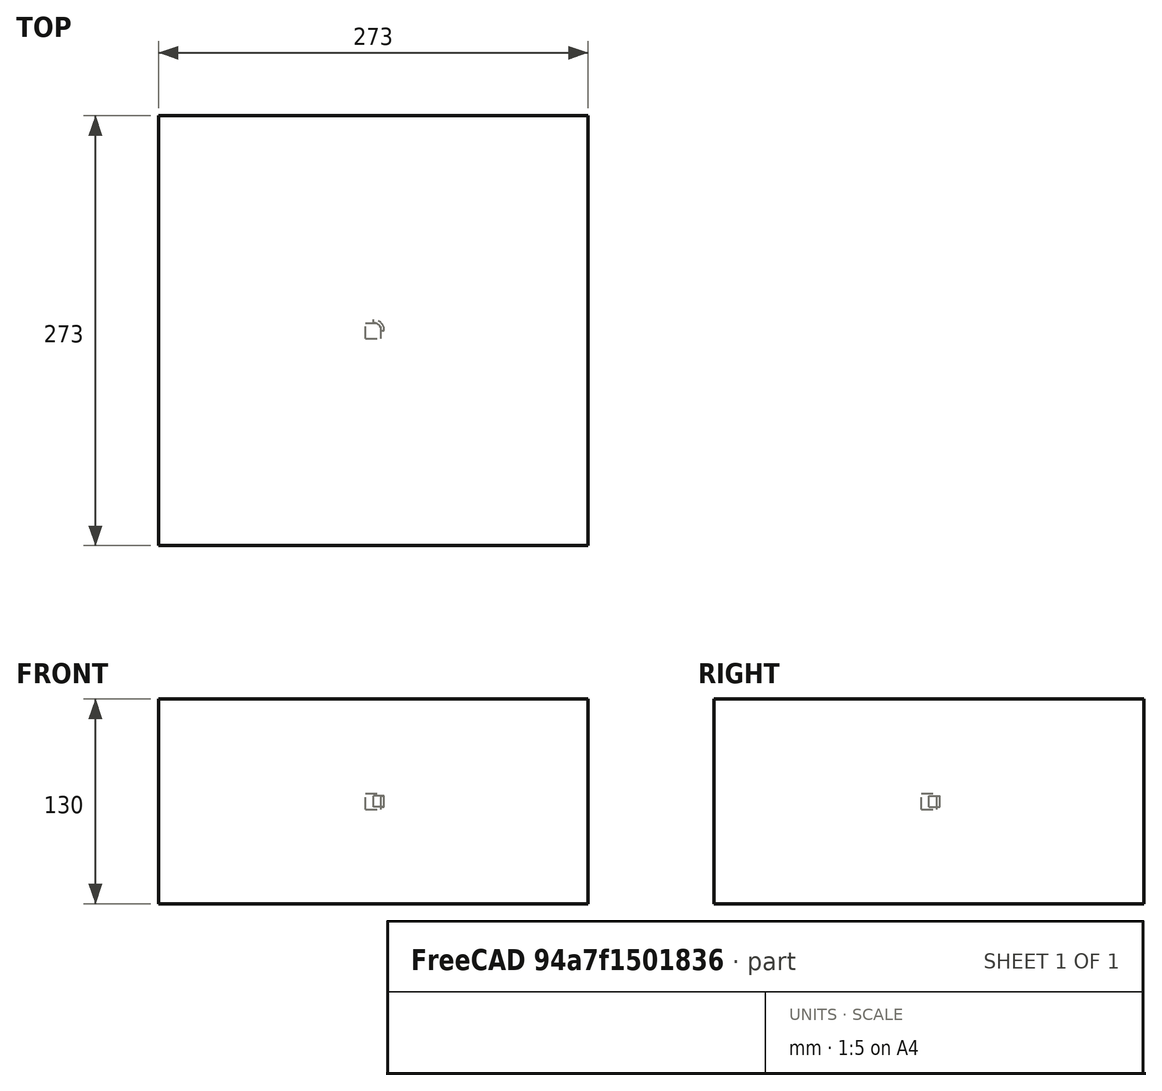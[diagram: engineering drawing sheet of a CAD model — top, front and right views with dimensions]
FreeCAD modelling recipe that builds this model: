
FCSTD DOCUMENT  (FreeCAD 0.20RUnknown)
Label: polarArray-container-a
License: All rights reserved
LicenseURL: http://en.wikipedia.org/wiki/All_rights_reserved
objects: App::DocumentObjectGroupPython×1251, Part::FeaturePython×4, App::Part×4
note: 3 computed .brp shape members not serialized (recipe doc carries the construction recipe); baked Part::Feature solids carry a one-line shape summary decoded from their .brp

FEATURE [App::DocumentObjectGroupPython] HALFPI  # scripted group (container) (typed FeaturePython)
  name = HALFPI
  value = pi/2.
FEATURE [App::DocumentObjectGroupPython] PI  # scripted group (container) (typed FeaturePython)
  name = PI
  value = 1.*pi
FEATURE [App::DocumentObjectGroupPython] TWOPI  # scripted group (container) (typed FeaturePython)
  name = TWOPI
  value = 2.*pi
FEATURE [App::DocumentObjectGroupPython] Constants  # scripted group (container) (typed FeaturePython)
  Group = -> [HALFPI,PI,TWOPI]
FEATURE [App::DocumentObjectGroupPython] Variables  # scripted group (container) (typed FeaturePython)
FEATURE [App::DocumentObjectGroupPython] Quantities  # scripted group (container) (typed FeaturePython)
FEATURE [App::DocumentObjectGroupPython] Isotopes  # scripted group (container) (typed FeaturePython)
FEATURE [App::DocumentObjectGroupPython] Elements  # scripted group (container) (typed FeaturePython)
FEATURE [App::DocumentObjectGroupPython] Matrix  # scripted group (container) (typed FeaturePython)
FEATURE [App::DocumentObjectGroupPython] Surfaces  # scripted group (container) (typed FeaturePython)
FEATURE [App::DocumentObjectGroupPython] Opticals  # scripted group (container) (typed FeaturePython)
  Group = -> [Matrix,Surfaces]
FEATURE [App::DocumentObjectGroupPython] G4Isotopes  # scripted group (container) (typed FeaturePython)
FEATURE [App::DocumentObjectGroupPython] H_element  # scripted group (container) (typed FeaturePython)
  Z = 1
  atom_value = 1.008
  formula = H
  name = H_element
FEATURE [App::DocumentObjectGroupPython] He_element  # scripted group (container) (typed FeaturePython)
  Z = 2
  atom_value = 4.0026
  formula = He
  name = He_element
FEATURE [App::DocumentObjectGroupPython] Li_element  # scripted group (container) (typed FeaturePython)
  Z = 3
  atom_value = 6.94
  formula = Li
  name = Li_element
FEATURE [App::DocumentObjectGroupPython] Be_element  # scripted group (container) (typed FeaturePython)
  Z = 4
  atom_value = 9.01218
  formula = Be
  name = Be_element
FEATURE [App::DocumentObjectGroupPython] B_element  # scripted group (container) (typed FeaturePython)
  Z = 5
  atom_value = 10.81
  formula = B
  name = B_element
FEATURE [App::DocumentObjectGroupPython] C_element  # scripted group (container) (typed FeaturePython)
  Z = 6
  atom_value = 12.011
  formula = C
  name = C_element
FEATURE [App::DocumentObjectGroupPython] N_element  # scripted group (container) (typed FeaturePython)
  Z = 7
  atom_value = 14.007
  formula = N
  name = N_element
FEATURE [App::DocumentObjectGroupPython] O_element  # scripted group (container) (typed FeaturePython)
  Z = 8
  atom_value = 15.999
  formula = O
  name = O_element
FEATURE [App::DocumentObjectGroupPython] F_element  # scripted group (container) (typed FeaturePython)
  Z = 9
  atom_value = 18.9984
  formula = F
  name = F_element
FEATURE [App::DocumentObjectGroupPython] Ne_element  # scripted group (container) (typed FeaturePython)
  Z = 10
  atom_value = 20.1797
  formula = Ne
  name = Ne_element
FEATURE [App::DocumentObjectGroupPython] Na_element  # scripted group (container) (typed FeaturePython)
  Z = 11
  atom_value = 22.9898
  formula = Na
  name = Na_element
FEATURE [App::DocumentObjectGroupPython] Mg_element  # scripted group (container) (typed FeaturePython)
  Z = 12
  atom_value = 24.305
  formula = Mg
  name = Mg_element
FEATURE [App::DocumentObjectGroupPython] Al_element  # scripted group (container) (typed FeaturePython)
  Z = 13
  atom_value = 26.9815
  formula = Al
  name = Al_element
FEATURE [App::DocumentObjectGroupPython] Si_element  # scripted group (container) (typed FeaturePython)
  Z = 14
  atom_value = 28.085
  formula = Si
  name = Si_element
FEATURE [App::DocumentObjectGroupPython] P_element  # scripted group (container) (typed FeaturePython)
  Z = 15
  atom_value = 30.9738
  formula = P
  name = P_element
FEATURE [App::DocumentObjectGroupPython] S_element  # scripted group (container) (typed FeaturePython)
  Z = 16
  atom_value = 32.06
  formula = S
  name = S_element
FEATURE [App::DocumentObjectGroupPython] Cl_element  # scripted group (container) (typed FeaturePython)
  Z = 17
  atom_value = 35.45
  formula = Cl
  name = Cl_element
FEATURE [App::DocumentObjectGroupPython] Ar_element  # scripted group (container) (typed FeaturePython)
  Z = 18
  atom_value = 39.95
  formula = Ar
  name = Ar_element
FEATURE [App::DocumentObjectGroupPython] K_element  # scripted group (container) (typed FeaturePython)
  Z = 19
  atom_value = 39.0983
  formula = K
  name = K_element
FEATURE [App::DocumentObjectGroupPython] Ca_element  # scripted group (container) (typed FeaturePython)
  Z = 20
  atom_value = 40.078
  formula = Ca
  name = Ca_element
FEATURE [App::DocumentObjectGroupPython] Sc_element  # scripted group (container) (typed FeaturePython)
  Z = 21
  atom_value = 44.9559
  formula = Sc
  name = Sc_element
FEATURE [App::DocumentObjectGroupPython] Ti_element  # scripted group (container) (typed FeaturePython)
  Z = 22
  atom_value = 47.867
  formula = Ti
  name = Ti_element
FEATURE [App::DocumentObjectGroupPython] V_element  # scripted group (container) (typed FeaturePython)
  Z = 23
  atom_value = 50.9415
  formula = V
  name = V_element
FEATURE [App::DocumentObjectGroupPython] Cr_element  # scripted group (container) (typed FeaturePython)
  Z = 24
  atom_value = 51.9961
  formula = Cr
  name = Cr_element
FEATURE [App::DocumentObjectGroupPython] Mn_element  # scripted group (container) (typed FeaturePython)
  Z = 25
  atom_value = 54.938
  formula = Mn
  name = Mn_element
FEATURE [App::DocumentObjectGroupPython] Fe_element  # scripted group (container) (typed FeaturePython)
  Z = 26
  atom_value = 55.845
  formula = Fe
  name = Fe_element
FEATURE [App::DocumentObjectGroupPython] Co_element  # scripted group (container) (typed FeaturePython)
  Z = 27
  atom_value = 58.9332
  formula = Co
  name = Co_element
FEATURE [App::DocumentObjectGroupPython] Ni_element  # scripted group (container) (typed FeaturePython)
  Z = 28
  atom_value = 58.6934
  formula = Ni
  name = Ni_element
FEATURE [App::DocumentObjectGroupPython] Cu_element  # scripted group (container) (typed FeaturePython)
  Z = 29
  atom_value = 63.546
  formula = Cu
  name = Cu_element
FEATURE [App::DocumentObjectGroupPython] Zn_element  # scripted group (container) (typed FeaturePython)
  Z = 30
  atom_value = 65.38
  formula = Zn
  name = Zn_element
FEATURE [App::DocumentObjectGroupPython] Ga_element  # scripted group (container) (typed FeaturePython)
  Z = 31
  atom_value = 69.723
  formula = Ga
  name = Ga_element
FEATURE [App::DocumentObjectGroupPython] Ge_element  # scripted group (container) (typed FeaturePython)
  Z = 32
  atom_value = 72.63
  formula = Ge
  name = Ge_element
FEATURE [App::DocumentObjectGroupPython] As_element  # scripted group (container) (typed FeaturePython)
  Z = 33
  atom_value = 74.9216
  formula = As
  name = As_element
FEATURE [App::DocumentObjectGroupPython] Se_element  # scripted group (container) (typed FeaturePython)
  Z = 34
  atom_value = 78.971
  formula = Se
  name = Se_element
FEATURE [App::DocumentObjectGroupPython] Br_element  # scripted group (container) (typed FeaturePython)
  Z = 35
  atom_value = 79.904
  formula = Br
  name = Br_element
FEATURE [App::DocumentObjectGroupPython] Kr_element  # scripted group (container) (typed FeaturePython)
  Z = 36
  atom_value = 83.798
  formula = Kr
  name = Kr_element
FEATURE [App::DocumentObjectGroupPython] Rb_element  # scripted group (container) (typed FeaturePython)
  Z = 37
  atom_value = 85.4678
  formula = Rb
  name = Rb_element
FEATURE [App::DocumentObjectGroupPython] Sr_element  # scripted group (container) (typed FeaturePython)
  Z = 38
  atom_value = 87.62
  formula = Sr
  name = Sr_element
FEATURE [App::DocumentObjectGroupPython] Y_element  # scripted group (container) (typed FeaturePython)
  Z = 39
  atom_value = 88.9058
  formula = Y
  name = Y_element
FEATURE [App::DocumentObjectGroupPython] Zr_element  # scripted group (container) (typed FeaturePython)
  Z = 40
  atom_value = 91.224
  formula = Zr
  name = Zr_element
FEATURE [App::DocumentObjectGroupPython] Nb_element  # scripted group (container) (typed FeaturePython)
  Z = 41
  atom_value = 92.9064
  formula = Nb
  name = Nb_element
FEATURE [App::DocumentObjectGroupPython] Mo_element  # scripted group (container) (typed FeaturePython)
  Z = 42
  atom_value = 95.95
  formula = Mo
  name = Mo_element
FEATURE [App::DocumentObjectGroupPython] Tc_element  # scripted group (container) (typed FeaturePython)
  Z = 43
  atom_value = 97
  formula = Tc
  name = Tc_element
FEATURE [App::DocumentObjectGroupPython] Ru_element  # scripted group (container) (typed FeaturePython)
  Z = 44
  atom_value = 101.07
  formula = Ru
  name = Ru_element
FEATURE [App::DocumentObjectGroupPython] Rh_element  # scripted group (container) (typed FeaturePython)
  Z = 45
  atom_value = 102.905
  formula = Rh
  name = Rh_element
FEATURE [App::DocumentObjectGroupPython] Pd_element  # scripted group (container) (typed FeaturePython)
  Z = 46
  atom_value = 106.42
  formula = Pd
  name = Pd_element
FEATURE [App::DocumentObjectGroupPython] Ag_element  # scripted group (container) (typed FeaturePython)
  Z = 47
  atom_value = 107.868
  formula = Ag
  name = Ag_element
FEATURE [App::DocumentObjectGroupPython] Cd_element  # scripted group (container) (typed FeaturePython)
  Z = 48
  atom_value = 112.414
  formula = Cd
  name = Cd_element
FEATURE [App::DocumentObjectGroupPython] In_element  # scripted group (container) (typed FeaturePython)
  Z = 49
  atom_value = 114.818
  formula = In
  name = In_element
FEATURE [App::DocumentObjectGroupPython] Sn_element  # scripted group (container) (typed FeaturePython)
  Z = 50
  atom_value = 118.71
  formula = Sn
  name = Sn_element
FEATURE [App::DocumentObjectGroupPython] Sb_element  # scripted group (container) (typed FeaturePython)
  Z = 51
  atom_value = 121.76
  formula = Sb
  name = Sb_element
FEATURE [App::DocumentObjectGroupPython] Te_element  # scripted group (container) (typed FeaturePython)
  Z = 52
  atom_value = 127.6
  formula = Te
  name = Te_element
FEATURE [App::DocumentObjectGroupPython] I_element  # scripted group (container) (typed FeaturePython)
  Z = 53
  atom_value = 126.904
  formula = I
  name = I_element
FEATURE [App::DocumentObjectGroupPython] Xe_element  # scripted group (container) (typed FeaturePython)
  Z = 54
  atom_value = 131.293
  formula = Xe
  name = Xe_element
FEATURE [App::DocumentObjectGroupPython] Cs_element  # scripted group (container) (typed FeaturePython)
  Z = 55
  atom_value = 132.905
  formula = Cs
  name = Cs_element
FEATURE [App::DocumentObjectGroupPython] Ba_element  # scripted group (container) (typed FeaturePython)
  Z = 56
  atom_value = 137.327
  formula = Ba
  name = Ba_element
FEATURE [App::DocumentObjectGroupPython] La_element  # scripted group (container) (typed FeaturePython)
  Z = 57
  atom_value = 138.905
  formula = La
  name = La_element
FEATURE [App::DocumentObjectGroupPython] Ce_element  # scripted group (container) (typed FeaturePython)
  Z = 58
  atom_value = 140.116
  formula = Ce
  name = Ce_element
FEATURE [App::DocumentObjectGroupPython] Pr_element  # scripted group (container) (typed FeaturePython)
  Z = 59
  atom_value = 140.908
  formula = Pr
  name = Pr_element
FEATURE [App::DocumentObjectGroupPython] Nd_element  # scripted group (container) (typed FeaturePython)
  Z = 60
  atom_value = 144.242
  formula = Nd
  name = Nd_element
FEATURE [App::DocumentObjectGroupPython] Pm_element  # scripted group (container) (typed FeaturePython)
  Z = 61
  atom_value = 145
  formula = Pm
  name = Pm_element
FEATURE [App::DocumentObjectGroupPython] Sm_element  # scripted group (container) (typed FeaturePython)
  Z = 62
  atom_value = 150.36
  formula = Sm
  name = Sm_element
FEATURE [App::DocumentObjectGroupPython] Eu_element  # scripted group (container) (typed FeaturePython)
  Z = 63
  atom_value = 151.964
  formula = Eu
  name = Eu_element
FEATURE [App::DocumentObjectGroupPython] Gd_element  # scripted group (container) (typed FeaturePython)
  Z = 64
  atom_value = 157.25
  formula = Gd
  name = Gd_element
FEATURE [App::DocumentObjectGroupPython] Tb_element  # scripted group (container) (typed FeaturePython)
  Z = 65
  atom_value = 158.925
  formula = Tb
  name = Tb_element
FEATURE [App::DocumentObjectGroupPython] Dy_element  # scripted group (container) (typed FeaturePython)
  Z = 66
  atom_value = 162.5
  formula = Dy
  name = Dy_element
FEATURE [App::DocumentObjectGroupPython] Ho_element  # scripted group (container) (typed FeaturePython)
  Z = 67
  atom_value = 164.93
  formula = Ho
  name = Ho_element
FEATURE [App::DocumentObjectGroupPython] Er_element  # scripted group (container) (typed FeaturePython)
  Z = 68
  atom_value = 167.259
  formula = Er
  name = Er_element
FEATURE [App::DocumentObjectGroupPython] Tm_element  # scripted group (container) (typed FeaturePython)
  Z = 69
  atom_value = 168.934
  formula = Tm
  name = Tm_element
FEATURE [App::DocumentObjectGroupPython] Yb_element  # scripted group (container) (typed FeaturePython)
  Z = 70
  atom_value = 173.045
  formula = Yb
  name = Yb_element
FEATURE [App::DocumentObjectGroupPython] Lu_element  # scripted group (container) (typed FeaturePython)
  Z = 71
  atom_value = 174.967
  formula = Lu
  name = Lu_element
FEATURE [App::DocumentObjectGroupPython] Hf_element  # scripted group (container) (typed FeaturePython)
  Z = 72
  atom_value = 178.49
  formula = Hf
  name = Hf_element
FEATURE [App::DocumentObjectGroupPython] Ta_element  # scripted group (container) (typed FeaturePython)
  Z = 73
  atom_value = 180.948
  formula = Ta
  name = Ta_element
FEATURE [App::DocumentObjectGroupPython] W_element  # scripted group (container) (typed FeaturePython)
  Z = 74
  atom_value = 183.84
  formula = W
  name = W_element
FEATURE [App::DocumentObjectGroupPython] Re_element  # scripted group (container) (typed FeaturePython)
  Z = 75
  atom_value = 186.207
  formula = Re
  name = Re_element
FEATURE [App::DocumentObjectGroupPython] Os_element  # scripted group (container) (typed FeaturePython)
  Z = 76
  atom_value = 190.23
  formula = Os
  name = Os_element
FEATURE [App::DocumentObjectGroupPython] Ir_element  # scripted group (container) (typed FeaturePython)
  Z = 77
  atom_value = 192.217
  formula = Ir
  name = Ir_element
FEATURE [App::DocumentObjectGroupPython] Pt_element  # scripted group (container) (typed FeaturePython)
  Z = 78
  atom_value = 195.084
  formula = Pt
  name = Pt_element
FEATURE [App::DocumentObjectGroupPython] Au_element  # scripted group (container) (typed FeaturePython)
  Z = 79
  atom_value = 196.967
  formula = Au
  name = Au_element
FEATURE [App::DocumentObjectGroupPython] Hg_element  # scripted group (container) (typed FeaturePython)
  Z = 80
  atom_value = 200.592
  formula = Hg
  name = Hg_element
FEATURE [App::DocumentObjectGroupPython] Tl_element  # scripted group (container) (typed FeaturePython)
  Z = 81
  atom_value = 204.38
  formula = Tl
  name = Tl_element
FEATURE [App::DocumentObjectGroupPython] Pb_element  # scripted group (container) (typed FeaturePython)
  Z = 82
  atom_value = 207.2
  formula = Pb
  name = Pb_element
FEATURE [App::DocumentObjectGroupPython] Bi_element  # scripted group (container) (typed FeaturePython)
  Z = 83
  atom_value = 208.98
  formula = Bi
  name = Bi_element
FEATURE [App::DocumentObjectGroupPython] Po_element  # scripted group (container) (typed FeaturePython)
  Z = 84
  atom_value = 209
  formula = Po
  name = Po_element
FEATURE [App::DocumentObjectGroupPython] At_element  # scripted group (container) (typed FeaturePython)
  Z = 85
  atom_value = 210
  formula = At
  name = At_element
FEATURE [App::DocumentObjectGroupPython] Rn_element  # scripted group (container) (typed FeaturePython)
  Z = 86
  atom_value = 222
  formula = Rn
  name = Rn_element
FEATURE [App::DocumentObjectGroupPython] Fr_element  # scripted group (container) (typed FeaturePython)
  Z = 87
  atom_value = 223
  formula = Fr
  name = Fr_element
FEATURE [App::DocumentObjectGroupPython] Ra_element  # scripted group (container) (typed FeaturePython)
  Z = 88
  atom_value = 226
  formula = Ra
  name = Ra_element
FEATURE [App::DocumentObjectGroupPython] Ac_element  # scripted group (container) (typed FeaturePython)
  Z = 89
  atom_value = 227
  formula = Ac
  name = Ac_element
FEATURE [App::DocumentObjectGroupPython] Th_element  # scripted group (container) (typed FeaturePython)
  Z = 90
  atom_value = 232.038
  formula = Th
  name = Th_element
FEATURE [App::DocumentObjectGroupPython] Pa_element  # scripted group (container) (typed FeaturePython)
  Z = 91
  atom_value = 231.036
  formula = Pa
  name = Pa_element
FEATURE [App::DocumentObjectGroupPython] U_element  # scripted group (container) (typed FeaturePython)
  Z = 92
  atom_value = 238.029
  formula = U
  name = U_element
FEATURE [App::DocumentObjectGroupPython] Np_element  # scripted group (container) (typed FeaturePython)
  Z = 93
  atom_value = 237
  formula = Np
  name = Np_element
FEATURE [App::DocumentObjectGroupPython] Pu_element  # scripted group (container) (typed FeaturePython)
  Z = 94
  atom_value = 244
  formula = Pu
  name = Pu_element
FEATURE [App::DocumentObjectGroupPython] Am_element  # scripted group (container) (typed FeaturePython)
  Z = 95
  atom_value = 243
  formula = Am
  name = Am_element
FEATURE [App::DocumentObjectGroupPython] Cm_element  # scripted group (container) (typed FeaturePython)
  Z = 96
  atom_value = 247
  formula = Cm
  name = Cm_element
FEATURE [App::DocumentObjectGroupPython] Bk_element  # scripted group (container) (typed FeaturePython)
  Z = 97
  atom_value = 247
  formula = Bk
  name = Bk_element
FEATURE [App::DocumentObjectGroupPython] Cf_element  # scripted group (container) (typed FeaturePython)
  Z = 98
  atom_value = 251
  formula = Cf
  name = Cf_element
FEATURE [App::DocumentObjectGroupPython] G4Elements  # scripted group (container) (typed FeaturePython)
  Group = -> [H_element,He_element,Li_element,Be_element,B_element,C_element,N_element,O_element,F_element,Ne_element,Na_element,Mg_element,Al_element,Si_element,P_element,S_element,Cl_element,Ar_element,K_element,Ca_element,Sc_element,Ti_element,V_element,Cr_element,Mn_element,Fe_element,Co_element,Ni_element,Cu_element,Zn_element,Ga_element,Ge_element,As_element,Se_element,Br_element,Kr_element,Rb_element,+61 more]
FEATURE [App::DocumentObjectGroupPython] H_element001  label="H_element : 0.101"  # scripted group (container) (typed FeaturePython)
  n = 0.101327
FEATURE [App::DocumentObjectGroupPython] C_element001  label="C_element : 0.775"  # scripted group (container) (typed FeaturePython)
  n = 0.7755
FEATURE [App::DocumentObjectGroupPython] N_element001  label="N_element : 0.035"  # scripted group (container) (typed FeaturePython)
  n = 0.035057
FEATURE [App::DocumentObjectGroupPython] O_element001  label="O_element : 0.052"  # scripted group (container) (typed FeaturePython)
  n = 0.0523159
FEATURE [App::DocumentObjectGroupPython] F_element001  label="F_element : 0.017"  # scripted group (container) (typed FeaturePython)
  n = 0.017422
FEATURE [App::DocumentObjectGroupPython] Ca_element001  label="Ca_element : 0.018"  # scripted group (container) (typed FeaturePython)
  n = 0.018378
FEATURE [App::DocumentObjectGroupPython] G4_A_150_TISSUE  label="G4_A-150_TISSUE"  # scripted group (container) (typed FeaturePython)
  Dunit = g/cm3
  Dvalue = 1.127
  Group = -> [H_element001,C_element001,N_element001,O_element001,F_element001,Ca_element001]
  conduct = 2
  density = 1
  expand = 3
  formula = G4_A-150_TISSUE
  name = G4_A-150_TISSUE
  specific = 4
FEATURE [App::DocumentObjectGroupPython] C_element002  label="C_element : 3"  # scripted group (container) (typed FeaturePython)
  n = 3
  ref = C_element
FEATURE [App::DocumentObjectGroupPython] H_element002  label="H_element : 6"  # scripted group (container) (typed FeaturePython)
  n = 6
  ref = H_element
FEATURE [App::DocumentObjectGroupPython] O_element002  label="O_element : 1"  # scripted group (container) (typed FeaturePython)
  n = 1
  ref = O_element
FEATURE [App::DocumentObjectGroupPython] G4_ACETONE  # scripted group (container) (typed FeaturePython)
  Dunit = g/cm3
  Dvalue = 0.7899
  Group = -> [C_element002,H_element002,O_element002]
  conduct = 2
  density = 1
  expand = 3
  formula = G4_ACETONE
  name = G4_ACETONE
  specific = 4
FEATURE [App::DocumentObjectGroupPython] C_element003  label="C_element : 2"  # scripted group (container) (typed FeaturePython)
  n = 2
  ref = C_element
FEATURE [App::DocumentObjectGroupPython] H_element003  label="H_element : 2"  # scripted group (container) (typed FeaturePython)
  n = 2
  ref = H_element
FEATURE [App::DocumentObjectGroupPython] G4_ACETYLENE  # scripted group (container) (typed FeaturePython)
  Dunit = g/cm3
  Dvalue = 0.0010967
  Group = -> [C_element003,H_element003]
  conduct = 2
  density = 1
  expand = 3
  formula = G4_ACETYLENE
  name = G4_ACETYLENE
  specific = 4
FEATURE [App::DocumentObjectGroupPython] C_element004  label="C_element : 5"  # scripted group (container) (typed FeaturePython)
  n = 5
  ref = C_element
FEATURE [App::DocumentObjectGroupPython] H_element004  label="H_element : 5"  # scripted group (container) (typed FeaturePython)
  n = 5
  ref = H_element
FEATURE [App::DocumentObjectGroupPython] N_element002  label="N_element : 5"  # scripted group (container) (typed FeaturePython)
  n = 5
  ref = N_element
FEATURE [App::DocumentObjectGroupPython] G4_ADENINE  # scripted group (container) (typed FeaturePython)
  Dunit = g/cm3
  Dvalue = 1.6
  Group = -> [C_element004,H_element004,N_element002]
  conduct = 2
  density = 1
  expand = 3
  formula = G4_ADENINE
  name = G4_ADENINE
  specific = 4
FEATURE [App::DocumentObjectGroupPython] H_element005  label="H_element : 0.114"  # scripted group (container) (typed FeaturePython)
  n = 0.114
FEATURE [App::DocumentObjectGroupPython] C_element005  label="C_element : 0.598"  # scripted group (container) (typed FeaturePython)
  n = 0.598
FEATURE [App::DocumentObjectGroupPython] N_element003  label="N_element : 0.007"  # scripted group (container) (typed FeaturePython)
  n = 0.007
FEATURE [App::DocumentObjectGroupPython] O_element003  label="O_element : 0.278"  # scripted group (container) (typed FeaturePython)
  n = 0.278
FEATURE [App::DocumentObjectGroupPython] Na_element001  label="Na_element : 0.001"  # scripted group (container) (typed FeaturePython)
  n = 0.001
FEATURE [App::DocumentObjectGroupPython] S_element001  label="S_element : 0.001"  # scripted group (container) (typed FeaturePython)
  n = 0.001
FEATURE [App::DocumentObjectGroupPython] Cl_element001  label="Cl_element : 0.001"  # scripted group (container) (typed FeaturePython)
  n = 0.001
FEATURE [App::DocumentObjectGroupPython] G4_ADIPOSE_TISSUE_ICRP  # scripted group (container) (typed FeaturePython)
  Dunit = g/cm3
  Dvalue = 0.95
  Group = -> [H_element005,C_element005,N_element003,O_element003,Na_element001,S_element001,Cl_element001]
  conduct = 2
  density = 1
  expand = 3
  formula = G4_ADIPOSE_TISSUE_ICRP
  name = G4_ADIPOSE_TISSUE_ICRP
  specific = 4
FEATURE [App::DocumentObjectGroupPython] C_element006  label="C_element : 0.000"  # scripted group (container) (typed FeaturePython)
  n = 0.000124
FEATURE [App::DocumentObjectGroupPython] N_element004  label="N_element : 0.755"  # scripted group (container) (typed FeaturePython)
  n = 0.755268
FEATURE [App::DocumentObjectGroupPython] O_element004  label="O_element : 0.232"  # scripted group (container) (typed FeaturePython)
  n = 0.231781
FEATURE [App::DocumentObjectGroupPython] Ar_element001  label="Ar_element : 0.013"  # scripted group (container) (typed FeaturePython)
  n = 0.012827
FEATURE [App::DocumentObjectGroupPython] G4_AIR  # scripted group (container) (typed FeaturePython)
  Dunit = g/cm3
  Dvalue = 0.00120479
  Group = -> [C_element006,N_element004,O_element004,Ar_element001]
  conduct = 2
  density = 1
  expand = 3
  formula = G4_AIR
  name = G4_AIR
  specific = 4
FEATURE [App::DocumentObjectGroupPython] C_element007  label="C_element : 006"  # scripted group (container) (typed FeaturePython)
  n = 3
  ref = C_element
FEATURE [App::DocumentObjectGroupPython] H_element006  label="H_element : 7"  # scripted group (container) (typed FeaturePython)
  n = 7
  ref = H_element
FEATURE [App::DocumentObjectGroupPython] N_element005  label="N_element : 1"  # scripted group (container) (typed FeaturePython)
  n = 1
  ref = N_element
FEATURE [App::DocumentObjectGroupPython] O_element005  label="O_element : 2"  # scripted group (container) (typed FeaturePython)
  n = 2
  ref = O_element
FEATURE [App::DocumentObjectGroupPython] G4_ALANINE  # scripted group (container) (typed FeaturePython)
  Dunit = g/cm3
  Dvalue = 1.42
  Group = -> [C_element007,H_element006,N_element005,O_element005]
  conduct = 2
  density = 1
  expand = 3
  formula = G4_ALANINE
  name = G4_ALANINE
  specific = 4
FEATURE [App::DocumentObjectGroupPython] Al_element001  label="Al_element : 2"  # scripted group (container) (typed FeaturePython)
  n = 2
  ref = Al_element
FEATURE [App::DocumentObjectGroupPython] O_element006  label="O_element : 3"  # scripted group (container) (typed FeaturePython)
  n = 3
  ref = O_element
FEATURE [App::DocumentObjectGroupPython] G4_ALUMINUM_OXIDE  # scripted group (container) (typed FeaturePython)
  Dunit = g/cm3
  Dvalue = 3.97
  Group = -> [Al_element001,O_element006]
  conduct = 2
  density = 1
  expand = 3
  formula = G4_ALUMINUM_OXIDE
  name = G4_ALUMINUM_OXIDE
  specific = 4
FEATURE [App::DocumentObjectGroupPython] H_element007  label="H_element : 0.106"  # scripted group (container) (typed FeaturePython)
  n = 0.10593
FEATURE [App::DocumentObjectGroupPython] C_element008  label="C_element : 0.789"  # scripted group (container) (typed FeaturePython)
  n = 0.788974
FEATURE [App::DocumentObjectGroupPython] O_element007  label="O_element : 0.105"  # scripted group (container) (typed FeaturePython)
  n = 0.105096
FEATURE [App::DocumentObjectGroupPython] G4_AMBER  # scripted group (container) (typed FeaturePython)
  Dunit = g/cm3
  Dvalue = 1.1
  Group = -> [H_element007,C_element008,O_element007]
  conduct = 2
  density = 1
  expand = 3
  formula = G4_AMBER
  name = G4_AMBER
  specific = 4
FEATURE [App::DocumentObjectGroupPython] N_element006  label="N_element : 006"  # scripted group (container) (typed FeaturePython)
  n = 1
  ref = N_element
FEATURE [App::DocumentObjectGroupPython] H_element008  label="H_element : 3"  # scripted group (container) (typed FeaturePython)
  n = 3
  ref = H_element
FEATURE [App::DocumentObjectGroupPython] G4_AMMONIA  # scripted group (container) (typed FeaturePython)
  Dunit = g/cm3
  Dvalue = 0.000826019
  Group = -> [N_element006,H_element008]
  conduct = 2
  density = 1
  expand = 3
  formula = G4_AMMONIA
  name = G4_AMMONIA
  specific = 4
FEATURE [App::DocumentObjectGroupPython] C_element009  label="C_element : 6"  # scripted group (container) (typed FeaturePython)
  n = 6
  ref = C_element
FEATURE [App::DocumentObjectGroupPython] H_element009  label="H_element : 008"  # scripted group (container) (typed FeaturePython)
  n = 7
  ref = H_element
FEATURE [App::DocumentObjectGroupPython] N_element007  label="N_element : 007"  # scripted group (container) (typed FeaturePython)
  n = 1
  ref = N_element
FEATURE [App::DocumentObjectGroupPython] G4_ANILINE  # scripted group (container) (typed FeaturePython)
  Dunit = g/cm3
  Dvalue = 1.0235
  Group = -> [C_element009,H_element009,N_element007]
  conduct = 2
  density = 1
  expand = 3
  formula = G4_ANILINE
  name = G4_ANILINE
  specific = 4
FEATURE [App::DocumentObjectGroupPython] C_element010  label="C_element : 14"  # scripted group (container) (typed FeaturePython)
  n = 14
  ref = C_element
FEATURE [App::DocumentObjectGroupPython] H_element010  label="H_element : 10"  # scripted group (container) (typed FeaturePython)
  n = 10
  ref = H_element
FEATURE [App::DocumentObjectGroupPython] G4_ANTHRACENE  # scripted group (container) (typed FeaturePython)
  Dunit = g/cm3
  Dvalue = 1.283
  Group = -> [C_element010,H_element010]
  conduct = 2
  density = 1
  expand = 3
  formula = G4_ANTHRACENE
  name = G4_ANTHRACENE
  specific = 4
FEATURE [App::DocumentObjectGroupPython] H_element011  label="H_element : 0.065"  # scripted group (container) (typed FeaturePython)
  n = 0.0654709
FEATURE [App::DocumentObjectGroupPython] C_element011  label="C_element : 0.537"  # scripted group (container) (typed FeaturePython)
  n = 0.536944
FEATURE [App::DocumentObjectGroupPython] N_element008  label="N_element : 0.021"  # scripted group (container) (typed FeaturePython)
  n = 0.0215
FEATURE [App::DocumentObjectGroupPython] O_element008  label="O_element : 0.032"  # scripted group (container) (typed FeaturePython)
  n = 0.032085
FEATURE [App::DocumentObjectGroupPython] F_element002  label="F_element : 0.167"  # scripted group (container) (typed FeaturePython)
  n = 0.167411
FEATURE [App::DocumentObjectGroupPython] Ca_element002  label="Ca_element : 0.177"  # scripted group (container) (typed FeaturePython)
  n = 0.176589
FEATURE [App::DocumentObjectGroupPython] G4_B_100_BONE  label="G4_B-100_BONE"  # scripted group (container) (typed FeaturePython)
  Dunit = g/cm3
  Dvalue = 1.45
  Group = -> [H_element011,C_element011,N_element008,O_element008,F_element002,Ca_element002]
  conduct = 2
  density = 1
  expand = 3
  formula = G4_B-100_BONE
  name = G4_B-100_BONE
  specific = 4
FEATURE [App::DocumentObjectGroupPython] H_element012  label="H_element : 0.057"  # scripted group (container) (typed FeaturePython)
  n = 0.057441
FEATURE [App::DocumentObjectGroupPython] C_element012  label="C_element : 0.790"  # scripted group (container) (typed FeaturePython)
  n = 0.774591
FEATURE [App::DocumentObjectGroupPython] O_element009  label="O_element : 0.168"  # scripted group (container) (typed FeaturePython)
  n = 0.167968
FEATURE [App::DocumentObjectGroupPython] G4_BAKELITE  # scripted group (container) (typed FeaturePython)
  Dunit = g/cm3
  Dvalue = 1.25
  Group = -> [H_element012,C_element012,O_element009]
  conduct = 2
  density = 1
  expand = 3
  formula = G4_BAKELITE
  name = G4_BAKELITE
  specific = 4
FEATURE [App::DocumentObjectGroupPython] Ba_element001  label="Ba_element : 1"  # scripted group (container) (typed FeaturePython)
  n = 1
  ref = Ba_element
FEATURE [App::DocumentObjectGroupPython] F_element003  label="F_element : 2"  # scripted group (container) (typed FeaturePython)
  n = 2
  ref = F_element
FEATURE [App::DocumentObjectGroupPython] G4_BARIUM_FLUORIDE  # scripted group (container) (typed FeaturePython)
  Dunit = g/cm3
  Dvalue = 4.89
  Group = -> [Ba_element001,F_element003]
  conduct = 2
  density = 1
  expand = 3
  formula = G4_BARIUM_FLUORIDE
  name = G4_BARIUM_FLUORIDE
  specific = 4
FEATURE [App::DocumentObjectGroupPython] Ba_element002  label="Ba_element : 002"  # scripted group (container) (typed FeaturePython)
  n = 1
  ref = Ba_element
FEATURE [App::DocumentObjectGroupPython] S_element002  label="S_element : 1"  # scripted group (container) (typed FeaturePython)
  n = 1
  ref = S_element
FEATURE [App::DocumentObjectGroupPython] O_element010  label="O_element : 4"  # scripted group (container) (typed FeaturePython)
  n = 4
  ref = O_element
FEATURE [App::DocumentObjectGroupPython] G4_BARIUM_SULFATE  # scripted group (container) (typed FeaturePython)
  Dunit = g/cm3
  Dvalue = 4.5
  Group = -> [Ba_element002,S_element002,O_element010]
  conduct = 2
  density = 1
  expand = 3
  formula = G4_BARIUM_SULFATE
  name = G4_BARIUM_SULFATE
  specific = 4
FEATURE [App::DocumentObjectGroupPython] C_element013  label="C_element : 007"  # scripted group (container) (typed FeaturePython)
  n = 6
  ref = C_element
FEATURE [App::DocumentObjectGroupPython] H_element013  label="H_element : 009"  # scripted group (container) (typed FeaturePython)
  n = 6
  ref = H_element
FEATURE [App::DocumentObjectGroupPython] G4_BENZENE  # scripted group (container) (typed FeaturePython)
  Dunit = g/cm3
  Dvalue = 0.87865
  Group = -> [C_element013,H_element013]
  conduct = 2
  density = 1
  expand = 3
  formula = G4_BENZENE
  name = G4_BENZENE
  specific = 4
FEATURE [App::DocumentObjectGroupPython] Be_element001  label="Be_element : 1"  # scripted group (container) (typed FeaturePython)
  n = 1
  ref = Be_element
FEATURE [App::DocumentObjectGroupPython] O_element011  label="O_element : 005"  # scripted group (container) (typed FeaturePython)
  n = 1
  ref = O_element
FEATURE [App::DocumentObjectGroupPython] G4_BERYLLIUM_OXIDE  # scripted group (container) (typed FeaturePython)
  Dunit = g/cm3
  Dvalue = 3.01
  Group = -> [Be_element001,O_element011]
  conduct = 2
  density = 1
  expand = 3
  formula = G4_BERYLLIUM_OXIDE
  name = G4_BERYLLIUM_OXIDE
  specific = 4
FEATURE [App::DocumentObjectGroupPython] Bi_element001  label="Bi_element : 4"  # scripted group (container) (typed FeaturePython)
  n = 4
  ref = Bi_element
FEATURE [App::DocumentObjectGroupPython] Ge_element001  label="Ge_element : 3"  # scripted group (container) (typed FeaturePython)
  n = 3
  ref = Ge_element
FEATURE [App::DocumentObjectGroupPython] O_element012  label="O_element : 12"  # scripted group (container) (typed FeaturePython)
  n = 12
  ref = O_element
FEATURE [App::DocumentObjectGroupPython] G4_BGO  # scripted group (container) (typed FeaturePython)
  Dunit = g/cm3
  Dvalue = 7.13
  Group = -> [Bi_element001,Ge_element001,O_element012]
  conduct = 2
  density = 1
  expand = 3
  formula = G4_BGO
  name = G4_BGO
  specific = 4
FEATURE [App::DocumentObjectGroupPython] H_element014  label="H_element : 0.102"  # scripted group (container) (typed FeaturePython)
  n = 0.102
FEATURE [App::DocumentObjectGroupPython] C_element014  label="C_element : 0.110"  # scripted group (container) (typed FeaturePython)
  n = 0.11
FEATURE [App::DocumentObjectGroupPython] N_element009  label="N_element : 0.033"  # scripted group (container) (typed FeaturePython)
  n = 0.033
FEATURE [App::DocumentObjectGroupPython] O_element013  label="O_element : 0.745"  # scripted group (container) (typed FeaturePython)
  n = 0.745
FEATURE [App::DocumentObjectGroupPython] Na_element002  label="Na_element : 0.002"  # scripted group (container) (typed FeaturePython)
  n = 0.001
FEATURE [App::DocumentObjectGroupPython] P_element001  label="P_element : 0.001"  # scripted group (container) (typed FeaturePython)
  n = 0.001
FEATURE [App::DocumentObjectGroupPython] S_element003  label="S_element : 0.002"  # scripted group (container) (typed FeaturePython)
  n = 0.002
FEATURE [App::DocumentObjectGroupPython] Cl_element002  label="Cl_element : 0.003"  # scripted group (container) (typed FeaturePython)
  n = 0.003
FEATURE [App::DocumentObjectGroupPython] K_element001  label="K_element : 0.002"  # scripted group (container) (typed FeaturePython)
  n = 0.002
FEATURE [App::DocumentObjectGroupPython] Fe_element001  label="Fe_element : 0.001"  # scripted group (container) (typed FeaturePython)
  n = 0.001
FEATURE [App::DocumentObjectGroupPython] G4_BLOOD_ICRP  # scripted group (container) (typed FeaturePython)
  Dunit = g/cm3
  Dvalue = 1.06
  Group = -> [H_element014,C_element014,N_element009,O_element013,Na_element002,P_element001,S_element003,Cl_element002,K_element001,Fe_element001]
  conduct = 2
  density = 1
  expand = 3
  formula = G4_BLOOD_ICRP
  name = G4_BLOOD_ICRP
  specific = 4
FEATURE [App::DocumentObjectGroupPython] H_element015  label="H_element : 0.064"  # scripted group (container) (typed FeaturePython)
  n = 0.064
FEATURE [App::DocumentObjectGroupPython] C_element015  label="C_element : 0.278"  # scripted group (container) (typed FeaturePython)
  n = 0.278
FEATURE [App::DocumentObjectGroupPython] N_element010  label="N_element : 0.027"  # scripted group (container) (typed FeaturePython)
  n = 0.027
FEATURE [App::DocumentObjectGroupPython] O_element014  label="O_element : 0.410"  # scripted group (container) (typed FeaturePython)
  n = 0.41
FEATURE [App::DocumentObjectGroupPython] Mg_element001  label="Mg_element : 0.002"  # scripted group (container) (typed FeaturePython)
  n = 0.002
FEATURE [App::DocumentObjectGroupPython] P_element002  label="P_element : 0.070"  # scripted group (container) (typed FeaturePython)
  n = 0.07
FEATURE [App::DocumentObjectGroupPython] S_element004  label="S_element : 0.003"  # scripted group (container) (typed FeaturePython)
  n = 0.002
FEATURE [App::DocumentObjectGroupPython] Ca_element003  label="Ca_element : 0.147"  # scripted group (container) (typed FeaturePython)
  n = 0.147
FEATURE [App::DocumentObjectGroupPython] G4_BONE_COMPACT_ICRU  # scripted group (container) (typed FeaturePython)
  Dunit = g/cm3
  Dvalue = 1.85
  Group = -> [H_element015,C_element015,N_element010,O_element014,Mg_element001,P_element002,S_element004,Ca_element003]
  conduct = 2
  density = 1
  expand = 3
  formula = G4_BONE_COMPACT_ICRU
  name = G4_BONE_COMPACT_ICRU
  specific = 4
FEATURE [App::DocumentObjectGroupPython] H_element016  label="H_element : 0.034"  # scripted group (container) (typed FeaturePython)
  n = 0.034
FEATURE [App::DocumentObjectGroupPython] C_element016  label="C_element : 0.155"  # scripted group (container) (typed FeaturePython)
  n = 0.155
FEATURE [App::DocumentObjectGroupPython] N_element011  label="N_element : 0.042"  # scripted group (container) (typed FeaturePython)
  n = 0.042
FEATURE [App::DocumentObjectGroupPython] O_element015  label="O_element : 0.435"  # scripted group (container) (typed FeaturePython)
  n = 0.435
FEATURE [App::DocumentObjectGroupPython] Na_element003  label="Na_element : 0.003"  # scripted group (container) (typed FeaturePython)
  n = 0.001
FEATURE [App::DocumentObjectGroupPython] Mg_element002  label="Mg_element : 0.003"  # scripted group (container) (typed FeaturePython)
  n = 0.002
FEATURE [App::DocumentObjectGroupPython] P_element003  label="P_element : 0.103"  # scripted group (container) (typed FeaturePython)
  n = 0.103
FEATURE [App::DocumentObjectGroupPython] S_element005  label="S_element : 0.004"  # scripted group (container) (typed FeaturePython)
  n = 0.003
FEATURE [App::DocumentObjectGroupPython] Ca_element004  label="Ca_element : 0.225"  # scripted group (container) (typed FeaturePython)
  n = 0.225
FEATURE [App::DocumentObjectGroupPython] G4_BONE_CORTICAL_ICRP  # scripted group (container) (typed FeaturePython)
  Dunit = g/cm3
  Dvalue = 1.92
  Group = -> [H_element016,C_element016,N_element011,O_element015,Na_element003,Mg_element002,P_element003,S_element005,Ca_element004]
  conduct = 2
  density = 1
  expand = 3
  formula = G4_BONE_CORTICAL_ICRP
  name = G4_BONE_CORTICAL_ICRP
  specific = 4
FEATURE [App::DocumentObjectGroupPython] B_element001  label="B_element : 4"  # scripted group (container) (typed FeaturePython)
  n = 4
  ref = B_element
FEATURE [App::DocumentObjectGroupPython] C_element017  label="C_element : 1"  # scripted group (container) (typed FeaturePython)
  n = 1
  ref = C_element
FEATURE [App::DocumentObjectGroupPython] G4_BORON_CARBIDE  # scripted group (container) (typed FeaturePython)
  Dunit = g/cm3
  Dvalue = 2.52
  Group = -> [B_element001,C_element017]
  conduct = 2
  density = 1
  expand = 3
  formula = G4_BORON_CARBIDE
  name = G4_BORON_CARBIDE
  specific = 4
FEATURE [App::DocumentObjectGroupPython] B_element002  label="B_element : 2"  # scripted group (container) (typed FeaturePython)
  n = 2
  ref = B_element
FEATURE [App::DocumentObjectGroupPython] O_element016  label="O_element : 006"  # scripted group (container) (typed FeaturePython)
  n = 3
  ref = O_element
FEATURE [App::DocumentObjectGroupPython] G4_BORON_OXIDE  # scripted group (container) (typed FeaturePython)
  Dunit = g/cm3
  Dvalue = 1.812
  Group = -> [B_element002,O_element016]
  conduct = 2
  density = 1
  expand = 3
  formula = G4_BORON_OXIDE
  name = G4_BORON_OXIDE
  specific = 4
FEATURE [App::DocumentObjectGroupPython] H_element017  label="H_element : 0.107"  # scripted group (container) (typed FeaturePython)
  n = 0.107
FEATURE [App::DocumentObjectGroupPython] C_element018  label="C_element : 0.145"  # scripted group (container) (typed FeaturePython)
  n = 0.145
FEATURE [App::DocumentObjectGroupPython] N_element012  label="N_element : 0.022"  # scripted group (container) (typed FeaturePython)
  n = 0.022
FEATURE [App::DocumentObjectGroupPython] O_element017  label="O_element : 0.712"  # scripted group (container) (typed FeaturePython)
  n = 0.712
FEATURE [App::DocumentObjectGroupPython] Na_element004  label="Na_element : 0.004"  # scripted group (container) (typed FeaturePython)
  n = 0.002
FEATURE [App::DocumentObjectGroupPython] P_element004  label="P_element : 0.004"  # scripted group (container) (typed FeaturePython)
  n = 0.004
FEATURE [App::DocumentObjectGroupPython] S_element006  label="S_element : 0.005"  # scripted group (container) (typed FeaturePython)
  n = 0.002
FEATURE [App::DocumentObjectGroupPython] Cl_element003  label="Cl_element : 0.004"  # scripted group (container) (typed FeaturePython)
  n = 0.003
FEATURE [App::DocumentObjectGroupPython] K_element002  label="K_element : 0.003"  # scripted group (container) (typed FeaturePython)
  n = 0.003
FEATURE [App::DocumentObjectGroupPython] G4_BRAIN_ICRP  # scripted group (container) (typed FeaturePython)
  Dunit = g/cm3
  Dvalue = 1.04
  Group = -> [H_element017,C_element018,N_element012,O_element017,Na_element004,P_element004,S_element006,Cl_element003,K_element002]
  conduct = 2
  density = 1
  expand = 3
  formula = G4_BRAIN_ICRP
  name = G4_BRAIN_ICRP
  specific = 4
FEATURE [App::DocumentObjectGroupPython] C_element019  label="C_element : 4"  # scripted group (container) (typed FeaturePython)
  n = 4
  ref = C_element
FEATURE [App::DocumentObjectGroupPython] H_element018  label="H_element : 010"  # scripted group (container) (typed FeaturePython)
  n = 10
  ref = H_element
FEATURE [App::DocumentObjectGroupPython] G4_BUTANE  # scripted group (container) (typed FeaturePython)
  Dunit = g/cm3
  Dvalue = 0.00249343
  Group = -> [C_element019,H_element018]
  conduct = 2
  density = 1
  expand = 3
  formula = G4_BUTANE
  name = G4_BUTANE
  specific = 4
FEATURE [App::DocumentObjectGroupPython] C_element020  label="C_element : 008"  # scripted group (container) (typed FeaturePython)
  n = 4
  ref = C_element
FEATURE [App::DocumentObjectGroupPython] H_element019  label="H_element : 011"  # scripted group (container) (typed FeaturePython)
  n = 10
  ref = H_element
FEATURE [App::DocumentObjectGroupPython] O_element018  label="O_element : 007"  # scripted group (container) (typed FeaturePython)
  n = 1
  ref = O_element
FEATURE [App::DocumentObjectGroupPython] G4_N_BUTYL_ALCOHOL  label="G4_N-BUTYL_ALCOHOL"  # scripted group (container) (typed FeaturePython)
  Dunit = g/cm3
  Dvalue = 0.8098
  Group = -> [C_element020,H_element019,O_element018]
  conduct = 2
  density = 1
  expand = 3
  formula = G4_N-BUTYL_ALCOHOL
  name = G4_N-BUTYL_ALCOHOL
  specific = 4
FEATURE [App::DocumentObjectGroupPython] H_element020  label="H_element : 0.025"  # scripted group (container) (typed FeaturePython)
  n = 0.02468
FEATURE [App::DocumentObjectGroupPython] C_element021  label="C_element : 0.502"  # scripted group (container) (typed FeaturePython)
  n = 0.501611
FEATURE [App::DocumentObjectGroupPython] O_element019  label="O_element : 0.005"  # scripted group (container) (typed FeaturePython)
  n = 0.004527
FEATURE [App::DocumentObjectGroupPython] F_element004  label="F_element : 0.465"  # scripted group (container) (typed FeaturePython)
  n = 0.465209
FEATURE [App::DocumentObjectGroupPython] Si_element001  label="Si_element : 0.004"  # scripted group (container) (typed FeaturePython)
  n = 0.003973
FEATURE [App::DocumentObjectGroupPython] G4_C_552  label="G4_C-552"  # scripted group (container) (typed FeaturePython)
  Dunit = g/cm3
  Dvalue = 1.76
  Group = -> [H_element020,C_element021,O_element019,F_element004,Si_element001]
  conduct = 2
  density = 1
  expand = 3
  formula = G4_C-552
  name = G4_C-552
  specific = 4
FEATURE [App::DocumentObjectGroupPython] Cd_element001  label="Cd_element : 1"  # scripted group (container) (typed FeaturePython)
  n = 1
  ref = Cd_element
FEATURE [App::DocumentObjectGroupPython] Te_element001  label="Te_element : 1"  # scripted group (container) (typed FeaturePython)
  n = 1
  ref = Te_element
FEATURE [App::DocumentObjectGroupPython] G4_CADMIUM_TELLURIDE  # scripted group (container) (typed FeaturePython)
  Dunit = g/cm3
  Dvalue = 6.2
  Group = -> [Cd_element001,Te_element001]
  conduct = 2
  density = 1
  expand = 3
  formula = G4_CADMIUM_TELLURIDE
  name = G4_CADMIUM_TELLURIDE
  specific = 4
FEATURE [App::DocumentObjectGroupPython] Cd_element002  label="Cd_element : 002"  # scripted group (container) (typed FeaturePython)
  n = 1
  ref = Cd_element
FEATURE [App::DocumentObjectGroupPython] W_element001  label="W_element : 1"  # scripted group (container) (typed FeaturePython)
  n = 1
  ref = W_element
FEATURE [App::DocumentObjectGroupPython] O_element020  label="O_element : 008"  # scripted group (container) (typed FeaturePython)
  n = 4
  ref = O_element
FEATURE [App::DocumentObjectGroupPython] G4_CADMIUM_TUNGSTATE  # scripted group (container) (typed FeaturePython)
  Dunit = g/cm3
  Dvalue = 7.9
  Group = -> [Cd_element002,W_element001,O_element020]
  conduct = 2
  density = 1
  expand = 3
  formula = G4_CADMIUM_TUNGSTATE
  name = G4_CADMIUM_TUNGSTATE
  specific = 4
FEATURE [App::DocumentObjectGroupPython] Ca_element005  label="Ca_element : 1"  # scripted group (container) (typed FeaturePython)
  n = 1
  ref = Ca_element
FEATURE [App::DocumentObjectGroupPython] C_element022  label="C_element : 009"  # scripted group (container) (typed FeaturePython)
  n = 1
  ref = C_element
FEATURE [App::DocumentObjectGroupPython] O_element021  label="O_element : 009"  # scripted group (container) (typed FeaturePython)
  n = 3
  ref = O_element
FEATURE [App::DocumentObjectGroupPython] G4_CALCIUM_CARBONATE  # scripted group (container) (typed FeaturePython)
  Dunit = g/cm3
  Dvalue = 2.8
  Group = -> [Ca_element005,C_element022,O_element021]
  conduct = 2
  density = 1
  expand = 3
  formula = G4_CALCIUM_CARBONATE
  name = G4_CALCIUM_CARBONATE
  specific = 4
FEATURE [App::DocumentObjectGroupPython] Ca_element006  label="Ca_element : 002"  # scripted group (container) (typed FeaturePython)
  n = 1
  ref = Ca_element
FEATURE [App::DocumentObjectGroupPython] F_element005  label="F_element : 003"  # scripted group (container) (typed FeaturePython)
  n = 2
  ref = F_element
FEATURE [App::DocumentObjectGroupPython] G4_CALCIUM_FLUORIDE  # scripted group (container) (typed FeaturePython)
  Dunit = g/cm3
  Dvalue = 3.18
  Group = -> [Ca_element006,F_element005]
  conduct = 2
  density = 1
  expand = 3
  formula = G4_CALCIUM_FLUORIDE
  name = G4_CALCIUM_FLUORIDE
  specific = 4
FEATURE [App::DocumentObjectGroupPython] Ca_element007  label="Ca_element : 003"  # scripted group (container) (typed FeaturePython)
  n = 1
  ref = Ca_element
FEATURE [App::DocumentObjectGroupPython] O_element022  label="O_element : 010"  # scripted group (container) (typed FeaturePython)
  n = 1
  ref = O_element
FEATURE [App::DocumentObjectGroupPython] G4_CALCIUM_OXIDE  # scripted group (container) (typed FeaturePython)
  Dunit = g/cm3
  Dvalue = 3.3
  Group = -> [Ca_element007,O_element022]
  conduct = 2
  density = 1
  expand = 3
  formula = G4_CALCIUM_OXIDE
  name = G4_CALCIUM_OXIDE
  specific = 4
FEATURE [App::DocumentObjectGroupPython] Ca_element008  label="Ca_element : 004"  # scripted group (container) (typed FeaturePython)
  n = 1
  ref = Ca_element
FEATURE [App::DocumentObjectGroupPython] S_element007  label="S_element : 002"  # scripted group (container) (typed FeaturePython)
  n = 1
  ref = S_element
FEATURE [App::DocumentObjectGroupPython] O_element023  label="O_element : 011"  # scripted group (container) (typed FeaturePython)
  n = 4
  ref = O_element
FEATURE [App::DocumentObjectGroupPython] G4_CALCIUM_SULFATE  # scripted group (container) (typed FeaturePython)
  Dunit = g/cm3
  Dvalue = 2.96
  Group = -> [Ca_element008,S_element007,O_element023]
  conduct = 2
  density = 1
  expand = 3
  formula = G4_CALCIUM_SULFATE
  name = G4_CALCIUM_SULFATE
  specific = 4
FEATURE [App::DocumentObjectGroupPython] Ca_element009  label="Ca_element : 005"  # scripted group (container) (typed FeaturePython)
  n = 1
  ref = Ca_element
FEATURE [App::DocumentObjectGroupPython] W_element002  label="W_element : 002"  # scripted group (container) (typed FeaturePython)
  n = 1
  ref = W_element
FEATURE [App::DocumentObjectGroupPython] O_element024  label="O_element : 012"  # scripted group (container) (typed FeaturePython)
  n = 4
  ref = O_element
FEATURE [App::DocumentObjectGroupPython] G4_CALCIUM_TUNGSTATE  # scripted group (container) (typed FeaturePython)
  Dunit = g/cm3
  Dvalue = 6.062
  Group = -> [Ca_element009,W_element002,O_element024]
  conduct = 2
  density = 1
  expand = 3
  formula = G4_CALCIUM_TUNGSTATE
  name = G4_CALCIUM_TUNGSTATE
  specific = 4
FEATURE [App::DocumentObjectGroupPython] C_element023  label="C_element : 010"  # scripted group (container) (typed FeaturePython)
  n = 1
  ref = C_element
FEATURE [App::DocumentObjectGroupPython] O_element025  label="O_element : 013"  # scripted group (container) (typed FeaturePython)
  n = 2
  ref = O_element
FEATURE [App::DocumentObjectGroupPython] G4_CARBON_DIOXIDE  # scripted group (container) (typed FeaturePython)
  Dunit = g/cm3
  Dvalue = 0.00184212
  Group = -> [C_element023,O_element025]
  conduct = 2
  density = 1
  expand = 3
  formula = G4_CARBON_DIOXIDE
  name = G4_CARBON_DIOXIDE
  specific = 4
FEATURE [App::DocumentObjectGroupPython] C_element024  label="C_element : 011"  # scripted group (container) (typed FeaturePython)
  n = 1
  ref = C_element
FEATURE [App::DocumentObjectGroupPython] Cl_element004  label="Cl_element : 4"  # scripted group (container) (typed FeaturePython)
  n = 4
  ref = Cl_element
FEATURE [App::DocumentObjectGroupPython] G4_CARBON_TETRACHLORIDE  # scripted group (container) (typed FeaturePython)
  Dunit = g/cm3
  Dvalue = 1.594
  Group = -> [C_element024,Cl_element004]
  conduct = 2
  density = 1
  expand = 3
  formula = G4_CARBON_TETRACHLORIDE
  name = G4_CARBON_TETRACHLORIDE
  specific = 4
FEATURE [App::DocumentObjectGroupPython] C_element025  label="C_element : 012"  # scripted group (container) (typed FeaturePython)
  n = 6
  ref = C_element
FEATURE [App::DocumentObjectGroupPython] H_element021  label="H_element : 012"  # scripted group (container) (typed FeaturePython)
  n = 10
  ref = H_element
FEATURE [App::DocumentObjectGroupPython] O_element026  label="O_element : 5"  # scripted group (container) (typed FeaturePython)
  n = 5
  ref = O_element
FEATURE [App::DocumentObjectGroupPython] G4_CELLULOSE_CELLOPHANE  # scripted group (container) (typed FeaturePython)
  Dunit = g/cm3
  Dvalue = 1.42
  Group = -> [C_element025,H_element021,O_element026]
  conduct = 2
  density = 1
  expand = 3
  formula = G4_CELLULOSE_CELLOPHANE
  name = G4_CELLULOSE_CELLOPHANE
  specific = 4
FEATURE [App::DocumentObjectGroupPython] H_element022  label="H_element : 0.067"  # scripted group (container) (typed FeaturePython)
  n = 0.067125
FEATURE [App::DocumentObjectGroupPython] C_element026  label="C_element : 0.545"  # scripted group (container) (typed FeaturePython)
  n = 0.545403
FEATURE [App::DocumentObjectGroupPython] O_element027  label="O_element : 0.387"  # scripted group (container) (typed FeaturePython)
  n = 0.387472
FEATURE [App::DocumentObjectGroupPython] G4_CELLULOSE_BUTYRATE  # scripted group (container) (typed FeaturePython)
  Dunit = g/cm3
  Dvalue = 1.2
  Group = -> [H_element022,C_element026,O_element027]
  conduct = 2
  density = 1
  expand = 3
  formula = G4_CELLULOSE_BUTYRATE
  name = G4_CELLULOSE_BUTYRATE
  specific = 4
FEATURE [App::DocumentObjectGroupPython] H_element023  label="H_element : 0.029"  # scripted group (container) (typed FeaturePython)
  n = 0.029216
FEATURE [App::DocumentObjectGroupPython] C_element027  label="C_element : 0.271"  # scripted group (container) (typed FeaturePython)
  n = 0.271296
FEATURE [App::DocumentObjectGroupPython] N_element013  label="N_element : 0.121"  # scripted group (container) (typed FeaturePython)
  n = 0.121276
FEATURE [App::DocumentObjectGroupPython] O_element028  label="O_element : 0.578"  # scripted group (container) (typed FeaturePython)
  n = 0.578212
FEATURE [App::DocumentObjectGroupPython] G4_CELLULOSE_NITRATE  # scripted group (container) (typed FeaturePython)
  Dunit = g/cm3
  Dvalue = 1.49
  Group = -> [H_element023,C_element027,N_element013,O_element028]
  conduct = 2
  density = 1
  expand = 3
  formula = G4_CELLULOSE_NITRATE
  name = G4_CELLULOSE_NITRATE
  specific = 4
FEATURE [App::DocumentObjectGroupPython] H_element024  label="H_element : 0.108"  # scripted group (container) (typed FeaturePython)
  n = 0.107596
FEATURE [App::DocumentObjectGroupPython] N_element014  label="N_element : 0.001"  # scripted group (container) (typed FeaturePython)
  n = 0.0008
FEATURE [App::DocumentObjectGroupPython] O_element029  label="O_element : 0.875"  # scripted group (container) (typed FeaturePython)
  n = 0.874976
FEATURE [App::DocumentObjectGroupPython] S_element008  label="S_element : 0.015"  # scripted group (container) (typed FeaturePython)
  n = 0.014627
FEATURE [App::DocumentObjectGroupPython] Ce_element001  label="Ce_element : 0.002"  # scripted group (container) (typed FeaturePython)
  n = 0.002001
FEATURE [App::DocumentObjectGroupPython] G4_CERIC_SULFATE  # scripted group (container) (typed FeaturePython)
  Dunit = g/cm3
  Dvalue = 1.03
  Group = -> [H_element024,N_element014,O_element029,S_element008,Ce_element001]
  conduct = 2
  density = 1
  expand = 3
  formula = G4_CERIC_SULFATE
  name = G4_CERIC_SULFATE
  specific = 4
FEATURE [App::DocumentObjectGroupPython] Cs_element001  label="Cs_element : 1"  # scripted group (container) (typed FeaturePython)
  n = 1
  ref = Cs_element
FEATURE [App::DocumentObjectGroupPython] F_element006  label="F_element : 1"  # scripted group (container) (typed FeaturePython)
  n = 1
  ref = F_element
FEATURE [App::DocumentObjectGroupPython] G4_CESIUM_FLUORIDE  # scripted group (container) (typed FeaturePython)
  Dunit = g/cm3
  Dvalue = 4.115
  Group = -> [Cs_element001,F_element006]
  conduct = 2
  density = 1
  expand = 3
  formula = G4_CESIUM_FLUORIDE
  name = G4_CESIUM_FLUORIDE
  specific = 4
FEATURE [App::DocumentObjectGroupPython] Cs_element002  label="Cs_element : 002"  # scripted group (container) (typed FeaturePython)
  n = 1
  ref = Cs_element
FEATURE [App::DocumentObjectGroupPython] I_element001  label="I_element : 1"  # scripted group (container) (typed FeaturePython)
  n = 1
  ref = I_element
FEATURE [App::DocumentObjectGroupPython] G4_CESIUM_IODIDE  # scripted group (container) (typed FeaturePython)
  Dunit = g/cm3
  Dvalue = 4.51
  Group = -> [Cs_element002,I_element001]
  conduct = 2
  density = 1
  expand = 3
  formula = G4_CESIUM_IODIDE
  name = G4_CESIUM_IODIDE
  specific = 4
FEATURE [App::DocumentObjectGroupPython] C_element028  label="C_element : 013"  # scripted group (container) (typed FeaturePython)
  n = 6
  ref = C_element
FEATURE [App::DocumentObjectGroupPython] H_element025  label="H_element : 013"  # scripted group (container) (typed FeaturePython)
  n = 5
  ref = H_element
FEATURE [App::DocumentObjectGroupPython] Cl_element005  label="Cl_element : 1"  # scripted group (container) (typed FeaturePython)
  n = 1
  ref = Cl_element
FEATURE [App::DocumentObjectGroupPython] G4_CHLOROBENZENE  # scripted group (container) (typed FeaturePython)
  Dunit = g/cm3
  Dvalue = 1.1058
  Group = -> [C_element028,H_element025,Cl_element005]
  conduct = 2
  density = 1
  expand = 3
  formula = G4_CHLOROBENZENE
  name = G4_CHLOROBENZENE
  specific = 4
FEATURE [App::DocumentObjectGroupPython] C_element029  label="C_element : 014"  # scripted group (container) (typed FeaturePython)
  n = 1
  ref = C_element
FEATURE [App::DocumentObjectGroupPython] H_element026  label="H_element : 1"  # scripted group (container) (typed FeaturePython)
  n = 1
  ref = H_element
FEATURE [App::DocumentObjectGroupPython] Cl_element006  label="Cl_element : 3"  # scripted group (container) (typed FeaturePython)
  n = 3
  ref = Cl_element
FEATURE [App::DocumentObjectGroupPython] G4_CHLOROFORM  # scripted group (container) (typed FeaturePython)
  Dunit = g/cm3
  Dvalue = 1.4832
  Group = -> [C_element029,H_element026,Cl_element006]
  conduct = 2
  density = 1
  expand = 3
  formula = G4_CHLOROFORM
  name = G4_CHLOROFORM
  specific = 4
FEATURE [App::DocumentObjectGroupPython] H_element027  label="H_element : 0.010"  # scripted group (container) (typed FeaturePython)
  n = 0.01
FEATURE [App::DocumentObjectGroupPython] C_element030  label="C_element : 0.001"  # scripted group (container) (typed FeaturePython)
  n = 0.001
FEATURE [App::DocumentObjectGroupPython] O_element030  label="O_element : 0.529"  # scripted group (container) (typed FeaturePython)
  n = 0.529107
FEATURE [App::DocumentObjectGroupPython] Na_element005  label="Na_element : 0.016"  # scripted group (container) (typed FeaturePython)
  n = 0.016
FEATURE [App::DocumentObjectGroupPython] Mg_element003  label="Mg_element : 0.004"  # scripted group (container) (typed FeaturePython)
  n = 0.002
FEATURE [App::DocumentObjectGroupPython] Al_element002  label="Al_element : 0.034"  # scripted group (container) (typed FeaturePython)
  n = 0.033872
FEATURE [App::DocumentObjectGroupPython] Si_element002  label="Si_element : 0.337"  # scripted group (container) (typed FeaturePython)
  n = 0.337021
FEATURE [App::DocumentObjectGroupPython] K_element003  label="K_element : 0.013"  # scripted group (container) (typed FeaturePython)
  n = 0.013
FEATURE [App::DocumentObjectGroupPython] Ca_element010  label="Ca_element : 0.044"  # scripted group (container) (typed FeaturePython)
  n = 0.044
FEATURE [App::DocumentObjectGroupPython] Fe_element002  label="Fe_element : 0.014"  # scripted group (container) (typed FeaturePython)
  n = 0.014
FEATURE [App::DocumentObjectGroupPython] G4_CONCRETE  # scripted group (container) (typed FeaturePython)
  Dunit = g/cm3
  Dvalue = 2.3
  Group = -> [H_element027,C_element030,O_element030,Na_element005,Mg_element003,Al_element002,Si_element002,K_element003,Ca_element010,Fe_element002]
  conduct = 2
  density = 1
  expand = 3
  formula = G4_CONCRETE
  name = G4_CONCRETE
  specific = 4
FEATURE [App::DocumentObjectGroupPython] C_element031  label="C_element : 015"  # scripted group (container) (typed FeaturePython)
  n = 6
  ref = C_element
FEATURE [App::DocumentObjectGroupPython] H_element028  label="H_element : 12"  # scripted group (container) (typed FeaturePython)
  n = 12
  ref = H_element
FEATURE [App::DocumentObjectGroupPython] G4_CYCLOHEXANE  # scripted group (container) (typed FeaturePython)
  Dunit = g/cm3
  Dvalue = 0.779
  Group = -> [C_element031,H_element028]
  conduct = 2
  density = 1
  expand = 3
  formula = G4_CYCLOHEXANE
  name = G4_CYCLOHEXANE
  specific = 4
FEATURE [App::DocumentObjectGroupPython] C_element032  label="C_element : 016"  # scripted group (container) (typed FeaturePython)
  n = 6
  ref = C_element
FEATURE [App::DocumentObjectGroupPython] H_element029  label="H_element : 4"  # scripted group (container) (typed FeaturePython)
  n = 4
  ref = H_element
FEATURE [App::DocumentObjectGroupPython] Cl_element007  label="Cl_element : 2"  # scripted group (container) (typed FeaturePython)
  n = 2
  ref = Cl_element
FEATURE [App::DocumentObjectGroupPython] G4_1_2_DICHLOROBENZENE  label="G4_1.2-DICHLOROBENZENE"  # scripted group (container) (typed FeaturePython)
  Dunit = g/cm3
  Dvalue = 1.3048
  Group = -> [C_element032,H_element029,Cl_element007]
  conduct = 2
  density = 1
  expand = 3
  formula = G4_1.2-DICHLOROBENZENE
  name = G4_1.2-DICHLOROBENZENE
  specific = 4
FEATURE [App::DocumentObjectGroupPython] C_element033  label="C_element : 017"  # scripted group (container) (typed FeaturePython)
  n = 4
  ref = C_element
FEATURE [App::DocumentObjectGroupPython] H_element030  label="H_element : 8"  # scripted group (container) (typed FeaturePython)
  n = 8
  ref = H_element
FEATURE [App::DocumentObjectGroupPython] O_element031  label="O_element : 014"  # scripted group (container) (typed FeaturePython)
  n = 1
  ref = O_element
FEATURE [App::DocumentObjectGroupPython] Cl_element008  label="Cl_element : 005"  # scripted group (container) (typed FeaturePython)
  n = 2
  ref = Cl_element
FEATURE [App::DocumentObjectGroupPython] G4_DICHLORODIETHYL_ETHER  # scripted group (container) (typed FeaturePython)
  Dunit = g/cm3
  Dvalue = 1.2199
  Group = -> [C_element033,H_element030,O_element031,Cl_element008]
  conduct = 2
  density = 1
  expand = 3
  formula = G4_DICHLORODIETHYL_ETHER
  name = G4_DICHLORODIETHYL_ETHER
  specific = 4
FEATURE [App::DocumentObjectGroupPython] C_element034  label="C_element : 018"  # scripted group (container) (typed FeaturePython)
  n = 2
  ref = C_element
FEATURE [App::DocumentObjectGroupPython] H_element031  label="H_element : 014"  # scripted group (container) (typed FeaturePython)
  n = 4
  ref = H_element
FEATURE [App::DocumentObjectGroupPython] Cl_element009  label="Cl_element : 006"  # scripted group (container) (typed FeaturePython)
  n = 2
  ref = Cl_element
FEATURE [App::DocumentObjectGroupPython] G4_1_2_DICHLOROETHANE  label="G4_1.2-DICHLOROETHANE"  # scripted group (container) (typed FeaturePython)
  Dunit = g/cm3
  Dvalue = 1.2351
  Group = -> [C_element034,H_element031,Cl_element009]
  conduct = 2
  density = 1
  expand = 3
  formula = G4_1.2-DICHLOROETHANE
  name = G4_1.2-DICHLOROETHANE
  specific = 4
FEATURE [App::DocumentObjectGroupPython] C_element035  label="C_element : 019"  # scripted group (container) (typed FeaturePython)
  n = 4
  ref = C_element
FEATURE [App::DocumentObjectGroupPython] H_element032  label="H_element : 015"  # scripted group (container) (typed FeaturePython)
  n = 10
  ref = H_element
FEATURE [App::DocumentObjectGroupPython] O_element032  label="O_element : 015"  # scripted group (container) (typed FeaturePython)
  n = 1
  ref = O_element
FEATURE [App::DocumentObjectGroupPython] G4_DIETHYL_ETHER  # scripted group (container) (typed FeaturePython)
  Dunit = g/cm3
  Dvalue = 0.71378
  Group = -> [C_element035,H_element032,O_element032]
  conduct = 2
  density = 1
  expand = 3
  formula = G4_DIETHYL_ETHER
  name = G4_DIETHYL_ETHER
  specific = 4
FEATURE [App::DocumentObjectGroupPython] C_element036  label="C_element : 020"  # scripted group (container) (typed FeaturePython)
  n = 3
  ref = C_element
FEATURE [App::DocumentObjectGroupPython] H_element033  label="H_element : 016"  # scripted group (container) (typed FeaturePython)
  n = 7
  ref = H_element
FEATURE [App::DocumentObjectGroupPython] N_element015  label="N_element : 008"  # scripted group (container) (typed FeaturePython)
  n = 1
  ref = N_element
FEATURE [App::DocumentObjectGroupPython] O_element033  label="O_element : 016"  # scripted group (container) (typed FeaturePython)
  n = 1
  ref = O_element
FEATURE [App::DocumentObjectGroupPython] G4_N_N_DIMETHYL_FORMAMIDE  label="G4_N.N-DIMETHYL_FORMAMIDE"  # scripted group (container) (typed FeaturePython)
  Dunit = g/cm3
  Dvalue = 0.9487
  Group = -> [C_element036,H_element033,N_element015,O_element033]
  conduct = 2
  density = 1
  expand = 3
  formula = G4_N.N-DIMETHYL_FORMAMIDE
  name = G4_N.N-DIMETHYL_FORMAMIDE
  specific = 4
FEATURE [App::DocumentObjectGroupPython] C_element037  label="C_element : 021"  # scripted group (container) (typed FeaturePython)
  n = 2
  ref = C_element
FEATURE [App::DocumentObjectGroupPython] H_element034  label="H_element : 017"  # scripted group (container) (typed FeaturePython)
  n = 6
  ref = H_element
FEATURE [App::DocumentObjectGroupPython] O_element034  label="O_element : 017"  # scripted group (container) (typed FeaturePython)
  n = 1
  ref = O_element
FEATURE [App::DocumentObjectGroupPython] S_element009  label="S_element : 003"  # scripted group (container) (typed FeaturePython)
  n = 1
  ref = S_element
FEATURE [App::DocumentObjectGroupPython] G4_DIMETHYL_SULFOXIDE  # scripted group (container) (typed FeaturePython)
  Dunit = g/cm3
  Dvalue = 1.1014
  Group = -> [C_element037,H_element034,O_element034,S_element009]
  conduct = 2
  density = 1
  expand = 3
  formula = G4_DIMETHYL_SULFOXIDE
  name = G4_DIMETHYL_SULFOXIDE
  specific = 4
FEATURE [App::DocumentObjectGroupPython] C_element038  label="C_element : 022"  # scripted group (container) (typed FeaturePython)
  n = 2
  ref = C_element
FEATURE [App::DocumentObjectGroupPython] H_element035  label="H_element : 018"  # scripted group (container) (typed FeaturePython)
  n = 6
  ref = H_element
FEATURE [App::DocumentObjectGroupPython] G4_ETHANE  # scripted group (container) (typed FeaturePython)
  Dunit = g/cm3
  Dvalue = 0.00125324
  Group = -> [C_element038,H_element035]
  conduct = 2
  density = 1
  expand = 3
  formula = G4_ETHANE
  name = G4_ETHANE
  specific = 4
FEATURE [App::DocumentObjectGroupPython] C_element039  label="C_element : 023"  # scripted group (container) (typed FeaturePython)
  n = 2
  ref = C_element
FEATURE [App::DocumentObjectGroupPython] H_element036  label="H_element : 019"  # scripted group (container) (typed FeaturePython)
  n = 6
  ref = H_element
FEATURE [App::DocumentObjectGroupPython] O_element035  label="O_element : 018"  # scripted group (container) (typed FeaturePython)
  n = 1
  ref = O_element
FEATURE [App::DocumentObjectGroupPython] G4_ETHYL_ALCOHOL  # scripted group (container) (typed FeaturePython)
  Dunit = g/cm3
  Dvalue = 0.7893
  Group = -> [C_element039,H_element036,O_element035]
  conduct = 2
  density = 1
  expand = 3
  formula = G4_ETHYL_ALCOHOL
  name = G4_ETHYL_ALCOHOL
  specific = 4
FEATURE [App::DocumentObjectGroupPython] H_element037  label="H_element : 0.090"  # scripted group (container) (typed FeaturePython)
  n = 0.090027
FEATURE [App::DocumentObjectGroupPython] C_element040  label="C_element : 0.585"  # scripted group (container) (typed FeaturePython)
  n = 0.585182
FEATURE [App::DocumentObjectGroupPython] O_element036  label="O_element : 0.325"  # scripted group (container) (typed FeaturePython)
  n = 0.324791
FEATURE [App::DocumentObjectGroupPython] G4_ETHYL_CELLULOSE  # scripted group (container) (typed FeaturePython)
  Dunit = g/cm3
  Dvalue = 1.13
  Group = -> [H_element037,C_element040,O_element036]
  conduct = 2
  density = 1
  expand = 3
  formula = G4_ETHYL_CELLULOSE
  name = G4_ETHYL_CELLULOSE
  specific = 4
FEATURE [App::DocumentObjectGroupPython] C_element041  label="C_element : 024"  # scripted group (container) (typed FeaturePython)
  n = 2
  ref = C_element
FEATURE [App::DocumentObjectGroupPython] H_element038  label="H_element : 020"  # scripted group (container) (typed FeaturePython)
  n = 4
  ref = H_element
FEATURE [App::DocumentObjectGroupPython] G4_ETHYLENE  # scripted group (container) (typed FeaturePython)
  Dunit = g/cm3
  Dvalue = 0.00117497
  Group = -> [C_element041,H_element038]
  conduct = 2
  density = 1
  expand = 3
  formula = G4_ETHYLENE
  name = G4_ETHYLENE
  specific = 4
FEATURE [App::DocumentObjectGroupPython] H_element039  label="H_element : 0.096"  # scripted group (container) (typed FeaturePython)
  n = 0.096
FEATURE [App::DocumentObjectGroupPython] C_element042  label="C_element : 0.195"  # scripted group (container) (typed FeaturePython)
  n = 0.195
FEATURE [App::DocumentObjectGroupPython] N_element016  label="N_element : 0.057"  # scripted group (container) (typed FeaturePython)
  n = 0.057
FEATURE [App::DocumentObjectGroupPython] O_element037  label="O_element : 0.646"  # scripted group (container) (typed FeaturePython)
  n = 0.646
FEATURE [App::DocumentObjectGroupPython] Na_element006  label="Na_element : 0.017"  # scripted group (container) (typed FeaturePython)
  n = 0.001
FEATURE [App::DocumentObjectGroupPython] P_element005  label="P_element : 0.104"  # scripted group (container) (typed FeaturePython)
  n = 0.001
FEATURE [App::DocumentObjectGroupPython] S_element010  label="S_element : 0.016"  # scripted group (container) (typed FeaturePython)
  n = 0.003
FEATURE [App::DocumentObjectGroupPython] Cl_element010  label="Cl_element : 0.005"  # scripted group (container) (typed FeaturePython)
  n = 0.001
FEATURE [App::DocumentObjectGroupPython] G4_EYE_LENS_ICRP  # scripted group (container) (typed FeaturePython)
  Dunit = g/cm3
  Dvalue = 1.07
  Group = -> [H_element039,C_element042,N_element016,O_element037,Na_element006,P_element005,S_element010,Cl_element010]
  conduct = 2
  density = 1
  expand = 3
  formula = G4_EYE_LENS_ICRP
  name = G4_EYE_LENS_ICRP
  specific = 4
FEATURE [App::DocumentObjectGroupPython] Fe_element003  label="Fe_element : 2"  # scripted group (container) (typed FeaturePython)
  n = 2
  ref = Fe_element
FEATURE [App::DocumentObjectGroupPython] O_element038  label="O_element : 019"  # scripted group (container) (typed FeaturePython)
  n = 3
  ref = O_element
FEATURE [App::DocumentObjectGroupPython] G4_FERRIC_OXIDE  # scripted group (container) (typed FeaturePython)
  Dunit = g/cm3
  Dvalue = 5.2
  Group = -> [Fe_element003,O_element038]
  conduct = 2
  density = 1
  expand = 3
  formula = G4_FERRIC_OXIDE
  name = G4_FERRIC_OXIDE
  specific = 4
FEATURE [App::DocumentObjectGroupPython] Fe_element004  label="Fe_element : 1"  # scripted group (container) (typed FeaturePython)
  n = 1
  ref = Fe_element
FEATURE [App::DocumentObjectGroupPython] B_element003  label="B_element : 1"  # scripted group (container) (typed FeaturePython)
  n = 1
  ref = B_element
FEATURE [App::DocumentObjectGroupPython] G4_FERROBORIDE  # scripted group (container) (typed FeaturePython)
  Dunit = g/cm3
  Dvalue = 7.15
  Group = -> [Fe_element004,B_element003]
  conduct = 2
  density = 1
  expand = 3
  formula = G4_FERROBORIDE
  name = G4_FERROBORIDE
  specific = 4
FEATURE [App::DocumentObjectGroupPython] Fe_element005  label="Fe_element : 003"  # scripted group (container) (typed FeaturePython)
  n = 1
  ref = Fe_element
FEATURE [App::DocumentObjectGroupPython] O_element039  label="O_element : 020"  # scripted group (container) (typed FeaturePython)
  n = 1
  ref = O_element
FEATURE [App::DocumentObjectGroupPython] G4_FERROUS_OXIDE  # scripted group (container) (typed FeaturePython)
  Dunit = g/cm3
  Dvalue = 5.7
  Group = -> [Fe_element005,O_element039]
  conduct = 2
  density = 1
  expand = 3
  formula = G4_FERROUS_OXIDE
  name = G4_FERROUS_OXIDE
  specific = 4
FEATURE [App::DocumentObjectGroupPython] H_element040  label="H_element : 0.115"  # scripted group (container) (typed FeaturePython)
  n = 0.108259
FEATURE [App::DocumentObjectGroupPython] N_element017  label="N_element : 0.000"  # scripted group (container) (typed FeaturePython)
  n = 2.7e-05
FEATURE [App::DocumentObjectGroupPython] O_element040  label="O_element : 0.879"  # scripted group (container) (typed FeaturePython)
  n = 0.878636
FEATURE [App::DocumentObjectGroupPython] Na_element007  label="Na_element : 0.000"  # scripted group (container) (typed FeaturePython)
  n = 2.2e-05
FEATURE [App::DocumentObjectGroupPython] S_element011  label="S_element : 0.013"  # scripted group (container) (typed FeaturePython)
  n = 0.012968
FEATURE [App::DocumentObjectGroupPython] Cl_element011  label="Cl_element : 0.000"  # scripted group (container) (typed FeaturePython)
  n = 3.4e-05
FEATURE [App::DocumentObjectGroupPython] Fe_element006  label="Fe_element : 0.000"  # scripted group (container) (typed FeaturePython)
  n = 5.4e-05
FEATURE [App::DocumentObjectGroupPython] G4_FERROUS_SULFATE  # scripted group (container) (typed FeaturePython)
  Dunit = g/cm3
  Dvalue = 1.024
  Group = -> [H_element040,N_element017,O_element040,Na_element007,S_element011,Cl_element011,Fe_element006]
  conduct = 2
  density = 1
  expand = 3
  formula = G4_FERROUS_SULFATE
  name = G4_FERROUS_SULFATE
  specific = 4
FEATURE [App::DocumentObjectGroupPython] C_element043  label="C_element : 0.099"  # scripted group (container) (typed FeaturePython)
  n = 0.099335
FEATURE [App::DocumentObjectGroupPython] F_element007  label="F_element : 0.314"  # scripted group (container) (typed FeaturePython)
  n = 0.314247
FEATURE [App::DocumentObjectGroupPython] Cl_element012  label="Cl_element : 0.586"  # scripted group (container) (typed FeaturePython)
  n = 0.586418
FEATURE [App::DocumentObjectGroupPython] G4_FREON_12  label="G4_FREON-12"  # scripted group (container) (typed FeaturePython)
  Dunit = g/cm3
  Dvalue = 1.12
  Group = -> [C_element043,F_element007,Cl_element012]
  conduct = 2
  density = 1
  expand = 3
  formula = G4_FREON-12
  name = G4_FREON-12
  specific = 4
FEATURE [App::DocumentObjectGroupPython] C_element044  label="C_element : 0.057"  # scripted group (container) (typed FeaturePython)
  n = 0.057245
FEATURE [App::DocumentObjectGroupPython] F_element008  label="F_element : 0.181"  # scripted group (container) (typed FeaturePython)
  n = 0.181096
FEATURE [App::DocumentObjectGroupPython] Br_element001  label="Br_element : 0.762"  # scripted group (container) (typed FeaturePython)
  n = 0.761659
FEATURE [App::DocumentObjectGroupPython] G4_FREON_12B2  label="G4_FREON-12B2"  # scripted group (container) (typed FeaturePython)
  Dunit = g/cm3
  Dvalue = 1.8
  Group = -> [C_element044,F_element008,Br_element001]
  conduct = 2
  density = 1
  expand = 3
  formula = G4_FREON-12B2
  name = G4_FREON-12B2
  specific = 4
FEATURE [App::DocumentObjectGroupPython] C_element045  label="C_element : 0.115"  # scripted group (container) (typed FeaturePython)
  n = 0.114983
FEATURE [App::DocumentObjectGroupPython] F_element009  label="F_element : 0.546"  # scripted group (container) (typed FeaturePython)
  n = 0.545621
FEATURE [App::DocumentObjectGroupPython] Cl_element013  label="Cl_element : 0.339"  # scripted group (container) (typed FeaturePython)
  n = 0.339396
FEATURE [App::DocumentObjectGroupPython] G4_FREON_13  label="G4_FREON-13"  # scripted group (container) (typed FeaturePython)
  Dunit = g/cm3
  Dvalue = 0.95
  Group = -> [C_element045,F_element009,Cl_element013]
  conduct = 2
  density = 1
  expand = 3
  formula = G4_FREON-13
  name = G4_FREON-13
  specific = 4
FEATURE [App::DocumentObjectGroupPython] C_element046  label="C_element : 025"  # scripted group (container) (typed FeaturePython)
  n = 1
  ref = C_element
FEATURE [App::DocumentObjectGroupPython] F_element010  label="F_element : 3"  # scripted group (container) (typed FeaturePython)
  n = 3
  ref = F_element
FEATURE [App::DocumentObjectGroupPython] Br_element002  label="Br_element : 1"  # scripted group (container) (typed FeaturePython)
  n = 1
  ref = Br_element
FEATURE [App::DocumentObjectGroupPython] G4_FREON_13B1  label="G4_FREON-13B1"  # scripted group (container) (typed FeaturePython)
  Dunit = g/cm3
  Dvalue = 1.5
  Group = -> [C_element046,F_element010,Br_element002]
  conduct = 2
  density = 1
  expand = 3
  formula = G4_FREON-13B1
  name = G4_FREON-13B1
  specific = 4
FEATURE [App::DocumentObjectGroupPython] C_element047  label="C_element : 0.061"  # scripted group (container) (typed FeaturePython)
  n = 0.061309
FEATURE [App::DocumentObjectGroupPython] F_element011  label="F_element : 0.291"  # scripted group (container) (typed FeaturePython)
  n = 0.290924
FEATURE [App::DocumentObjectGroupPython] I_element002  label="I_element : 0.648"  # scripted group (container) (typed FeaturePython)
  n = 0.647767
FEATURE [App::DocumentObjectGroupPython] G4_FREON_13I1  label="G4_FREON-13I1"  # scripted group (container) (typed FeaturePython)
  Dunit = g/cm3
  Dvalue = 1.8
  Group = -> [C_element047,F_element011,I_element002]
  conduct = 2
  density = 1
  expand = 3
  formula = G4_FREON-13I1
  name = G4_FREON-13I1
  specific = 4
FEATURE [App::DocumentObjectGroupPython] Gd_element001  label="Gd_element : 2"  # scripted group (container) (typed FeaturePython)
  n = 2
  ref = Gd_element
FEATURE [App::DocumentObjectGroupPython] O_element041  label="O_element : 021"  # scripted group (container) (typed FeaturePython)
  n = 2
  ref = O_element
FEATURE [App::DocumentObjectGroupPython] S_element012  label="S_element : 004"  # scripted group (container) (typed FeaturePython)
  n = 1
  ref = S_element
FEATURE [App::DocumentObjectGroupPython] G4_GADOLINIUM_OXYSULFIDE  # scripted group (container) (typed FeaturePython)
  Dunit = g/cm3
  Dvalue = 7.44
  Group = -> [Gd_element001,O_element041,S_element012]
  conduct = 2
  density = 1
  expand = 3
  formula = G4_GADOLINIUM_OXYSULFIDE
  name = G4_GADOLINIUM_OXYSULFIDE
  specific = 4
FEATURE [App::DocumentObjectGroupPython] Ga_element001  label="Ga_element : 1"  # scripted group (container) (typed FeaturePython)
  n = 1
  ref = Ga_element
FEATURE [App::DocumentObjectGroupPython] As_element001  label="As_element : 1"  # scripted group (container) (typed FeaturePython)
  n = 1
  ref = As_element
FEATURE [App::DocumentObjectGroupPython] G4_GALLIUM_ARSENIDE  # scripted group (container) (typed FeaturePython)
  Dunit = g/cm3
  Dvalue = 5.31
  Group = -> [Ga_element001,As_element001]
  conduct = 2
  density = 1
  expand = 3
  formula = G4_GALLIUM_ARSENIDE
  name = G4_GALLIUM_ARSENIDE
  specific = 4
FEATURE [App::DocumentObjectGroupPython] H_element041  label="H_element : 0.081"  # scripted group (container) (typed FeaturePython)
  n = 0.08118
FEATURE [App::DocumentObjectGroupPython] C_element048  label="C_element : 0.416"  # scripted group (container) (typed FeaturePython)
  n = 0.41606
FEATURE [App::DocumentObjectGroupPython] N_element018  label="N_element : 0.111"  # scripted group (container) (typed FeaturePython)
  n = 0.11124
FEATURE [App::DocumentObjectGroupPython] O_element042  label="O_element : 0.381"  # scripted group (container) (typed FeaturePython)
  n = 0.38064
FEATURE [App::DocumentObjectGroupPython] S_element013  label="S_element : 0.011"  # scripted group (container) (typed FeaturePython)
  n = 0.01088
FEATURE [App::DocumentObjectGroupPython] G4_GEL_PHOTO_EMULSION  # scripted group (container) (typed FeaturePython)
  Dunit = g/cm3
  Dvalue = 1.2914
  Group = -> [H_element041,C_element048,N_element018,O_element042,S_element013]
  conduct = 2
  density = 1
  expand = 3
  formula = G4_GEL_PHOTO_EMULSION
  name = G4_GEL_PHOTO_EMULSION
  specific = 4
FEATURE [App::DocumentObjectGroupPython] B_element004  label="B_element : 0.040"  # scripted group (container) (typed FeaturePython)
  n = 0.0400639
FEATURE [App::DocumentObjectGroupPython] O_element043  label="O_element : 0.540"  # scripted group (container) (typed FeaturePython)
  n = 0.539561
FEATURE [App::DocumentObjectGroupPython] Na_element008  label="Na_element : 0.028"  # scripted group (container) (typed FeaturePython)
  n = 0.0281909
FEATURE [App::DocumentObjectGroupPython] Al_element003  label="Al_element : 0.012"  # scripted group (container) (typed FeaturePython)
  n = 0.011644
FEATURE [App::DocumentObjectGroupPython] Si_element003  label="Si_element : 0.377"  # scripted group (container) (typed FeaturePython)
  n = 0.377219
FEATURE [App::DocumentObjectGroupPython] K_element004  label="K_element : 0.014"  # scripted group (container) (typed FeaturePython)
  n = 0.00332099
FEATURE [App::DocumentObjectGroupPython] G4_Pyrex_Glass  # scripted group (container) (typed FeaturePython)
  Dunit = g/cm3
  Dvalue = 2.23
  Group = -> [B_element004,O_element043,Na_element008,Al_element003,Si_element003,K_element004]
  conduct = 2
  density = 1
  expand = 3
  formula = G4_Pyrex_Glass
  name = G4_Pyrex_Glass
  specific = 4
FEATURE [App::DocumentObjectGroupPython] O_element044  label="O_element : 0.156"  # scripted group (container) (typed FeaturePython)
  n = 0.156453
FEATURE [App::DocumentObjectGroupPython] Si_element004  label="Si_element : 0.081"  # scripted group (container) (typed FeaturePython)
  n = 0.080866
FEATURE [App::DocumentObjectGroupPython] Ti_element001  label="Ti_element : 0.008"  # scripted group (container) (typed FeaturePython)
  n = 0.008092
FEATURE [App::DocumentObjectGroupPython] As_element002  label="As_element : 0.003"  # scripted group (container) (typed FeaturePython)
  n = 0.002651
FEATURE [App::DocumentObjectGroupPython] Pb_element001  label="Pb_element : 0.752"  # scripted group (container) (typed FeaturePython)
  n = 0.751938
FEATURE [App::DocumentObjectGroupPython] G4_GLASS_LEAD  # scripted group (container) (typed FeaturePython)
  Dunit = g/cm3
  Dvalue = 6.22
  Group = -> [O_element044,Si_element004,Ti_element001,As_element002,Pb_element001]
  conduct = 2
  density = 1
  expand = 3
  formula = G4_GLASS_LEAD
  name = G4_GLASS_LEAD
  specific = 4
FEATURE [App::DocumentObjectGroupPython] O_element045  label="O_element : 0.460"  # scripted group (container) (typed FeaturePython)
  n = 0.4598
FEATURE [App::DocumentObjectGroupPython] Na_element009  label="Na_element : 0.096"  # scripted group (container) (typed FeaturePython)
  n = 0.0964411
FEATURE [App::DocumentObjectGroupPython] Si_element005  label="Si_element : 0.378"  # scripted group (container) (typed FeaturePython)
  n = 0.336553
FEATURE [App::DocumentObjectGroupPython] Ca_element011  label="Ca_element : 0.107"  # scripted group (container) (typed FeaturePython)
  n = 0.107205
FEATURE [App::DocumentObjectGroupPython] G4_GLASS_PLATE  # scripted group (container) (typed FeaturePython)
  Dunit = g/cm3
  Dvalue = 2.4
  Group = -> [O_element045,Na_element009,Si_element005,Ca_element011]
  conduct = 2
  density = 1
  expand = 3
  formula = G4_GLASS_PLATE
  name = G4_GLASS_PLATE
  specific = 4
FEATURE [App::DocumentObjectGroupPython] C_element049  label="C_element : 026"  # scripted group (container) (typed FeaturePython)
  n = 5
  ref = C_element
FEATURE [App::DocumentObjectGroupPython] H_element042  label="H_element : 021"  # scripted group (container) (typed FeaturePython)
  n = 10
  ref = H_element
FEATURE [App::DocumentObjectGroupPython] N_element019  label="N_element : 2"  # scripted group (container) (typed FeaturePython)
  n = 2
  ref = N_element
FEATURE [App::DocumentObjectGroupPython] O_element046  label="O_element : 022"  # scripted group (container) (typed FeaturePython)
  n = 3
  ref = O_element
FEATURE [App::DocumentObjectGroupPython] G4_GLUTAMINE  # scripted group (container) (typed FeaturePython)
  Dunit = g/cm3
  Dvalue = 1.46
  Group = -> [C_element049,H_element042,N_element019,O_element046]
  conduct = 2
  density = 1
  expand = 3
  formula = G4_GLUTAMINE
  name = G4_GLUTAMINE
  specific = 4
FEATURE [App::DocumentObjectGroupPython] C_element050  label="C_element : 027"  # scripted group (container) (typed FeaturePython)
  n = 3
  ref = C_element
FEATURE [App::DocumentObjectGroupPython] H_element043  label="H_element : 022"  # scripted group (container) (typed FeaturePython)
  n = 8
  ref = H_element
FEATURE [App::DocumentObjectGroupPython] O_element047  label="O_element : 023"  # scripted group (container) (typed FeaturePython)
  n = 3
  ref = O_element
FEATURE [App::DocumentObjectGroupPython] G4_GLYCEROL  # scripted group (container) (typed FeaturePython)
  Dunit = g/cm3
  Dvalue = 1.2613
  Group = -> [C_element050,H_element043,O_element047]
  conduct = 2
  density = 1
  expand = 3
  formula = G4_GLYCEROL
  name = G4_GLYCEROL
  specific = 4
FEATURE [App::DocumentObjectGroupPython] C_element051  label="C_element : 028"  # scripted group (container) (typed FeaturePython)
  n = 5
  ref = C_element
FEATURE [App::DocumentObjectGroupPython] H_element044  label="H_element : 023"  # scripted group (container) (typed FeaturePython)
  n = 5
  ref = H_element
FEATURE [App::DocumentObjectGroupPython] N_element020  label="N_element : 009"  # scripted group (container) (typed FeaturePython)
  n = 5
  ref = N_element
FEATURE [App::DocumentObjectGroupPython] O_element048  label="O_element : 024"  # scripted group (container) (typed FeaturePython)
  n = 1
  ref = O_element
FEATURE [App::DocumentObjectGroupPython] G4_GUANINE  # scripted group (container) (typed FeaturePython)
  Dunit = g/cm3
  Dvalue = 2.2
  Group = -> [C_element051,H_element044,N_element020,O_element048]
  conduct = 2
  density = 1
  expand = 3
  formula = G4_GUANINE
  name = G4_GUANINE
  specific = 4
FEATURE [App::DocumentObjectGroupPython] Ca_element012  label="Ca_element : 006"  # scripted group (container) (typed FeaturePython)
  n = 1
  ref = Ca_element
FEATURE [App::DocumentObjectGroupPython] S_element014  label="S_element : 005"  # scripted group (container) (typed FeaturePython)
  n = 1
  ref = S_element
FEATURE [App::DocumentObjectGroupPython] O_element049  label="O_element : 6"  # scripted group (container) (typed FeaturePython)
  n = 6
  ref = O_element
FEATURE [App::DocumentObjectGroupPython] H_element045  label="H_element : 024"  # scripted group (container) (typed FeaturePython)
  n = 4
  ref = H_element
FEATURE [App::DocumentObjectGroupPython] G4_GYPSUM  # scripted group (container) (typed FeaturePython)
  Dunit = g/cm3
  Dvalue = 2.32
  Group = -> [Ca_element012,S_element014,O_element049,H_element045]
  conduct = 2
  density = 1
  expand = 3
  formula = G4_GYPSUM
  name = G4_GYPSUM
  specific = 4
FEATURE [App::DocumentObjectGroupPython] C_element052  label="C_element : 7"  # scripted group (container) (typed FeaturePython)
  n = 7
  ref = C_element
FEATURE [App::DocumentObjectGroupPython] H_element046  label="H_element : 16"  # scripted group (container) (typed FeaturePython)
  n = 16
  ref = H_element
FEATURE [App::DocumentObjectGroupPython] G4_N_HEPTANE  label="G4_N-HEPTANE"  # scripted group (container) (typed FeaturePython)
  Dunit = g/cm3
  Dvalue = 0.68376
  Group = -> [C_element052,H_element046]
  conduct = 2
  density = 1
  expand = 3
  formula = G4_N-HEPTANE
  name = G4_N-HEPTANE
  specific = 4
FEATURE [App::DocumentObjectGroupPython] C_element053  label="C_element : 029"  # scripted group (container) (typed FeaturePython)
  n = 6
  ref = C_element
FEATURE [App::DocumentObjectGroupPython] H_element047  label="H_element : 14"  # scripted group (container) (typed FeaturePython)
  n = 14
  ref = H_element
FEATURE [App::DocumentObjectGroupPython] G4_N_HEXANE  label="G4_N-HEXANE"  # scripted group (container) (typed FeaturePython)
  Dunit = g/cm3
  Dvalue = 0.6603
  Group = -> [C_element053,H_element047]
  conduct = 2
  density = 1
  expand = 3
  formula = G4_N-HEXANE
  name = G4_N-HEXANE
  specific = 4
FEATURE [App::DocumentObjectGroupPython] C_element054  label="C_element : 22"  # scripted group (container) (typed FeaturePython)
  n = 22
  ref = C_element
FEATURE [App::DocumentObjectGroupPython] H_element048  label="H_element : 025"  # scripted group (container) (typed FeaturePython)
  n = 10
  ref = H_element
FEATURE [App::DocumentObjectGroupPython] N_element021  label="N_element : 010"  # scripted group (container) (typed FeaturePython)
  n = 2
  ref = N_element
FEATURE [App::DocumentObjectGroupPython] O_element050  label="O_element : 025"  # scripted group (container) (typed FeaturePython)
  n = 5
  ref = O_element
FEATURE [App::DocumentObjectGroupPython] G4_KAPTON  # scripted group (container) (typed FeaturePython)
  Dunit = g/cm3
  Dvalue = 1.42
  Group = -> [C_element054,H_element048,N_element021,O_element050]
  conduct = 2
  density = 1
  expand = 3
  formula = G4_KAPTON
  name = G4_KAPTON
  specific = 4
FEATURE [App::DocumentObjectGroupPython] La_element001  label="La_element : 1"  # scripted group (container) (typed FeaturePython)
  n = 1
  ref = La_element
FEATURE [App::DocumentObjectGroupPython] Br_element003  label="Br_element : 002"  # scripted group (container) (typed FeaturePython)
  n = 1
  ref = Br_element
FEATURE [App::DocumentObjectGroupPython] O_element051  label="O_element : 026"  # scripted group (container) (typed FeaturePython)
  n = 1
  ref = O_element
FEATURE [App::DocumentObjectGroupPython] G4_LANTHANUM_OXYBROMIDE  # scripted group (container) (typed FeaturePython)
  Dunit = g/cm3
  Dvalue = 6.28
  Group = -> [La_element001,Br_element003,O_element051]
  conduct = 2
  density = 1
  expand = 3
  formula = G4_LANTHANUM_OXYBROMIDE
  name = G4_LANTHANUM_OXYBROMIDE
  specific = 4
FEATURE [App::DocumentObjectGroupPython] La_element002  label="La_element : 2"  # scripted group (container) (typed FeaturePython)
  n = 2
  ref = La_element
FEATURE [App::DocumentObjectGroupPython] O_element052  label="O_element : 027"  # scripted group (container) (typed FeaturePython)
  n = 2
  ref = O_element
FEATURE [App::DocumentObjectGroupPython] S_element015  label="S_element : 006"  # scripted group (container) (typed FeaturePython)
  n = 1
  ref = S_element
FEATURE [App::DocumentObjectGroupPython] G4_LANTHANUM_OXYSULFIDE  # scripted group (container) (typed FeaturePython)
  Dunit = g/cm3
  Dvalue = 5.86
  Group = -> [La_element002,O_element052,S_element015]
  conduct = 2
  density = 1
  expand = 3
  formula = G4_LANTHANUM_OXYSULFIDE
  name = G4_LANTHANUM_OXYSULFIDE
  specific = 4
FEATURE [App::DocumentObjectGroupPython] O_element053  label="O_element : 0.072"  # scripted group (container) (typed FeaturePython)
  n = 0.071682
FEATURE [App::DocumentObjectGroupPython] Pb_element002  label="Pb_element : 0.928"  # scripted group (container) (typed FeaturePython)
  n = 0.928318
FEATURE [App::DocumentObjectGroupPython] G4_LEAD_OXIDE  # scripted group (container) (typed FeaturePython)
  Dunit = g/cm3
  Dvalue = 9.53
  Group = -> [O_element053,Pb_element002]
  conduct = 2
  density = 1
  expand = 3
  formula = G4_LEAD_OXIDE
  name = G4_LEAD_OXIDE
  specific = 4
FEATURE [App::DocumentObjectGroupPython] Li_element001  label="Li_element : 1"  # scripted group (container) (typed FeaturePython)
  n = 1
  ref = Li_element
FEATURE [App::DocumentObjectGroupPython] N_element022  label="N_element : 011"  # scripted group (container) (typed FeaturePython)
  n = 1
  ref = N_element
FEATURE [App::DocumentObjectGroupPython] H_element049  label="H_element : 026"  # scripted group (container) (typed FeaturePython)
  n = 2
  ref = H_element
FEATURE [App::DocumentObjectGroupPython] G4_LITHIUM_AMIDE  # scripted group (container) (typed FeaturePython)
  Dunit = g/cm3
  Dvalue = 1.178
  Group = -> [Li_element001,N_element022,H_element049]
  conduct = 2
  density = 1
  expand = 3
  formula = G4_LITHIUM_AMIDE
  name = G4_LITHIUM_AMIDE
  specific = 4
FEATURE [App::DocumentObjectGroupPython] Li_element002  label="Li_element : 2"  # scripted group (container) (typed FeaturePython)
  n = 2
  ref = Li_element
FEATURE [App::DocumentObjectGroupPython] C_element055  label="C_element : 030"  # scripted group (container) (typed FeaturePython)
  n = 1
  ref = C_element
FEATURE [App::DocumentObjectGroupPython] O_element054  label="O_element : 028"  # scripted group (container) (typed FeaturePython)
  n = 3
  ref = O_element
FEATURE [App::DocumentObjectGroupPython] G4_LITHIUM_CARBONATE  # scripted group (container) (typed FeaturePython)
  Dunit = g/cm3
  Dvalue = 2.11
  Group = -> [Li_element002,C_element055,O_element054]
  conduct = 2
  density = 1
  expand = 3
  formula = G4_LITHIUM_CARBONATE
  name = G4_LITHIUM_CARBONATE
  specific = 4
FEATURE [App::DocumentObjectGroupPython] Li_element003  label="Li_element : 003"  # scripted group (container) (typed FeaturePython)
  n = 1
  ref = Li_element
FEATURE [App::DocumentObjectGroupPython] F_element012  label="F_element : 004"  # scripted group (container) (typed FeaturePython)
  n = 1
  ref = F_element
FEATURE [App::DocumentObjectGroupPython] G4_LITHIUM_FLUORIDE  # scripted group (container) (typed FeaturePython)
  Dunit = g/cm3
  Dvalue = 2.635
  Group = -> [Li_element003,F_element012]
  conduct = 2
  density = 1
  expand = 3
  formula = G4_LITHIUM_FLUORIDE
  name = G4_LITHIUM_FLUORIDE
  specific = 4
FEATURE [App::DocumentObjectGroupPython] Li_element004  label="Li_element : 004"  # scripted group (container) (typed FeaturePython)
  n = 1
  ref = Li_element
FEATURE [App::DocumentObjectGroupPython] H_element050  label="H_element : 027"  # scripted group (container) (typed FeaturePython)
  n = 1
  ref = H_element
FEATURE [App::DocumentObjectGroupPython] G4_LITHIUM_HYDRIDE  # scripted group (container) (typed FeaturePython)
  Dunit = g/cm3
  Dvalue = 0.82
  Group = -> [Li_element004,H_element050]
  conduct = 2
  density = 1
  expand = 3
  formula = G4_LITHIUM_HYDRIDE
  name = G4_LITHIUM_HYDRIDE
  specific = 4
FEATURE [App::DocumentObjectGroupPython] Li_element005  label="Li_element : 005"  # scripted group (container) (typed FeaturePython)
  n = 1
  ref = Li_element
FEATURE [App::DocumentObjectGroupPython] I_element003  label="I_element : 002"  # scripted group (container) (typed FeaturePython)
  n = 1
  ref = I_element
FEATURE [App::DocumentObjectGroupPython] G4_LITHIUM_IODIDE  # scripted group (container) (typed FeaturePython)
  Dunit = g/cm3
  Dvalue = 3.494
  Group = -> [Li_element005,I_element003]
  conduct = 2
  density = 1
  expand = 3
  formula = G4_LITHIUM_IODIDE
  name = G4_LITHIUM_IODIDE
  specific = 4
FEATURE [App::DocumentObjectGroupPython] Li_element006  label="Li_element : 006"  # scripted group (container) (typed FeaturePython)
  n = 2
  ref = Li_element
FEATURE [App::DocumentObjectGroupPython] O_element055  label="O_element : 029"  # scripted group (container) (typed FeaturePython)
  n = 1
  ref = O_element
FEATURE [App::DocumentObjectGroupPython] G4_LITHIUM_OXIDE  # scripted group (container) (typed FeaturePython)
  Dunit = g/cm3
  Dvalue = 2.013
  Group = -> [Li_element006,O_element055]
  conduct = 2
  density = 1
  expand = 3
  formula = G4_LITHIUM_OXIDE
  name = G4_LITHIUM_OXIDE
  specific = 4
FEATURE [App::DocumentObjectGroupPython] Li_element007  label="Li_element : 007"  # scripted group (container) (typed FeaturePython)
  n = 2
  ref = Li_element
FEATURE [App::DocumentObjectGroupPython] B_element005  label="B_element : 005"  # scripted group (container) (typed FeaturePython)
  n = 4
  ref = B_element
FEATURE [App::DocumentObjectGroupPython] O_element056  label="O_element : 7"  # scripted group (container) (typed FeaturePython)
  n = 7
  ref = O_element
FEATURE [App::DocumentObjectGroupPython] G4_LITHIUM_TETRABORATE  # scripted group (container) (typed FeaturePython)
  Dunit = g/cm3
  Dvalue = 2.44
  Group = -> [Li_element007,B_element005,O_element056]
  conduct = 2
  density = 1
  expand = 3
  formula = G4_LITHIUM_TETRABORATE
  name = G4_LITHIUM_TETRABORATE
  specific = 4
FEATURE [App::DocumentObjectGroupPython] H_element051  label="H_element : 0.105"  # scripted group (container) (typed FeaturePython)
  n = 0.105
FEATURE [App::DocumentObjectGroupPython] C_element056  label="C_element : 0.083"  # scripted group (container) (typed FeaturePython)
  n = 0.083
FEATURE [App::DocumentObjectGroupPython] N_element023  label="N_element : 0.023"  # scripted group (container) (typed FeaturePython)
  n = 0.023
FEATURE [App::DocumentObjectGroupPython] O_element057  label="O_element : 0.779"  # scripted group (container) (typed FeaturePython)
  n = 0.779
FEATURE [App::DocumentObjectGroupPython] Na_element010  label="Na_element : 0.097"  # scripted group (container) (typed FeaturePython)
  n = 0.002
FEATURE [App::DocumentObjectGroupPython] P_element006  label="P_element : 0.105"  # scripted group (container) (typed FeaturePython)
  n = 0.001
FEATURE [App::DocumentObjectGroupPython] S_element016  label="S_element : 0.017"  # scripted group (container) (typed FeaturePython)
  n = 0.002
FEATURE [App::DocumentObjectGroupPython] Cl_element014  label="Cl_element : 0.587"  # scripted group (container) (typed FeaturePython)
  n = 0.003
FEATURE [App::DocumentObjectGroupPython] K_element005  label="K_element : 0.015"  # scripted group (container) (typed FeaturePython)
  n = 0.002
FEATURE [App::DocumentObjectGroupPython] G4_LUNG_ICRP  # scripted group (container) (typed FeaturePython)
  Dunit = g/cm3
  Dvalue = 1.04
  Group = -> [H_element051,C_element056,N_element023,O_element057,Na_element010,P_element006,S_element016,Cl_element014,K_element005]
  conduct = 2
  density = 1
  expand = 3
  formula = G4_LUNG_ICRP
  name = G4_LUNG_ICRP
  specific = 4
FEATURE [App::DocumentObjectGroupPython] H_element052  label="H_element : 0.116"  # scripted group (container) (typed FeaturePython)
  n = 0.114318
FEATURE [App::DocumentObjectGroupPython] C_element057  label="C_element : 0.656"  # scripted group (container) (typed FeaturePython)
  n = 0.655824
FEATURE [App::DocumentObjectGroupPython] O_element058  label="O_element : 0.092"  # scripted group (container) (typed FeaturePython)
  n = 0.0921831
FEATURE [App::DocumentObjectGroupPython] Mg_element004  label="Mg_element : 0.135"  # scripted group (container) (typed FeaturePython)
  n = 0.134792
FEATURE [App::DocumentObjectGroupPython] Ca_element013  label="Ca_element : 0.003"  # scripted group (container) (typed FeaturePython)
  n = 0.002883
FEATURE [App::DocumentObjectGroupPython] G4_M3_WAX  # scripted group (container) (typed FeaturePython)
  Dunit = g/cm3
  Dvalue = 1.05
  Group = -> [H_element052,C_element057,O_element058,Mg_element004,Ca_element013]
  conduct = 2
  density = 1
  expand = 3
  formula = G4_M3_WAX
  name = G4_M3_WAX
  specific = 4
FEATURE [App::DocumentObjectGroupPython] Mg_element005  label="Mg_element : 1"  # scripted group (container) (typed FeaturePython)
  n = 1
  ref = Mg_element
FEATURE [App::DocumentObjectGroupPython] C_element058  label="C_element : 031"  # scripted group (container) (typed FeaturePython)
  n = 1
  ref = C_element
FEATURE [App::DocumentObjectGroupPython] O_element059  label="O_element : 030"  # scripted group (container) (typed FeaturePython)
  n = 3
  ref = O_element
FEATURE [App::DocumentObjectGroupPython] G4_MAGNESIUM_CARBONATE  # scripted group (container) (typed FeaturePython)
  Dunit = g/cm3
  Dvalue = 2.958
  Group = -> [Mg_element005,C_element058,O_element059]
  conduct = 2
  density = 1
  expand = 3
  formula = G4_MAGNESIUM_CARBONATE
  name = G4_MAGNESIUM_CARBONATE
  specific = 4
FEATURE [App::DocumentObjectGroupPython] Mg_element006  label="Mg_element : 002"  # scripted group (container) (typed FeaturePython)
  n = 1
  ref = Mg_element
FEATURE [App::DocumentObjectGroupPython] F_element013  label="F_element : 005"  # scripted group (container) (typed FeaturePython)
  n = 2
  ref = F_element
FEATURE [App::DocumentObjectGroupPython] G4_MAGNESIUM_FLUORIDE  # scripted group (container) (typed FeaturePython)
  Dunit = g/cm3
  Dvalue = 3
  Group = -> [Mg_element006,F_element013]
  conduct = 2
  density = 1
  expand = 3
  formula = G4_MAGNESIUM_FLUORIDE
  name = G4_MAGNESIUM_FLUORIDE
  specific = 4
FEATURE [App::DocumentObjectGroupPython] Mg_element007  label="Mg_element : 003"  # scripted group (container) (typed FeaturePython)
  n = 1
  ref = Mg_element
FEATURE [App::DocumentObjectGroupPython] O_element060  label="O_element : 031"  # scripted group (container) (typed FeaturePython)
  n = 1
  ref = O_element
FEATURE [App::DocumentObjectGroupPython] G4_MAGNESIUM_OXIDE  # scripted group (container) (typed FeaturePython)
  Dunit = g/cm3
  Dvalue = 3.58
  Group = -> [Mg_element007,O_element060]
  conduct = 2
  density = 1
  expand = 3
  formula = G4_MAGNESIUM_OXIDE
  name = G4_MAGNESIUM_OXIDE
  specific = 4
FEATURE [App::DocumentObjectGroupPython] Mg_element008  label="Mg_element : 004"  # scripted group (container) (typed FeaturePython)
  n = 1
  ref = Mg_element
FEATURE [App::DocumentObjectGroupPython] B_element006  label="B_element : 006"  # scripted group (container) (typed FeaturePython)
  n = 4
  ref = B_element
FEATURE [App::DocumentObjectGroupPython] O_element061  label="O_element : 032"  # scripted group (container) (typed FeaturePython)
  n = 7
  ref = O_element
FEATURE [App::DocumentObjectGroupPython] G4_MAGNESIUM_TETRABORATE  # scripted group (container) (typed FeaturePython)
  Dunit = g/cm3
  Dvalue = 2.53
  Group = -> [Mg_element008,B_element006,O_element061]
  conduct = 2
  density = 1
  expand = 3
  formula = G4_MAGNESIUM_TETRABORATE
  name = G4_MAGNESIUM_TETRABORATE
  specific = 4
FEATURE [App::DocumentObjectGroupPython] Hg_element001  label="Hg_element : 1"  # scripted group (container) (typed FeaturePython)
  n = 1
  ref = Hg_element
FEATURE [App::DocumentObjectGroupPython] I_element004  label="I_element : 2"  # scripted group (container) (typed FeaturePython)
  n = 2
  ref = I_element
FEATURE [App::DocumentObjectGroupPython] G4_MERCURIC_IODIDE  # scripted group (container) (typed FeaturePython)
  Dunit = g/cm3
  Dvalue = 6.36
  Group = -> [Hg_element001,I_element004]
  conduct = 2
  density = 1
  expand = 3
  formula = G4_MERCURIC_IODIDE
  name = G4_MERCURIC_IODIDE
  specific = 4
FEATURE [App::DocumentObjectGroupPython] C_element059  label="C_element : 032"  # scripted group (container) (typed FeaturePython)
  n = 1
  ref = C_element
FEATURE [App::DocumentObjectGroupPython] H_element053  label="H_element : 028"  # scripted group (container) (typed FeaturePython)
  n = 4
  ref = H_element
FEATURE [App::DocumentObjectGroupPython] G4_METHANE  # scripted group (container) (typed FeaturePython)
  Dunit = g/cm3
  Dvalue = 0.000667151
  Group = -> [C_element059,H_element053]
  conduct = 2
  density = 1
  expand = 3
  formula = G4_METHANE
  name = G4_METHANE
  specific = 4
FEATURE [App::DocumentObjectGroupPython] C_element060  label="C_element : 033"  # scripted group (container) (typed FeaturePython)
  n = 1
  ref = C_element
FEATURE [App::DocumentObjectGroupPython] H_element054  label="H_element : 029"  # scripted group (container) (typed FeaturePython)
  n = 4
  ref = H_element
FEATURE [App::DocumentObjectGroupPython] O_element062  label="O_element : 033"  # scripted group (container) (typed FeaturePython)
  n = 1
  ref = O_element
FEATURE [App::DocumentObjectGroupPython] G4_METHANOL  # scripted group (container) (typed FeaturePython)
  Dunit = g/cm3
  Dvalue = 0.7914
  Group = -> [C_element060,H_element054,O_element062]
  conduct = 2
  density = 1
  expand = 3
  formula = G4_METHANOL
  name = G4_METHANOL
  specific = 4
FEATURE [App::DocumentObjectGroupPython] H_element055  label="H_element : 0.134"  # scripted group (container) (typed FeaturePython)
  n = 0.13404
FEATURE [App::DocumentObjectGroupPython] C_element061  label="C_element : 0.778"  # scripted group (container) (typed FeaturePython)
  n = 0.77796
FEATURE [App::DocumentObjectGroupPython] O_element063  label="O_element : 0.035"  # scripted group (container) (typed FeaturePython)
  n = 0.03502
FEATURE [App::DocumentObjectGroupPython] Mg_element009  label="Mg_element : 0.039"  # scripted group (container) (typed FeaturePython)
  n = 0.038594
FEATURE [App::DocumentObjectGroupPython] Ti_element002  label="Ti_element : 0.014"  # scripted group (container) (typed FeaturePython)
  n = 0.014386
FEATURE [App::DocumentObjectGroupPython] G4_MIX_D_WAX  # scripted group (container) (typed FeaturePython)
  Dunit = g/cm3
  Dvalue = 0.99
  Group = -> [H_element055,C_element061,O_element063,Mg_element009,Ti_element002]
  conduct = 2
  density = 1
  expand = 3
  formula = G4_MIX_D_WAX
  name = G4_MIX_D_WAX
  specific = 4
FEATURE [App::DocumentObjectGroupPython] H_element056  label="H_element : 0.135"  # scripted group (container) (typed FeaturePython)
  n = 0.081192
FEATURE [App::DocumentObjectGroupPython] C_element062  label="C_element : 0.583"  # scripted group (container) (typed FeaturePython)
  n = 0.583442
FEATURE [App::DocumentObjectGroupPython] N_element024  label="N_element : 0.018"  # scripted group (container) (typed FeaturePython)
  n = 0.017798
FEATURE [App::DocumentObjectGroupPython] O_element064  label="O_element : 0.186"  # scripted group (container) (typed FeaturePython)
  n = 0.186381
FEATURE [App::DocumentObjectGroupPython] Mg_element010  label="Mg_element : 0.130"  # scripted group (container) (typed FeaturePython)
  n = 0.130287
FEATURE [App::DocumentObjectGroupPython] Cl_element015  label="Cl_element : 0.588"  # scripted group (container) (typed FeaturePython)
  n = 0.0009
FEATURE [App::DocumentObjectGroupPython] G4_MS20_TISSUE  # scripted group (container) (typed FeaturePython)
  Dunit = g/cm3
  Dvalue = 1
  Group = -> [H_element056,C_element062,N_element024,O_element064,Mg_element010,Cl_element015]
  conduct = 2
  density = 1
  expand = 3
  formula = G4_MS20_TISSUE
  name = G4_MS20_TISSUE
  specific = 4
FEATURE [App::DocumentObjectGroupPython] H_element057  label="H_element : 0.136"  # scripted group (container) (typed FeaturePython)
  n = 0.102
FEATURE [App::DocumentObjectGroupPython] C_element063  label="C_element : 0.143"  # scripted group (container) (typed FeaturePython)
  n = 0.143
FEATURE [App::DocumentObjectGroupPython] N_element025  label="N_element : 0.034"  # scripted group (container) (typed FeaturePython)
  n = 0.034
FEATURE [App::DocumentObjectGroupPython] O_element065  label="O_element : 0.710"  # scripted group (container) (typed FeaturePython)
  n = 0.71
FEATURE [App::DocumentObjectGroupPython] Na_element011  label="Na_element : 0.098"  # scripted group (container) (typed FeaturePython)
  n = 0.001
FEATURE [App::DocumentObjectGroupPython] P_element007  label="P_element : 0.002"  # scripted group (container) (typed FeaturePython)
  n = 0.002
FEATURE [App::DocumentObjectGroupPython] S_element017  label="S_element : 0.018"  # scripted group (container) (typed FeaturePython)
  n = 0.003
FEATURE [App::DocumentObjectGroupPython] Cl_element016  label="Cl_element : 0.589"  # scripted group (container) (typed FeaturePython)
  n = 0.001
FEATURE [App::DocumentObjectGroupPython] K_element006  label="K_element : 0.004"  # scripted group (container) (typed FeaturePython)
  n = 0.004
FEATURE [App::DocumentObjectGroupPython] G4_MUSCLE_SKELETAL_ICRP  # scripted group (container) (typed FeaturePython)
  Dunit = g/cm3
  Dvalue = 1.05
  Group = -> [H_element057,C_element063,N_element025,O_element065,Na_element011,P_element007,S_element017,Cl_element016,K_element006]
  conduct = 2
  density = 1
  expand = 3
  formula = G4_MUSCLE_SKELETAL_ICRP
  name = G4_MUSCLE_SKELETAL_ICRP
  specific = 4
FEATURE [App::DocumentObjectGroupPython] H_element058  label="H_element : 0.137"  # scripted group (container) (typed FeaturePython)
  n = 0.102102
FEATURE [App::DocumentObjectGroupPython] C_element064  label="C_element : 0.123"  # scripted group (container) (typed FeaturePython)
  n = 0.123123
FEATURE [App::DocumentObjectGroupPython] N_element026  label="N_element : 0.756"  # scripted group (container) (typed FeaturePython)
  n = 0.035035
FEATURE [App::DocumentObjectGroupPython] O_element066  label="O_element : 0.730"  # scripted group (container) (typed FeaturePython)
  n = 0.72973
FEATURE [App::DocumentObjectGroupPython] Na_element012  label="Na_element : 0.099"  # scripted group (container) (typed FeaturePython)
  n = 0.001001
FEATURE [App::DocumentObjectGroupPython] P_element008  label="P_element : 0.106"  # scripted group (container) (typed FeaturePython)
  n = 0.002002
FEATURE [App::DocumentObjectGroupPython] S_element018  label="S_element : 0.019"  # scripted group (container) (typed FeaturePython)
  n = 0.004004
FEATURE [App::DocumentObjectGroupPython] K_element007  label="K_element : 0.016"  # scripted group (container) (typed FeaturePython)
  n = 0.003003
FEATURE [App::DocumentObjectGroupPython] G4_MUSCLE_STRIATED_ICRU  # scripted group (container) (typed FeaturePython)
  Dunit = g/cm3
  Dvalue = 1.04
  Group = -> [H_element058,C_element064,N_element026,O_element066,Na_element012,P_element008,S_element018,K_element007]
  conduct = 2
  density = 1
  expand = 3
  formula = G4_MUSCLE_STRIATED_ICRU
  name = G4_MUSCLE_STRIATED_ICRU
  specific = 4
FEATURE [App::DocumentObjectGroupPython] H_element059  label="H_element : 0.098"  # scripted group (container) (typed FeaturePython)
  n = 0.0982341
FEATURE [App::DocumentObjectGroupPython] C_element065  label="C_element : 0.156"  # scripted group (container) (typed FeaturePython)
  n = 0.156214
FEATURE [App::DocumentObjectGroupPython] N_element027  label="N_element : 0.757"  # scripted group (container) (typed FeaturePython)
  n = 0.035451
FEATURE [App::DocumentObjectGroupPython] O_element067  label="O_element : 0.880"  # scripted group (container) (typed FeaturePython)
  n = 0.710101
FEATURE [App::DocumentObjectGroupPython] G4_MUSCLE_WITH_SUCROSE  # scripted group (container) (typed FeaturePython)
  Dunit = g/cm3
  Dvalue = 1.11
  Group = -> [H_element059,C_element065,N_element027,O_element067]
  conduct = 2
  density = 1
  expand = 3
  formula = G4_MUSCLE_WITH_SUCROSE
  name = G4_MUSCLE_WITH_SUCROSE
  specific = 4
FEATURE [App::DocumentObjectGroupPython] H_element060  label="H_element : 0.138"  # scripted group (container) (typed FeaturePython)
  n = 0.101969
FEATURE [App::DocumentObjectGroupPython] C_element066  label="C_element : 0.120"  # scripted group (container) (typed FeaturePython)
  n = 0.120058
FEATURE [App::DocumentObjectGroupPython] N_element028  label="N_element : 0.758"  # scripted group (container) (typed FeaturePython)
  n = 0.035451
FEATURE [App::DocumentObjectGroupPython] O_element068  label="O_element : 0.743"  # scripted group (container) (typed FeaturePython)
  n = 0.742522
FEATURE [App::DocumentObjectGroupPython] G4_MUSCLE_WITHOUT_SUCROSE  # scripted group (container) (typed FeaturePython)
  Dunit = g/cm3
  Dvalue = 1.07
  Group = -> [H_element060,C_element066,N_element028,O_element068]
  conduct = 2
  density = 1
  expand = 3
  formula = G4_MUSCLE_WITHOUT_SUCROSE
  name = G4_MUSCLE_WITHOUT_SUCROSE
  specific = 4
FEATURE [App::DocumentObjectGroupPython] C_element067  label="C_element : 10"  # scripted group (container) (typed FeaturePython)
  n = 10
  ref = C_element
FEATURE [App::DocumentObjectGroupPython] H_element061  label="H_element : 030"  # scripted group (container) (typed FeaturePython)
  n = 8
  ref = H_element
FEATURE [App::DocumentObjectGroupPython] G4_NAPHTHALENE  # scripted group (container) (typed FeaturePython)
  Dunit = g/cm3
  Dvalue = 1.145
  Group = -> [C_element067,H_element061]
  conduct = 2
  density = 1
  expand = 3
  formula = G4_NAPHTHALENE
  name = G4_NAPHTHALENE
  specific = 4
FEATURE [App::DocumentObjectGroupPython] C_element068  label="C_element : 034"  # scripted group (container) (typed FeaturePython)
  n = 6
  ref = C_element
FEATURE [App::DocumentObjectGroupPython] H_element062  label="H_element : 031"  # scripted group (container) (typed FeaturePython)
  n = 5
  ref = H_element
FEATURE [App::DocumentObjectGroupPython] N_element029  label="N_element : 012"  # scripted group (container) (typed FeaturePython)
  n = 1
  ref = N_element
FEATURE [App::DocumentObjectGroupPython] O_element069  label="O_element : 034"  # scripted group (container) (typed FeaturePython)
  n = 2
  ref = O_element
FEATURE [App::DocumentObjectGroupPython] G4_NITROBENZENE  # scripted group (container) (typed FeaturePython)
  Dunit = g/cm3
  Dvalue = 1.19867
  Group = -> [C_element068,H_element062,N_element029,O_element069]
  conduct = 2
  density = 1
  expand = 3
  formula = G4_NITROBENZENE
  name = G4_NITROBENZENE
  specific = 4
FEATURE [App::DocumentObjectGroupPython] N_element030  label="N_element : 013"  # scripted group (container) (typed FeaturePython)
  n = 2
  ref = N_element
FEATURE [App::DocumentObjectGroupPython] O_element070  label="O_element : 035"  # scripted group (container) (typed FeaturePython)
  n = 1
  ref = O_element
FEATURE [App::DocumentObjectGroupPython] G4_NITROUS_OXIDE  # scripted group (container) (typed FeaturePython)
  Dunit = g/cm3
  Dvalue = 0.00183094
  Group = -> [N_element030,O_element070]
  conduct = 2
  density = 1
  expand = 3
  formula = G4_NITROUS_OXIDE
  name = G4_NITROUS_OXIDE
  specific = 4
FEATURE [App::DocumentObjectGroupPython] H_element063  label="H_element : 0.104"  # scripted group (container) (typed FeaturePython)
  n = 0.103509
FEATURE [App::DocumentObjectGroupPython] C_element069  label="C_element : 0.648"  # scripted group (container) (typed FeaturePython)
  n = 0.648416
FEATURE [App::DocumentObjectGroupPython] N_element031  label="N_element : 0.100"  # scripted group (container) (typed FeaturePython)
  n = 0.0995361
FEATURE [App::DocumentObjectGroupPython] O_element071  label="O_element : 0.149"  # scripted group (container) (typed FeaturePython)
  n = 0.148539
FEATURE [App::DocumentObjectGroupPython] G4_NYLON_8062  label="G4_NYLON-8062"  # scripted group (container) (typed FeaturePython)
  Dunit = g/cm3
  Dvalue = 1.08
  Group = -> [H_element063,C_element069,N_element031,O_element071]
  conduct = 2
  density = 1
  expand = 3
  formula = G4_NYLON-8062
  name = G4_NYLON-8062
  specific = 4
FEATURE [App::DocumentObjectGroupPython] C_element070  label="C_element : 035"  # scripted group (container) (typed FeaturePython)
  n = 6
  ref = C_element
FEATURE [App::DocumentObjectGroupPython] H_element064  label="H_element : 11"  # scripted group (container) (typed FeaturePython)
  n = 11
  ref = H_element
FEATURE [App::DocumentObjectGroupPython] N_element032  label="N_element : 014"  # scripted group (container) (typed FeaturePython)
  n = 1
  ref = N_element
FEATURE [App::DocumentObjectGroupPython] O_element072  label="O_element : 036"  # scripted group (container) (typed FeaturePython)
  n = 1
  ref = O_element
FEATURE [App::DocumentObjectGroupPython] G4_NYLON_6_6  label="G4_NYLON-6-6"  # scripted group (container) (typed FeaturePython)
  Dunit = g/cm3
  Dvalue = 1.14
  Group = -> [C_element070,H_element064,N_element032,O_element072]
  conduct = 2
  density = 1
  expand = 3
  formula = G4_NYLON-6-6
  name = G4_NYLON-6-6
  specific = 4
FEATURE [App::DocumentObjectGroupPython] H_element065  label="H_element : 0.139"  # scripted group (container) (typed FeaturePython)
  n = 0.107062
FEATURE [App::DocumentObjectGroupPython] C_element071  label="C_element : 0.680"  # scripted group (container) (typed FeaturePython)
  n = 0.680449
FEATURE [App::DocumentObjectGroupPython] N_element033  label="N_element : 0.099"  # scripted group (container) (typed FeaturePython)
  n = 0.099189
FEATURE [App::DocumentObjectGroupPython] O_element073  label="O_element : 0.113"  # scripted group (container) (typed FeaturePython)
  n = 0.1133
FEATURE [App::DocumentObjectGroupPython] G4_NYLON_6_10  label="G4_NYLON-6-10"  # scripted group (container) (typed FeaturePython)
  Dunit = g/cm3
  Dvalue = 1.14
  Group = -> [H_element065,C_element071,N_element033,O_element073]
  conduct = 2
  density = 1
  expand = 3
  formula = G4_NYLON-6-10
  name = G4_NYLON-6-10
  specific = 4
FEATURE [App::DocumentObjectGroupPython] H_element066  label="H_element : 0.140"  # scripted group (container) (typed FeaturePython)
  n = 0.115476
FEATURE [App::DocumentObjectGroupPython] C_element072  label="C_element : 0.721"  # scripted group (container) (typed FeaturePython)
  n = 0.720818
FEATURE [App::DocumentObjectGroupPython] N_element034  label="N_element : 0.076"  # scripted group (container) (typed FeaturePython)
  n = 0.0764169
FEATURE [App::DocumentObjectGroupPython] O_element074  label="O_element : 0.087"  # scripted group (container) (typed FeaturePython)
  n = 0.0872889
FEATURE [App::DocumentObjectGroupPython] G4_NYLON_11_RILSAN  label="G4_NYLON-11_RILSAN"  # scripted group (container) (typed FeaturePython)
  Dunit = g/cm3
  Dvalue = 1.425
  Group = -> [H_element066,C_element072,N_element034,O_element074]
  conduct = 2
  density = 1
  expand = 3
  formula = G4_NYLON-11_RILSAN
  name = G4_NYLON-11_RILSAN
  specific = 4
FEATURE [App::DocumentObjectGroupPython] C_element073  label="C_element : 8"  # scripted group (container) (typed FeaturePython)
  n = 8
  ref = C_element
FEATURE [App::DocumentObjectGroupPython] H_element067  label="H_element : 18"  # scripted group (container) (typed FeaturePython)
  n = 18
  ref = H_element
FEATURE [App::DocumentObjectGroupPython] G4_OCTANE  # scripted group (container) (typed FeaturePython)
  Dunit = g/cm3
  Dvalue = 0.7026
  Group = -> [C_element073,H_element067]
  conduct = 2
  density = 1
  expand = 3
  formula = G4_OCTANE
  name = G4_OCTANE
  specific = 4
FEATURE [App::DocumentObjectGroupPython] C_element074  label="C_element : 25"  # scripted group (container) (typed FeaturePython)
  n = 25
  ref = C_element
FEATURE [App::DocumentObjectGroupPython] H_element068  label="H_element : 52"  # scripted group (container) (typed FeaturePython)
  n = 52
  ref = H_element
FEATURE [App::DocumentObjectGroupPython] G4_PARAFFIN  # scripted group (container) (typed FeaturePython)
  Dunit = g/cm3
  Dvalue = 0.93
  Group = -> [C_element074,H_element068]
  conduct = 2
  density = 1
  expand = 3
  formula = G4_PARAFFIN
  name = G4_PARAFFIN
  specific = 4
FEATURE [App::DocumentObjectGroupPython] C_element075  label="C_element : 036"  # scripted group (container) (typed FeaturePython)
  n = 5
  ref = C_element
FEATURE [App::DocumentObjectGroupPython] H_element069  label="H_element : 032"  # scripted group (container) (typed FeaturePython)
  n = 12
  ref = H_element
FEATURE [App::DocumentObjectGroupPython] G4_N_PENTANE  label="G4_N-PENTANE"  # scripted group (container) (typed FeaturePython)
  Dunit = g/cm3
  Dvalue = 0.6262
  Group = -> [C_element075,H_element069]
  conduct = 2
  density = 1
  expand = 3
  formula = G4_N-PENTANE
  name = G4_N-PENTANE
  specific = 4
FEATURE [App::DocumentObjectGroupPython] H_element070  label="H_element : 0.014"  # scripted group (container) (typed FeaturePython)
  n = 0.0141
FEATURE [App::DocumentObjectGroupPython] C_element076  label="C_element : 0.072"  # scripted group (container) (typed FeaturePython)
  n = 0.072261
FEATURE [App::DocumentObjectGroupPython] N_element035  label="N_element : 0.019"  # scripted group (container) (typed FeaturePython)
  n = 0.01932
FEATURE [App::DocumentObjectGroupPython] O_element075  label="O_element : 0.066"  # scripted group (container) (typed FeaturePython)
  n = 0.066101
FEATURE [App::DocumentObjectGroupPython] S_element019  label="S_element : 0.020"  # scripted group (container) (typed FeaturePython)
  n = 0.00189
FEATURE [App::DocumentObjectGroupPython] Br_element004  label="Br_element : 0.349"  # scripted group (container) (typed FeaturePython)
  n = 0.349103
FEATURE [App::DocumentObjectGroupPython] Ag_element001  label="Ag_element : 0.474"  # scripted group (container) (typed FeaturePython)
  n = 0.474105
FEATURE [App::DocumentObjectGroupPython] I_element005  label="I_element : 0.003"  # scripted group (container) (typed FeaturePython)
  n = 0.00312
FEATURE [App::DocumentObjectGroupPython] G4_PHOTO_EMULSION  # scripted group (container) (typed FeaturePython)
  Dunit = g/cm3
  Dvalue = 3.815
  Group = -> [H_element070,C_element076,N_element035,O_element075,S_element019,Br_element004,Ag_element001,I_element005]
  conduct = 2
  density = 1
  expand = 3
  formula = G4_PHOTO_EMULSION
  name = G4_PHOTO_EMULSION
  specific = 4
FEATURE [App::DocumentObjectGroupPython] C_element077  label="C_element : 9"  # scripted group (container) (typed FeaturePython)
  n = 9
  ref = C_element
FEATURE [App::DocumentObjectGroupPython] H_element071  label="H_element : 033"  # scripted group (container) (typed FeaturePython)
  n = 10
  ref = H_element
FEATURE [App::DocumentObjectGroupPython] G4_PLASTIC_SC_VINYLTOLUENE  # scripted group (container) (typed FeaturePython)
  Dunit = g/cm3
  Dvalue = 1.032
  Group = -> [C_element077,H_element071]
  conduct = 2
  density = 1
  expand = 3
  formula = G4_PLASTIC_SC_VINYLTOLUENE
  name = G4_PLASTIC_SC_VINYLTOLUENE
  specific = 4
FEATURE [App::DocumentObjectGroupPython] Pu_element001  label="Pu_element : 1"  # scripted group (container) (typed FeaturePython)
  n = 1
  ref = Pu_element
FEATURE [App::DocumentObjectGroupPython] O_element076  label="O_element : 037"  # scripted group (container) (typed FeaturePython)
  n = 2
  ref = O_element
FEATURE [App::DocumentObjectGroupPython] G4_PLUTONIUM_DIOXIDE  # scripted group (container) (typed FeaturePython)
  Dunit = g/cm3
  Dvalue = 11.46
  Group = -> [Pu_element001,O_element076]
  conduct = 2
  density = 1
  expand = 3
  formula = G4_PLUTONIUM_DIOXIDE
  name = G4_PLUTONIUM_DIOXIDE
  specific = 4
FEATURE [App::DocumentObjectGroupPython] C_element078  label="C_element : 037"  # scripted group (container) (typed FeaturePython)
  n = 3
  ref = C_element
FEATURE [App::DocumentObjectGroupPython] H_element072  label="H_element : 034"  # scripted group (container) (typed FeaturePython)
  n = 3
  ref = H_element
FEATURE [App::DocumentObjectGroupPython] N_element036  label="N_element : 015"  # scripted group (container) (typed FeaturePython)
  n = 1
  ref = N_element
FEATURE [App::DocumentObjectGroupPython] G4_POLYACRYLONITRILE  # scripted group (container) (typed FeaturePython)
  Dunit = g/cm3
  Dvalue = 1.17
  Group = -> [C_element078,H_element072,N_element036]
  conduct = 2
  density = 1
  expand = 3
  formula = G4_POLYACRYLONITRILE
  name = G4_POLYACRYLONITRILE
  specific = 4
FEATURE [App::DocumentObjectGroupPython] C_element079  label="C_element : 16"  # scripted group (container) (typed FeaturePython)
  n = 16
  ref = C_element
FEATURE [App::DocumentObjectGroupPython] H_element073  label="H_element : 035"  # scripted group (container) (typed FeaturePython)
  n = 14
  ref = H_element
FEATURE [App::DocumentObjectGroupPython] O_element077  label="O_element : 038"  # scripted group (container) (typed FeaturePython)
  n = 3
  ref = O_element
FEATURE [App::DocumentObjectGroupPython] G4_POLYCARBONATE  # scripted group (container) (typed FeaturePython)
  Dunit = g/cm3
  Dvalue = 1.2
  Group = -> [C_element079,H_element073,O_element077]
  conduct = 2
  density = 1
  expand = 3
  formula = G4_POLYCARBONATE
  name = G4_POLYCARBONATE
  specific = 4
FEATURE [App::DocumentObjectGroupPython] C_element080  label="C_element : 038"  # scripted group (container) (typed FeaturePython)
  n = 8
  ref = C_element
FEATURE [App::DocumentObjectGroupPython] H_element074  label="H_element : 036"  # scripted group (container) (typed FeaturePython)
  n = 7
  ref = H_element
FEATURE [App::DocumentObjectGroupPython] Cl_element017  label="Cl_element : 007"  # scripted group (container) (typed FeaturePython)
  n = 1
  ref = Cl_element
FEATURE [App::DocumentObjectGroupPython] G4_POLYCHLOROSTYRENE  # scripted group (container) (typed FeaturePython)
  Dunit = g/cm3
  Dvalue = 1.3
  Group = -> [C_element080,H_element074,Cl_element017]
  conduct = 2
  density = 1
  expand = 3
  formula = G4_POLYCHLOROSTYRENE
  name = G4_POLYCHLOROSTYRENE
  specific = 4
FEATURE [App::DocumentObjectGroupPython] C_element081  label="C_element : 039"  # scripted group (container) (typed FeaturePython)
  n = 1
  ref = C_element
FEATURE [App::DocumentObjectGroupPython] H_element075  label="H_element : 037"  # scripted group (container) (typed FeaturePython)
  n = 2
  ref = H_element
FEATURE [App::DocumentObjectGroupPython] G4_POLYETHYLENE  # scripted group (container) (typed FeaturePython)
  Dunit = g/cm3
  Dvalue = 0.94
  Group = -> [C_element081,H_element075]
  conduct = 2
  density = 1
  expand = 3
  formula = G4_POLYETHYLENE
  name = G4_POLYETHYLENE
  specific = 4
FEATURE [App::DocumentObjectGroupPython] C_element082  label="C_element : 040"  # scripted group (container) (typed FeaturePython)
  n = 10
  ref = C_element
FEATURE [App::DocumentObjectGroupPython] H_element076  label="H_element : 038"  # scripted group (container) (typed FeaturePython)
  n = 8
  ref = H_element
FEATURE [App::DocumentObjectGroupPython] O_element078  label="O_element : 039"  # scripted group (container) (typed FeaturePython)
  n = 4
  ref = O_element
FEATURE [App::DocumentObjectGroupPython] G4_MYLAR  # scripted group (container) (typed FeaturePython)
  Dunit = g/cm3
  Dvalue = 1.4
  Group = -> [C_element082,H_element076,O_element078]
  conduct = 2
  density = 1
  expand = 3
  formula = G4_MYLAR
  name = G4_MYLAR
  specific = 4
FEATURE [App::DocumentObjectGroupPython] C_element083  label="C_element : 041"  # scripted group (container) (typed FeaturePython)
  n = 5
  ref = C_element
FEATURE [App::DocumentObjectGroupPython] H_element077  label="H_element : 039"  # scripted group (container) (typed FeaturePython)
  n = 8
  ref = H_element
FEATURE [App::DocumentObjectGroupPython] O_element079  label="O_element : 040"  # scripted group (container) (typed FeaturePython)
  n = 2
  ref = O_element
FEATURE [App::DocumentObjectGroupPython] G4_PLEXIGLASS  # scripted group (container) (typed FeaturePython)
  Dunit = g/cm3
  Dvalue = 1.19
  Group = -> [C_element083,H_element077,O_element079]
  conduct = 2
  density = 1
  expand = 3
  formula = G4_PLEXIGLASS
  name = G4_PLEXIGLASS
  specific = 4
FEATURE [App::DocumentObjectGroupPython] C_element084  label="C_element : 042"  # scripted group (container) (typed FeaturePython)
  n = 1
  ref = C_element
FEATURE [App::DocumentObjectGroupPython] H_element078  label="H_element : 040"  # scripted group (container) (typed FeaturePython)
  n = 2
  ref = H_element
FEATURE [App::DocumentObjectGroupPython] O_element080  label="O_element : 041"  # scripted group (container) (typed FeaturePython)
  n = 1
  ref = O_element
FEATURE [App::DocumentObjectGroupPython] G4_POLYOXYMETHYLENE  # scripted group (container) (typed FeaturePython)
  Dunit = g/cm3
  Dvalue = 1.425
  Group = -> [C_element084,H_element078,O_element080]
  conduct = 2
  density = 1
  expand = 3
  formula = G4_POLYOXYMETHYLENE
  name = G4_POLYOXYMETHYLENE
  specific = 4
FEATURE [App::DocumentObjectGroupPython] C_element085  label="C_element : 043"  # scripted group (container) (typed FeaturePython)
  n = 2
  ref = C_element
FEATURE [App::DocumentObjectGroupPython] H_element079  label="H_element : 041"  # scripted group (container) (typed FeaturePython)
  n = 4
  ref = H_element
FEATURE [App::DocumentObjectGroupPython] G4_POLYPROPYLENE  # scripted group (container) (typed FeaturePython)
  Dunit = g/cm3
  Dvalue = 0.9
  Group = -> [C_element085,H_element079]
  conduct = 2
  density = 1
  expand = 3
  formula = G4_POLYPROPYLENE
  name = G4_POLYPROPYLENE
  specific = 4
FEATURE [App::DocumentObjectGroupPython] C_element086  label="C_element : 044"  # scripted group (container) (typed FeaturePython)
  n = 8
  ref = C_element
FEATURE [App::DocumentObjectGroupPython] H_element080  label="H_element : 042"  # scripted group (container) (typed FeaturePython)
  n = 8
  ref = H_element
FEATURE [App::DocumentObjectGroupPython] G4_POLYSTYRENE  # scripted group (container) (typed FeaturePython)
  Dunit = g/cm3
  Dvalue = 1.06
  Group = -> [C_element086,H_element080]
  conduct = 2
  density = 1
  expand = 3
  formula = G4_POLYSTYRENE
  name = G4_POLYSTYRENE
  specific = 4
FEATURE [App::DocumentObjectGroupPython] C_element087  label="C_element : 045"  # scripted group (container) (typed FeaturePython)
  n = 2
  ref = C_element
FEATURE [App::DocumentObjectGroupPython] F_element014  label="F_element : 4"  # scripted group (container) (typed FeaturePython)
  n = 4
  ref = F_element
FEATURE [App::DocumentObjectGroupPython] G4_TEFLON  # scripted group (container) (typed FeaturePython)
  Dunit = g/cm3
  Dvalue = 2.2
  Group = -> [C_element087,F_element014]
  conduct = 2
  density = 1
  expand = 3
  formula = G4_TEFLON
  name = G4_TEFLON
  specific = 4
FEATURE [App::DocumentObjectGroupPython] C_element088  label="C_element : 046"  # scripted group (container) (typed FeaturePython)
  n = 2
  ref = C_element
FEATURE [App::DocumentObjectGroupPython] F_element015  label="F_element : 006"  # scripted group (container) (typed FeaturePython)
  n = 3
  ref = F_element
FEATURE [App::DocumentObjectGroupPython] Cl_element018  label="Cl_element : 008"  # scripted group (container) (typed FeaturePython)
  n = 1
  ref = Cl_element
FEATURE [App::DocumentObjectGroupPython] G4_POLYTRIFLUOROCHLOROETHYLENE  # scripted group (container) (typed FeaturePython)
  Dunit = g/cm3
  Dvalue = 2.1
  Group = -> [C_element088,F_element015,Cl_element018]
  conduct = 2
  density = 1
  expand = 3
  formula = G4_POLYTRIFLUOROCHLOROETHYLENE
  name = G4_POLYTRIFLUOROCHLOROETHYLENE
  specific = 4
FEATURE [App::DocumentObjectGroupPython] C_element089  label="C_element : 047"  # scripted group (container) (typed FeaturePython)
  n = 4
  ref = C_element
FEATURE [App::DocumentObjectGroupPython] H_element081  label="H_element : 043"  # scripted group (container) (typed FeaturePython)
  n = 6
  ref = H_element
FEATURE [App::DocumentObjectGroupPython] O_element081  label="O_element : 042"  # scripted group (container) (typed FeaturePython)
  n = 2
  ref = O_element
FEATURE [App::DocumentObjectGroupPython] G4_POLYVINYL_ACETATE  # scripted group (container) (typed FeaturePython)
  Dunit = g/cm3
  Dvalue = 1.19
  Group = -> [C_element089,H_element081,O_element081]
  conduct = 2
  density = 1
  expand = 3
  formula = G4_POLYVINYL_ACETATE
  name = G4_POLYVINYL_ACETATE
  specific = 4
FEATURE [App::DocumentObjectGroupPython] C_element090  label="C_element : 048"  # scripted group (container) (typed FeaturePython)
  n = 2
  ref = C_element
FEATURE [App::DocumentObjectGroupPython] H_element082  label="H_element : 044"  # scripted group (container) (typed FeaturePython)
  n = 4
  ref = H_element
FEATURE [App::DocumentObjectGroupPython] O_element082  label="O_element : 043"  # scripted group (container) (typed FeaturePython)
  n = 1
  ref = O_element
FEATURE [App::DocumentObjectGroupPython] G4_POLYVINYL_ALCOHOL  # scripted group (container) (typed FeaturePython)
  Dunit = g/cm3
  Dvalue = 1.3
  Group = -> [C_element090,H_element082,O_element082]
  conduct = 2
  density = 1
  expand = 3
  formula = G4_POLYVINYL_ALCOHOL
  name = G4_POLYVINYL_ALCOHOL
  specific = 4
FEATURE [App::DocumentObjectGroupPython] C_element091  label="C_element : 049"  # scripted group (container) (typed FeaturePython)
  n = 8
  ref = C_element
FEATURE [App::DocumentObjectGroupPython] H_element083  label="H_element : 045"  # scripted group (container) (typed FeaturePython)
  n = 14
  ref = H_element
FEATURE [App::DocumentObjectGroupPython] O_element083  label="O_element : 044"  # scripted group (container) (typed FeaturePython)
  n = 2
  ref = O_element
FEATURE [App::DocumentObjectGroupPython] G4_POLYVINYL_BUTYRAL  # scripted group (container) (typed FeaturePython)
  Dunit = g/cm3
  Dvalue = 1.12
  Group = -> [C_element091,H_element083,O_element083]
  conduct = 2
  density = 1
  expand = 3
  formula = G4_POLYVINYL_BUTYRAL
  name = G4_POLYVINYL_BUTYRAL
  specific = 4
FEATURE [App::DocumentObjectGroupPython] C_element092  label="C_element : 050"  # scripted group (container) (typed FeaturePython)
  n = 2
  ref = C_element
FEATURE [App::DocumentObjectGroupPython] H_element084  label="H_element : 046"  # scripted group (container) (typed FeaturePython)
  n = 3
  ref = H_element
FEATURE [App::DocumentObjectGroupPython] Cl_element019  label="Cl_element : 009"  # scripted group (container) (typed FeaturePython)
  n = 1
  ref = Cl_element
FEATURE [App::DocumentObjectGroupPython] G4_POLYVINYL_CHLORIDE  # scripted group (container) (typed FeaturePython)
  Dunit = g/cm3
  Dvalue = 1.3
  Group = -> [C_element092,H_element084,Cl_element019]
  conduct = 2
  density = 1
  expand = 3
  formula = G4_POLYVINYL_CHLORIDE
  name = G4_POLYVINYL_CHLORIDE
  specific = 4
FEATURE [App::DocumentObjectGroupPython] C_element093  label="C_element : 051"  # scripted group (container) (typed FeaturePython)
  n = 2
  ref = C_element
FEATURE [App::DocumentObjectGroupPython] H_element085  label="H_element : 047"  # scripted group (container) (typed FeaturePython)
  n = 2
  ref = H_element
FEATURE [App::DocumentObjectGroupPython] Cl_element020  label="Cl_element : 010"  # scripted group (container) (typed FeaturePython)
  n = 2
  ref = Cl_element
FEATURE [App::DocumentObjectGroupPython] G4_POLYVINYLIDENE_CHLORIDE  # scripted group (container) (typed FeaturePython)
  Dunit = g/cm3
  Dvalue = 1.7
  Group = -> [C_element093,H_element085,Cl_element020]
  conduct = 2
  density = 1
  expand = 3
  formula = G4_POLYVINYLIDENE_CHLORIDE
  name = G4_POLYVINYLIDENE_CHLORIDE
  specific = 4
FEATURE [App::DocumentObjectGroupPython] C_element094  label="C_element : 052"  # scripted group (container) (typed FeaturePython)
  n = 2
  ref = C_element
FEATURE [App::DocumentObjectGroupPython] H_element086  label="H_element : 048"  # scripted group (container) (typed FeaturePython)
  n = 2
  ref = H_element
FEATURE [App::DocumentObjectGroupPython] F_element016  label="F_element : 007"  # scripted group (container) (typed FeaturePython)
  n = 2
  ref = F_element
FEATURE [App::DocumentObjectGroupPython] G4_POLYVINYLIDENE_FLUORIDE  # scripted group (container) (typed FeaturePython)
  Dunit = g/cm3
  Dvalue = 1.76
  Group = -> [C_element094,H_element086,F_element016]
  conduct = 2
  density = 1
  expand = 3
  formula = G4_POLYVINYLIDENE_FLUORIDE
  name = G4_POLYVINYLIDENE_FLUORIDE
  specific = 4
FEATURE [App::DocumentObjectGroupPython] C_element095  label="C_element : 053"  # scripted group (container) (typed FeaturePython)
  n = 6
  ref = C_element
FEATURE [App::DocumentObjectGroupPython] H_element087  label="H_element : 9"  # scripted group (container) (typed FeaturePython)
  n = 9
  ref = H_element
FEATURE [App::DocumentObjectGroupPython] N_element037  label="N_element : 016"  # scripted group (container) (typed FeaturePython)
  n = 1
  ref = N_element
FEATURE [App::DocumentObjectGroupPython] O_element084  label="O_element : 045"  # scripted group (container) (typed FeaturePython)
  n = 1
  ref = O_element
FEATURE [App::DocumentObjectGroupPython] G4_POLYVINYL_PYRROLIDONE  # scripted group (container) (typed FeaturePython)
  Dunit = g/cm3
  Dvalue = 1.25
  Group = -> [C_element095,H_element087,N_element037,O_element084]
  conduct = 2
  density = 1
  expand = 3
  formula = G4_POLYVINYL_PYRROLIDONE
  name = G4_POLYVINYL_PYRROLIDONE
  specific = 4
FEATURE [App::DocumentObjectGroupPython] K_element008  label="K_element : 1"  # scripted group (container) (typed FeaturePython)
  n = 1
  ref = K_element
FEATURE [App::DocumentObjectGroupPython] I_element006  label="I_element : 003"  # scripted group (container) (typed FeaturePython)
  n = 1
  ref = I_element
FEATURE [App::DocumentObjectGroupPython] G4_POTASSIUM_IODIDE  # scripted group (container) (typed FeaturePython)
  Dunit = g/cm3
  Dvalue = 3.13
  Group = -> [K_element008,I_element006]
  conduct = 2
  density = 1
  expand = 3
  formula = G4_POTASSIUM_IODIDE
  name = G4_POTASSIUM_IODIDE
  specific = 4
FEATURE [App::DocumentObjectGroupPython] K_element009  label="K_element : 2"  # scripted group (container) (typed FeaturePython)
  n = 2
  ref = K_element
FEATURE [App::DocumentObjectGroupPython] O_element085  label="O_element : 046"  # scripted group (container) (typed FeaturePython)
  n = 1
  ref = O_element
FEATURE [App::DocumentObjectGroupPython] G4_POTASSIUM_OXIDE  # scripted group (container) (typed FeaturePython)
  Dunit = g/cm3
  Dvalue = 2.32
  Group = -> [K_element009,O_element085]
  conduct = 2
  density = 1
  expand = 3
  formula = G4_POTASSIUM_OXIDE
  name = G4_POTASSIUM_OXIDE
  specific = 4
FEATURE [App::DocumentObjectGroupPython] C_element096  label="C_element : 054"  # scripted group (container) (typed FeaturePython)
  n = 3
  ref = C_element
FEATURE [App::DocumentObjectGroupPython] H_element088  label="H_element : 049"  # scripted group (container) (typed FeaturePython)
  n = 8
  ref = H_element
FEATURE [App::DocumentObjectGroupPython] G4_PROPANE  # scripted group (container) (typed FeaturePython)
  Dunit = g/cm3
  Dvalue = 0.00187939
  Group = -> [C_element096,H_element088]
  conduct = 2
  density = 1
  expand = 3
  formula = G4_PROPANE
  name = G4_PROPANE
  specific = 4
FEATURE [App::DocumentObjectGroupPython] C_element097  label="C_element : 055"  # scripted group (container) (typed FeaturePython)
  n = 3
  ref = C_element
FEATURE [App::DocumentObjectGroupPython] H_element089  label="H_element : 050"  # scripted group (container) (typed FeaturePython)
  n = 8
  ref = H_element
FEATURE [App::DocumentObjectGroupPython] G4_lPROPANE  # scripted group (container) (typed FeaturePython)
  Dunit = g/cm3
  Dvalue = 0.43
  Group = -> [C_element097,H_element089]
  conduct = 2
  density = 1
  expand = 3
  formula = G4_lPROPANE
  name = G4_lPROPANE
  specific = 4
FEATURE [App::DocumentObjectGroupPython] C_element098  label="C_element : 056"  # scripted group (container) (typed FeaturePython)
  n = 3
  ref = C_element
FEATURE [App::DocumentObjectGroupPython] H_element090  label="H_element : 051"  # scripted group (container) (typed FeaturePython)
  n = 8
  ref = H_element
FEATURE [App::DocumentObjectGroupPython] O_element086  label="O_element : 047"  # scripted group (container) (typed FeaturePython)
  n = 1
  ref = O_element
FEATURE [App::DocumentObjectGroupPython] G4_N_PROPYL_ALCOHOL  label="G4_N-PROPYL_ALCOHOL"  # scripted group (container) (typed FeaturePython)
  Dunit = g/cm3
  Dvalue = 0.8035
  Group = -> [C_element098,H_element090,O_element086]
  conduct = 2
  density = 1
  expand = 3
  formula = G4_N-PROPYL_ALCOHOL
  name = G4_N-PROPYL_ALCOHOL
  specific = 4
FEATURE [App::DocumentObjectGroupPython] C_element099  label="C_element : 057"  # scripted group (container) (typed FeaturePython)
  n = 5
  ref = C_element
FEATURE [App::DocumentObjectGroupPython] H_element091  label="H_element : 052"  # scripted group (container) (typed FeaturePython)
  n = 5
  ref = H_element
FEATURE [App::DocumentObjectGroupPython] N_element038  label="N_element : 017"  # scripted group (container) (typed FeaturePython)
  n = 1
  ref = N_element
FEATURE [App::DocumentObjectGroupPython] G4_PYRIDINE  # scripted group (container) (typed FeaturePython)
  Dunit = g/cm3
  Dvalue = 0.9819
  Group = -> [C_element099,H_element091,N_element038]
  conduct = 2
  density = 1
  expand = 3
  formula = G4_PYRIDINE
  name = G4_PYRIDINE
  specific = 4
FEATURE [App::DocumentObjectGroupPython] H_element092  label="H_element : 0.144"  # scripted group (container) (typed FeaturePython)
  n = 0.143711
FEATURE [App::DocumentObjectGroupPython] C_element100  label="C_element : 0.856"  # scripted group (container) (typed FeaturePython)
  n = 0.856289
FEATURE [App::DocumentObjectGroupPython] G4_RUBBER_BUTYL  # scripted group (container) (typed FeaturePython)
  Dunit = g/cm3
  Dvalue = 0.92
  Group = -> [H_element092,C_element100]
  conduct = 2
  density = 1
  expand = 3
  formula = G4_RUBBER_BUTYL
  name = G4_RUBBER_BUTYL
  specific = 4
FEATURE [App::DocumentObjectGroupPython] H_element093  label="H_element : 0.118"  # scripted group (container) (typed FeaturePython)
  n = 0.118371
FEATURE [App::DocumentObjectGroupPython] C_element101  label="C_element : 0.882"  # scripted group (container) (typed FeaturePython)
  n = 0.881629
FEATURE [App::DocumentObjectGroupPython] G4_RUBBER_NATURAL  # scripted group (container) (typed FeaturePython)
  Dunit = g/cm3
  Dvalue = 0.92
  Group = -> [H_element093,C_element101]
  conduct = 2
  density = 1
  expand = 3
  formula = G4_RUBBER_NATURAL
  name = G4_RUBBER_NATURAL
  specific = 4
FEATURE [App::DocumentObjectGroupPython] H_element094  label="H_element : 0.145"  # scripted group (container) (typed FeaturePython)
  n = 0.05692
FEATURE [App::DocumentObjectGroupPython] C_element102  label="C_element : 0.543"  # scripted group (container) (typed FeaturePython)
  n = 0.542646
FEATURE [App::DocumentObjectGroupPython] Cl_element021  label="Cl_element : 0.400"  # scripted group (container) (typed FeaturePython)
  n = 0.400434
FEATURE [App::DocumentObjectGroupPython] G4_RUBBER_NEOPRENE  # scripted group (container) (typed FeaturePython)
  Dunit = g/cm3
  Dvalue = 1.23
  Group = -> [H_element094,C_element102,Cl_element021]
  conduct = 2
  density = 1
  expand = 3
  formula = G4_RUBBER_NEOPRENE
  name = G4_RUBBER_NEOPRENE
  specific = 4
FEATURE [App::DocumentObjectGroupPython] Si_element006  label="Si_element : 1"  # scripted group (container) (typed FeaturePython)
  n = 1
  ref = Si_element
FEATURE [App::DocumentObjectGroupPython] O_element087  label="O_element : 048"  # scripted group (container) (typed FeaturePython)
  n = 2
  ref = O_element
FEATURE [App::DocumentObjectGroupPython] G4_SILICON_DIOXIDE  # scripted group (container) (typed FeaturePython)
  Dunit = g/cm3
  Dvalue = 2.32
  Group = -> [Si_element006,O_element087]
  conduct = 2
  density = 1
  expand = 3
  formula = G4_SILICON_DIOXIDE
  name = G4_SILICON_DIOXIDE
  specific = 4
FEATURE [App::DocumentObjectGroupPython] Ag_element002  label="Ag_element : 1"  # scripted group (container) (typed FeaturePython)
  n = 1
  ref = Ag_element
FEATURE [App::DocumentObjectGroupPython] Br_element005  label="Br_element : 003"  # scripted group (container) (typed FeaturePython)
  n = 1
  ref = Br_element
FEATURE [App::DocumentObjectGroupPython] G4_SILVER_BROMIDE  # scripted group (container) (typed FeaturePython)
  Dunit = g/cm3
  Dvalue = 6.473
  Group = -> [Ag_element002,Br_element005]
  conduct = 2
  density = 1
  expand = 3
  formula = G4_SILVER_BROMIDE
  name = G4_SILVER_BROMIDE
  specific = 4
FEATURE [App::DocumentObjectGroupPython] Ag_element003  label="Ag_element : 002"  # scripted group (container) (typed FeaturePython)
  n = 1
  ref = Ag_element
FEATURE [App::DocumentObjectGroupPython] Cl_element022  label="Cl_element : 011"  # scripted group (container) (typed FeaturePython)
  n = 1
  ref = Cl_element
FEATURE [App::DocumentObjectGroupPython] G4_SILVER_CHLORIDE  # scripted group (container) (typed FeaturePython)
  Dunit = g/cm3
  Dvalue = 5.56
  Group = -> [Ag_element003,Cl_element022]
  conduct = 2
  density = 1
  expand = 3
  formula = G4_SILVER_CHLORIDE
  name = G4_SILVER_CHLORIDE
  specific = 4
FEATURE [App::DocumentObjectGroupPython] Br_element006  label="Br_element : 0.423"  # scripted group (container) (typed FeaturePython)
  n = 0.422895
FEATURE [App::DocumentObjectGroupPython] Ag_element004  label="Ag_element : 0.574"  # scripted group (container) (typed FeaturePython)
  n = 0.573748
FEATURE [App::DocumentObjectGroupPython] I_element007  label="I_element : 0.649"  # scripted group (container) (typed FeaturePython)
  n = 0.003357
FEATURE [App::DocumentObjectGroupPython] G4_SILVER_HALIDES  # scripted group (container) (typed FeaturePython)
  Dunit = g/cm3
  Dvalue = 6.47
  Group = -> [Br_element006,Ag_element004,I_element007]
  conduct = 2
  density = 1
  expand = 3
  formula = G4_SILVER_HALIDES
  name = G4_SILVER_HALIDES
  specific = 4
FEATURE [App::DocumentObjectGroupPython] Ag_element005  label="Ag_element : 003"  # scripted group (container) (typed FeaturePython)
  n = 1
  ref = Ag_element
FEATURE [App::DocumentObjectGroupPython] I_element008  label="I_element : 004"  # scripted group (container) (typed FeaturePython)
  n = 1
  ref = I_element
FEATURE [App::DocumentObjectGroupPython] G4_SILVER_IODIDE  # scripted group (container) (typed FeaturePython)
  Dunit = g/cm3
  Dvalue = 6.01
  Group = -> [Ag_element005,I_element008]
  conduct = 2
  density = 1
  expand = 3
  formula = G4_SILVER_IODIDE
  name = G4_SILVER_IODIDE
  specific = 4
FEATURE [App::DocumentObjectGroupPython] H_element095  label="H_element : 0.100"  # scripted group (container) (typed FeaturePython)
  n = 0.1
FEATURE [App::DocumentObjectGroupPython] C_element103  label="C_element : 0.204"  # scripted group (container) (typed FeaturePython)
  n = 0.204
FEATURE [App::DocumentObjectGroupPython] N_element039  label="N_element : 0.759"  # scripted group (container) (typed FeaturePython)
  n = 0.042
FEATURE [App::DocumentObjectGroupPython] O_element088  label="O_element : 0.645"  # scripted group (container) (typed FeaturePython)
  n = 0.645
FEATURE [App::DocumentObjectGroupPython] Na_element013  label="Na_element : 0.100"  # scripted group (container) (typed FeaturePython)
  n = 0.002
FEATURE [App::DocumentObjectGroupPython] P_element009  label="P_element : 0.107"  # scripted group (container) (typed FeaturePython)
  n = 0.001
FEATURE [App::DocumentObjectGroupPython] S_element020  label="S_element : 0.021"  # scripted group (container) (typed FeaturePython)
  n = 0.002
FEATURE [App::DocumentObjectGroupPython] Cl_element023  label="Cl_element : 0.590"  # scripted group (container) (typed FeaturePython)
  n = 0.003
FEATURE [App::DocumentObjectGroupPython] K_element010  label="K_element : 0.001"  # scripted group (container) (typed FeaturePython)
  n = 0.001
FEATURE [App::DocumentObjectGroupPython] G4_SKIN_ICRP  # scripted group (container) (typed FeaturePython)
  Dunit = g/cm3
  Dvalue = 1.09
  Group = -> [H_element095,C_element103,N_element039,O_element088,Na_element013,P_element009,S_element020,Cl_element023,K_element010]
  conduct = 2
  density = 1
  expand = 3
  formula = G4_SKIN_ICRP
  name = G4_SKIN_ICRP
  specific = 4
FEATURE [App::DocumentObjectGroupPython] Na_element014  label="Na_element : 2"  # scripted group (container) (typed FeaturePython)
  n = 2
  ref = Na_element
FEATURE [App::DocumentObjectGroupPython] C_element104  label="C_element : 058"  # scripted group (container) (typed FeaturePython)
  n = 1
  ref = C_element
FEATURE [App::DocumentObjectGroupPython] O_element089  label="O_element : 049"  # scripted group (container) (typed FeaturePython)
  n = 3
  ref = O_element
FEATURE [App::DocumentObjectGroupPython] G4_SODIUM_CARBONATE  # scripted group (container) (typed FeaturePython)
  Dunit = g/cm3
  Dvalue = 2.532
  Group = -> [Na_element014,C_element104,O_element089]
  conduct = 2
  density = 1
  expand = 3
  formula = G4_SODIUM_CARBONATE
  name = G4_SODIUM_CARBONATE
  specific = 4
FEATURE [App::DocumentObjectGroupPython] Na_element015  label="Na_element : 1"  # scripted group (container) (typed FeaturePython)
  n = 1
  ref = Na_element
FEATURE [App::DocumentObjectGroupPython] I_element009  label="I_element : 005"  # scripted group (container) (typed FeaturePython)
  n = 1
  ref = I_element
FEATURE [App::DocumentObjectGroupPython] G4_SODIUM_IODIDE  # scripted group (container) (typed FeaturePython)
  Dunit = g/cm3
  Dvalue = 3.667
  Group = -> [Na_element015,I_element009]
  conduct = 2
  density = 1
  expand = 3
  formula = G4_SODIUM_IODIDE
  name = G4_SODIUM_IODIDE
  specific = 4
FEATURE [App::DocumentObjectGroupPython] Na_element016  label="Na_element : 003"  # scripted group (container) (typed FeaturePython)
  n = 2
  ref = Na_element
FEATURE [App::DocumentObjectGroupPython] O_element090  label="O_element : 050"  # scripted group (container) (typed FeaturePython)
  n = 1
  ref = O_element
FEATURE [App::DocumentObjectGroupPython] G4_SODIUM_MONOXIDE  # scripted group (container) (typed FeaturePython)
  Dunit = g/cm3
  Dvalue = 2.27
  Group = -> [Na_element016,O_element090]
  conduct = 2
  density = 1
  expand = 3
  formula = G4_SODIUM_MONOXIDE
  name = G4_SODIUM_MONOXIDE
  specific = 4
FEATURE [App::DocumentObjectGroupPython] Na_element017  label="Na_element : 004"  # scripted group (container) (typed FeaturePython)
  n = 1
  ref = Na_element
FEATURE [App::DocumentObjectGroupPython] N_element040  label="N_element : 018"  # scripted group (container) (typed FeaturePython)
  n = 1
  ref = N_element
FEATURE [App::DocumentObjectGroupPython] O_element091  label="O_element : 051"  # scripted group (container) (typed FeaturePython)
  n = 3
  ref = O_element
FEATURE [App::DocumentObjectGroupPython] G4_SODIUM_NITRATE  # scripted group (container) (typed FeaturePython)
  Dunit = g/cm3
  Dvalue = 2.261
  Group = -> [Na_element017,N_element040,O_element091]
  conduct = 2
  density = 1
  expand = 3
  formula = G4_SODIUM_NITRATE
  name = G4_SODIUM_NITRATE
  specific = 4
FEATURE [App::DocumentObjectGroupPython] C_element105  label="C_element : 059"  # scripted group (container) (typed FeaturePython)
  n = 14
  ref = C_element
FEATURE [App::DocumentObjectGroupPython] H_element096  label="H_element : 053"  # scripted group (container) (typed FeaturePython)
  n = 12
  ref = H_element
FEATURE [App::DocumentObjectGroupPython] G4_STILBENE  # scripted group (container) (typed FeaturePython)
  Dunit = g/cm3
  Dvalue = 0.9707
  Group = -> [C_element105,H_element096]
  conduct = 2
  density = 1
  expand = 3
  formula = G4_STILBENE
  name = G4_STILBENE
  specific = 4
FEATURE [App::DocumentObjectGroupPython] C_element106  label="C_element : 12"  # scripted group (container) (typed FeaturePython)
  n = 12
  ref = C_element
FEATURE [App::DocumentObjectGroupPython] H_element097  label="H_element : 22"  # scripted group (container) (typed FeaturePython)
  n = 22
  ref = H_element
FEATURE [App::DocumentObjectGroupPython] O_element092  label="O_element : 11"  # scripted group (container) (typed FeaturePython)
  n = 11
  ref = O_element
FEATURE [App::DocumentObjectGroupPython] G4_SUCROSE  # scripted group (container) (typed FeaturePython)
  Dunit = g/cm3
  Dvalue = 1.5805
  Group = -> [C_element106,H_element097,O_element092]
  conduct = 2
  density = 1
  expand = 3
  formula = G4_SUCROSE
  name = G4_SUCROSE
  specific = 4
FEATURE [App::DocumentObjectGroupPython] C_element107  label="C_element : 18"  # scripted group (container) (typed FeaturePython)
  n = 18
  ref = C_element
FEATURE [App::DocumentObjectGroupPython] H_element098  label="H_element : 054"  # scripted group (container) (typed FeaturePython)
  n = 14
  ref = H_element
FEATURE [App::DocumentObjectGroupPython] G4_TERPHENYL  # scripted group (container) (typed FeaturePython)
  Dunit = g/cm3
  Dvalue = 1.24
  Group = -> [C_element107,H_element098]
  conduct = 2
  density = 1
  expand = 3
  formula = G4_TERPHENYL
  name = G4_TERPHENYL
  specific = 4
FEATURE [App::DocumentObjectGroupPython] H_element099  label="H_element : 0.146"  # scripted group (container) (typed FeaturePython)
  n = 0.106
FEATURE [App::DocumentObjectGroupPython] C_element108  label="C_element : 0.883"  # scripted group (container) (typed FeaturePython)
  n = 0.099
FEATURE [App::DocumentObjectGroupPython] N_element041  label="N_element : 0.020"  # scripted group (container) (typed FeaturePython)
  n = 0.02
FEATURE [App::DocumentObjectGroupPython] O_element093  label="O_element : 0.766"  # scripted group (container) (typed FeaturePython)
  n = 0.766
FEATURE [App::DocumentObjectGroupPython] Na_element018  label="Na_element : 0.101"  # scripted group (container) (typed FeaturePython)
  n = 0.002
FEATURE [App::DocumentObjectGroupPython] P_element010  label="P_element : 0.108"  # scripted group (container) (typed FeaturePython)
  n = 0.001
FEATURE [App::DocumentObjectGroupPython] S_element021  label="S_element : 0.022"  # scripted group (container) (typed FeaturePython)
  n = 0.002
FEATURE [App::DocumentObjectGroupPython] Cl_element024  label="Cl_element : 0.002"  # scripted group (container) (typed FeaturePython)
  n = 0.002
FEATURE [App::DocumentObjectGroupPython] K_element011  label="K_element : 0.017"  # scripted group (container) (typed FeaturePython)
  n = 0.002
FEATURE [App::DocumentObjectGroupPython] G4_TESTIS_ICRP  # scripted group (container) (typed FeaturePython)
  Dunit = g/cm3
  Dvalue = 1.04
  Group = -> [H_element099,C_element108,N_element041,O_element093,Na_element018,P_element010,S_element021,Cl_element024,K_element011]
  conduct = 2
  density = 1
  expand = 3
  formula = G4_TESTIS_ICRP
  name = G4_TESTIS_ICRP
  specific = 4
FEATURE [App::DocumentObjectGroupPython] C_element109  label="C_element : 060"  # scripted group (container) (typed FeaturePython)
  n = 2
  ref = C_element
FEATURE [App::DocumentObjectGroupPython] Cl_element025  label="Cl_element : 012"  # scripted group (container) (typed FeaturePython)
  n = 4
  ref = Cl_element
FEATURE [App::DocumentObjectGroupPython] G4_TETRACHLOROETHYLENE  # scripted group (container) (typed FeaturePython)
  Dunit = g/cm3
  Dvalue = 1.625
  Group = -> [C_element109,Cl_element025]
  conduct = 2
  density = 1
  expand = 3
  formula = G4_TETRACHLOROETHYLENE
  name = G4_TETRACHLOROETHYLENE
  specific = 4
FEATURE [App::DocumentObjectGroupPython] Tl_element001  label="Tl_element : 1"  # scripted group (container) (typed FeaturePython)
  n = 1
  ref = Tl_element
FEATURE [App::DocumentObjectGroupPython] Cl_element026  label="Cl_element : 013"  # scripted group (container) (typed FeaturePython)
  n = 1
  ref = Cl_element
FEATURE [App::DocumentObjectGroupPython] G4_THALLIUM_CHLORIDE  # scripted group (container) (typed FeaturePython)
  Dunit = g/cm3
  Dvalue = 7.004
  Group = -> [Tl_element001,Cl_element026]
  conduct = 2
  density = 1
  expand = 3
  formula = G4_THALLIUM_CHLORIDE
  name = G4_THALLIUM_CHLORIDE
  specific = 4
FEATURE [App::DocumentObjectGroupPython] H_element100  label="H_element : 0.147"  # scripted group (container) (typed FeaturePython)
  n = 0.105
FEATURE [App::DocumentObjectGroupPython] C_element110  label="C_element : 0.256"  # scripted group (container) (typed FeaturePython)
  n = 0.256
FEATURE [App::DocumentObjectGroupPython] N_element042  label="N_element : 0.760"  # scripted group (container) (typed FeaturePython)
  n = 0.027
FEATURE [App::DocumentObjectGroupPython] O_element094  label="O_element : 0.602"  # scripted group (container) (typed FeaturePython)
  n = 0.602
FEATURE [App::DocumentObjectGroupPython] Na_element019  label="Na_element : 0.102"  # scripted group (container) (typed FeaturePython)
  n = 0.001
FEATURE [App::DocumentObjectGroupPython] P_element011  label="P_element : 0.109"  # scripted group (container) (typed FeaturePython)
  n = 0.002
FEATURE [App::DocumentObjectGroupPython] S_element022  label="S_element : 0.023"  # scripted group (container) (typed FeaturePython)
  n = 0.003
FEATURE [App::DocumentObjectGroupPython] Cl_element027  label="Cl_element : 0.591"  # scripted group (container) (typed FeaturePython)
  n = 0.002
FEATURE [App::DocumentObjectGroupPython] K_element012  label="K_element : 0.018"  # scripted group (container) (typed FeaturePython)
  n = 0.002
FEATURE [App::DocumentObjectGroupPython] G4_TISSUE_SOFT_ICRP  # scripted group (container) (typed FeaturePython)
  Dunit = g/cm3
  Dvalue = 1.03
  Group = -> [H_element100,C_element110,N_element042,O_element094,Na_element019,P_element011,S_element022,Cl_element027,K_element012]
  conduct = 2
  density = 1
  expand = 3
  formula = G4_TISSUE_SOFT_ICRP
  name = G4_TISSUE_SOFT_ICRP
  specific = 4
FEATURE [App::DocumentObjectGroupPython] H_element101  label="H_element : 0.148"  # scripted group (container) (typed FeaturePython)
  n = 0.101
FEATURE [App::DocumentObjectGroupPython] C_element111  label="C_element : 0.111"  # scripted group (container) (typed FeaturePython)
  n = 0.111
FEATURE [App::DocumentObjectGroupPython] N_element043  label="N_element : 0.026"  # scripted group (container) (typed FeaturePython)
  n = 0.026
FEATURE [App::DocumentObjectGroupPython] O_element095  label="O_element : 0.762"  # scripted group (container) (typed FeaturePython)
  n = 0.762
FEATURE [App::DocumentObjectGroupPython] G4_TISSUE_SOFT_ICRU_4  label="G4_TISSUE_SOFT_ICRU-4"  # scripted group (container) (typed FeaturePython)
  Dunit = g/cm3
  Dvalue = 1
  Group = -> [H_element101,C_element111,N_element043,O_element095]
  conduct = 2
  density = 1
  expand = 3
  formula = G4_TISSUE_SOFT_ICRU-4
  name = G4_TISSUE_SOFT_ICRU-4
  specific = 4
FEATURE [App::DocumentObjectGroupPython] H_element102  label="H_element : 0.149"  # scripted group (container) (typed FeaturePython)
  n = 0.101869
FEATURE [App::DocumentObjectGroupPython] C_element112  label="C_element : 0.456"  # scripted group (container) (typed FeaturePython)
  n = 0.456179
FEATURE [App::DocumentObjectGroupPython] N_element044  label="N_element : 0.761"  # scripted group (container) (typed FeaturePython)
  n = 0.035172
FEATURE [App::DocumentObjectGroupPython] O_element096  label="O_element : 0.407"  # scripted group (container) (typed FeaturePython)
  n = 0.40678
FEATURE [App::DocumentObjectGroupPython] G4_TISSUE_METHANE  label="G4_TISSUE-METHANE"  # scripted group (container) (typed FeaturePython)
  Dunit = g/cm3
  Dvalue = 0.00106409
  Group = -> [H_element102,C_element112,N_element044,O_element096]
  conduct = 2
  density = 1
  expand = 3
  formula = G4_TISSUE-METHANE
  name = G4_TISSUE-METHANE
  specific = 4
FEATURE [App::DocumentObjectGroupPython] H_element103  label="H_element : 0.103"  # scripted group (container) (typed FeaturePython)
  n = 0.102672
FEATURE [App::DocumentObjectGroupPython] C_element113  label="C_element : 0.569"  # scripted group (container) (typed FeaturePython)
  n = 0.56894
FEATURE [App::DocumentObjectGroupPython] N_element045  label="N_element : 0.762"  # scripted group (container) (typed FeaturePython)
  n = 0.035022
FEATURE [App::DocumentObjectGroupPython] O_element097  label="O_element : 0.293"  # scripted group (container) (typed FeaturePython)
  n = 0.293366
FEATURE [App::DocumentObjectGroupPython] G4_TISSUE_PROPANE  label="G4_TISSUE-PROPANE"  # scripted group (container) (typed FeaturePython)
  Dunit = g/cm3
  Dvalue = 0.00182628
  Group = -> [H_element103,C_element113,N_element045,O_element097]
  conduct = 2
  density = 1
  expand = 3
  formula = G4_TISSUE-PROPANE
  name = G4_TISSUE-PROPANE
  specific = 4
FEATURE [App::DocumentObjectGroupPython] Ti_element003  label="Ti_element : 1"  # scripted group (container) (typed FeaturePython)
  n = 1
  ref = Ti_element
FEATURE [App::DocumentObjectGroupPython] O_element098  label="O_element : 052"  # scripted group (container) (typed FeaturePython)
  n = 2
  ref = O_element
FEATURE [App::DocumentObjectGroupPython] G4_TITANIUM_DIOXIDE  # scripted group (container) (typed FeaturePython)
  Dunit = g/cm3
  Dvalue = 4.26
  Group = -> [Ti_element003,O_element098]
  conduct = 2
  density = 1
  expand = 3
  formula = G4_TITANIUM_DIOXIDE
  name = G4_TITANIUM_DIOXIDE
  specific = 4
FEATURE [App::DocumentObjectGroupPython] C_element114  label="C_element : 061"  # scripted group (container) (typed FeaturePython)
  n = 7
  ref = C_element
FEATURE [App::DocumentObjectGroupPython] H_element104  label="H_element : 055"  # scripted group (container) (typed FeaturePython)
  n = 8
  ref = H_element
FEATURE [App::DocumentObjectGroupPython] G4_TOLUENE  # scripted group (container) (typed FeaturePython)
  Dunit = g/cm3
  Dvalue = 0.8669
  Group = -> [C_element114,H_element104]
  conduct = 2
  density = 1
  expand = 3
  formula = G4_TOLUENE
  name = G4_TOLUENE
  specific = 4
FEATURE [App::DocumentObjectGroupPython] C_element115  label="C_element : 062"  # scripted group (container) (typed FeaturePython)
  n = 2
  ref = C_element
FEATURE [App::DocumentObjectGroupPython] H_element105  label="H_element : 056"  # scripted group (container) (typed FeaturePython)
  n = 1
  ref = H_element
FEATURE [App::DocumentObjectGroupPython] Cl_element028  label="Cl_element : 014"  # scripted group (container) (typed FeaturePython)
  n = 3
  ref = Cl_element
FEATURE [App::DocumentObjectGroupPython] G4_TRICHLOROETHYLENE  # scripted group (container) (typed FeaturePython)
  Dunit = g/cm3
  Dvalue = 1.46
  Group = -> [C_element115,H_element105,Cl_element028]
  conduct = 2
  density = 1
  expand = 3
  formula = G4_TRICHLOROETHYLENE
  name = G4_TRICHLOROETHYLENE
  specific = 4
FEATURE [App::DocumentObjectGroupPython] C_element116  label="C_element : 063"  # scripted group (container) (typed FeaturePython)
  n = 6
  ref = C_element
FEATURE [App::DocumentObjectGroupPython] H_element106  label="H_element : 15"  # scripted group (container) (typed FeaturePython)
  n = 15
  ref = H_element
FEATURE [App::DocumentObjectGroupPython] O_element099  label="O_element : 053"  # scripted group (container) (typed FeaturePython)
  n = 4
  ref = O_element
FEATURE [App::DocumentObjectGroupPython] P_element012  label="P_element : 1"  # scripted group (container) (typed FeaturePython)
  n = 1
  ref = P_element
FEATURE [App::DocumentObjectGroupPython] G4_TRIETHYL_PHOSPHATE  # scripted group (container) (typed FeaturePython)
  Dunit = g/cm3
  Dvalue = 1.07
  Group = -> [C_element116,H_element106,O_element099,P_element012]
  conduct = 2
  density = 1
  expand = 3
  formula = G4_TRIETHYL_PHOSPHATE
  name = G4_TRIETHYL_PHOSPHATE
  specific = 4
FEATURE [App::DocumentObjectGroupPython] W_element003  label="W_element : 003"  # scripted group (container) (typed FeaturePython)
  n = 1
  ref = W_element
FEATURE [App::DocumentObjectGroupPython] F_element017  label="F_element : 6"  # scripted group (container) (typed FeaturePython)
  n = 6
  ref = F_element
FEATURE [App::DocumentObjectGroupPython] G4_TUNGSTEN_HEXAFLUORIDE  # scripted group (container) (typed FeaturePython)
  Dunit = g/cm3
  Dvalue = 2.4
  Group = -> [W_element003,F_element017]
  conduct = 2
  density = 1
  expand = 3
  formula = G4_TUNGSTEN_HEXAFLUORIDE
  name = G4_TUNGSTEN_HEXAFLUORIDE
  specific = 4
FEATURE [App::DocumentObjectGroupPython] U_element001  label="U_element : 1"  # scripted group (container) (typed FeaturePython)
  n = 1
  ref = U_element
FEATURE [App::DocumentObjectGroupPython] C_element117  label="C_element : 064"  # scripted group (container) (typed FeaturePython)
  n = 2
  ref = C_element
FEATURE [App::DocumentObjectGroupPython] G4_URANIUM_DICARBIDE  # scripted group (container) (typed FeaturePython)
  Dunit = g/cm3
  Dvalue = 11.28
  Group = -> [U_element001,C_element117]
  conduct = 2
  density = 1
  expand = 3
  formula = G4_URANIUM_DICARBIDE
  name = G4_URANIUM_DICARBIDE
  specific = 4
FEATURE [App::DocumentObjectGroupPython] U_element002  label="U_element : 002"  # scripted group (container) (typed FeaturePython)
  n = 1
  ref = U_element
FEATURE [App::DocumentObjectGroupPython] C_element118  label="C_element : 065"  # scripted group (container) (typed FeaturePython)
  n = 1
  ref = C_element
FEATURE [App::DocumentObjectGroupPython] G4_URANIUM_MONOCARBIDE  # scripted group (container) (typed FeaturePython)
  Dunit = g/cm3
  Dvalue = 13.63
  Group = -> [U_element002,C_element118]
  conduct = 2
  density = 1
  expand = 3
  formula = G4_URANIUM_MONOCARBIDE
  name = G4_URANIUM_MONOCARBIDE
  specific = 4
FEATURE [App::DocumentObjectGroupPython] U_element003  label="U_element : 003"  # scripted group (container) (typed FeaturePython)
  n = 1
  ref = U_element
FEATURE [App::DocumentObjectGroupPython] O_element100  label="O_element : 054"  # scripted group (container) (typed FeaturePython)
  n = 2
  ref = O_element
FEATURE [App::DocumentObjectGroupPython] G4_URANIUM_OXIDE  # scripted group (container) (typed FeaturePython)
  Dunit = g/cm3
  Dvalue = 10.96
  Group = -> [U_element003,O_element100]
  conduct = 2
  density = 1
  expand = 3
  formula = G4_URANIUM_OXIDE
  name = G4_URANIUM_OXIDE
  specific = 4
FEATURE [App::DocumentObjectGroupPython] C_element119  label="C_element : 066"  # scripted group (container) (typed FeaturePython)
  n = 1
  ref = C_element
FEATURE [App::DocumentObjectGroupPython] H_element107  label="H_element : 057"  # scripted group (container) (typed FeaturePython)
  n = 4
  ref = H_element
FEATURE [App::DocumentObjectGroupPython] N_element046  label="N_element : 019"  # scripted group (container) (typed FeaturePython)
  n = 2
  ref = N_element
FEATURE [App::DocumentObjectGroupPython] O_element101  label="O_element : 055"  # scripted group (container) (typed FeaturePython)
  n = 1
  ref = O_element
FEATURE [App::DocumentObjectGroupPython] G4_UREA  # scripted group (container) (typed FeaturePython)
  Dunit = g/cm3
  Dvalue = 1.323
  Group = -> [C_element119,H_element107,N_element046,O_element101]
  conduct = 2
  density = 1
  expand = 3
  formula = G4_UREA
  name = G4_UREA
  specific = 4
FEATURE [App::DocumentObjectGroupPython] C_element120  label="C_element : 067"  # scripted group (container) (typed FeaturePython)
  n = 5
  ref = C_element
FEATURE [App::DocumentObjectGroupPython] H_element108  label="H_element : 058"  # scripted group (container) (typed FeaturePython)
  n = 11
  ref = H_element
FEATURE [App::DocumentObjectGroupPython] N_element047  label="N_element : 020"  # scripted group (container) (typed FeaturePython)
  n = 1
  ref = N_element
FEATURE [App::DocumentObjectGroupPython] O_element102  label="O_element : 056"  # scripted group (container) (typed FeaturePython)
  n = 2
  ref = O_element
FEATURE [App::DocumentObjectGroupPython] G4_VALINE  # scripted group (container) (typed FeaturePython)
  Dunit = g/cm3
  Dvalue = 1.23
  Group = -> [C_element120,H_element108,N_element047,O_element102]
  conduct = 2
  density = 1
  expand = 3
  formula = G4_VALINE
  name = G4_VALINE
  specific = 4
FEATURE [App::DocumentObjectGroupPython] H_element109  label="H_element : 0.009"  # scripted group (container) (typed FeaturePython)
  n = 0.009417
FEATURE [App::DocumentObjectGroupPython] C_element121  label="C_element : 0.281"  # scripted group (container) (typed FeaturePython)
  n = 0.280555
FEATURE [App::DocumentObjectGroupPython] F_element018  label="F_element : 0.710"  # scripted group (container) (typed FeaturePython)
  n = 0.710028
FEATURE [App::DocumentObjectGroupPython] G4_VITON  # scripted group (container) (typed FeaturePython)
  Dunit = g/cm3
  Dvalue = 1.8
  Group = -> [H_element109,C_element121,F_element018]
  conduct = 2
  density = 1
  expand = 3
  formula = G4_VITON
  name = G4_VITON
  specific = 4
FEATURE [App::DocumentObjectGroupPython] H_element110  label="H_element : 059"  # scripted group (container) (typed FeaturePython)
  n = 2
  ref = H_element
FEATURE [App::DocumentObjectGroupPython] O_element103  label="O_element : 057"  # scripted group (container) (typed FeaturePython)
  n = 1
  ref = O_element
FEATURE [App::DocumentObjectGroupPython] G4_WATER  # scripted group (container) (typed FeaturePython)
  Dunit = g/cm3
  Dvalue = 1
  Group = -> [H_element110,O_element103]
  conduct = 2
  density = 1
  expand = 3
  formula = G4_WATER
  name = G4_WATER
  specific = 4
FEATURE [App::DocumentObjectGroupPython] H_element111  label="H_element : 060"  # scripted group (container) (typed FeaturePython)
  n = 2
  ref = H_element
FEATURE [App::DocumentObjectGroupPython] O_element104  label="O_element : 058"  # scripted group (container) (typed FeaturePython)
  n = 1
  ref = O_element
FEATURE [App::DocumentObjectGroupPython] G4_WATER_VAPOR  # scripted group (container) (typed FeaturePython)
  Dunit = g/cm3
  Dvalue = 0.000756182
  Group = -> [H_element111,O_element104]
  conduct = 2
  density = 1
  expand = 3
  formula = G4_WATER_VAPOR
  name = G4_WATER_VAPOR
  specific = 4
FEATURE [App::DocumentObjectGroupPython] C_element122  label="C_element : 068"  # scripted group (container) (typed FeaturePython)
  n = 8
  ref = C_element
FEATURE [App::DocumentObjectGroupPython] H_element112  label="H_element : 061"  # scripted group (container) (typed FeaturePython)
  n = 10
  ref = H_element
FEATURE [App::DocumentObjectGroupPython] G4_XYLENE  # scripted group (container) (typed FeaturePython)
  Dunit = g/cm3
  Dvalue = 0.87
  Group = -> [C_element122,H_element112]
  conduct = 2
  density = 1
  expand = 3
  formula = G4_XYLENE
  name = G4_XYLENE
  specific = 4
FEATURE [App::DocumentObjectGroupPython] C_element123  label="C_element : 069"  # scripted group (container) (typed FeaturePython)
  n = 1
  ref = C_element
FEATURE [App::DocumentObjectGroupPython] G4_GRAPHITE  # scripted group (container) (typed FeaturePython)
  Dunit = g/cm3
  Dvalue = 2.21
  Group = -> [C_element123]
  conduct = 2
  density = 1
  expand = 3
  formula = G4_GRAPHITE
  name = G4_GRAPHITE
  specific = 4
FEATURE [App::DocumentObjectGroupPython] NIST  # scripted group (container) (typed FeaturePython)
  Group = -> [G4_A_150_TISSUE,G4_ACETONE,G4_ACETYLENE,G4_ADENINE,G4_ADIPOSE_TISSUE_ICRP,G4_AIR,G4_ALANINE,G4_ALUMINUM_OXIDE,G4_AMBER,G4_AMMONIA,G4_ANILINE,G4_ANTHRACENE,G4_B_100_BONE,G4_BAKELITE,G4_BARIUM_FLUORIDE,G4_BARIUM_SULFATE,G4_BENZENE,G4_BERYLLIUM_OXIDE,G4_BGO,G4_BLOOD_ICRP,G4_BONE_COMPACT_ICRU,G4_BONE_CORTICAL_ICRP,G4_BORON_CARBIDE,G4_BORON_OXIDE,G4_BRAIN_ICRP,G4_BUTANE,G4_N_BUTYL_ALCOHOL,G4_C_552,+152 more]
FEATURE [App::DocumentObjectGroupPython] H_element113  label="H_element : 062"  # scripted group (container) (typed FeaturePython)
  n = 1
  ref = H_element
FEATURE [App::DocumentObjectGroupPython] G4_H  # scripted group (container) (typed FeaturePython)
  Dunit = g/cm3
  Dvalue = 8.3748e-05
  Group = -> [H_element113]
  conduct = 2
  density = 1
  expand = 3
  formula = H
  name = G4_H
  specific = 4
FEATURE [App::DocumentObjectGroupPython] He_element001  label="He_element : 1"  # scripted group (container) (typed FeaturePython)
  n = 1
  ref = He_element
FEATURE [App::DocumentObjectGroupPython] G4_He  # scripted group (container) (typed FeaturePython)
  Dunit = g/cm3
  Dvalue = 0.000166322
  Group = -> [He_element001]
  conduct = 2
  density = 1
  expand = 3
  formula = He
  name = G4_He
  specific = 4
FEATURE [App::DocumentObjectGroupPython] Li_element008  label="Li_element : 008"  # scripted group (container) (typed FeaturePython)
  n = 1
  ref = Li_element
FEATURE [App::DocumentObjectGroupPython] G4_Li  # scripted group (container) (typed FeaturePython)
  Dunit = g/cm3
  Dvalue = 0.534
  Group = -> [Li_element008]
  conduct = 2
  density = 1
  expand = 3
  formula = Li
  name = G4_Li
  specific = 4
FEATURE [App::DocumentObjectGroupPython] Be_element002  label="Be_element : 002"  # scripted group (container) (typed FeaturePython)
  n = 1
  ref = Be_element
FEATURE [App::DocumentObjectGroupPython] G4_Be  # scripted group (container) (typed FeaturePython)
  Dunit = g/cm3
  Dvalue = 1.848
  Group = -> [Be_element002]
  conduct = 2
  density = 1
  expand = 3
  formula = Be
  name = G4_Be
  specific = 4
FEATURE [App::DocumentObjectGroupPython] B_element007  label="B_element : 007"  # scripted group (container) (typed FeaturePython)
  n = 1
  ref = B_element
FEATURE [App::DocumentObjectGroupPython] G4_B  # scripted group (container) (typed FeaturePython)
  Dunit = g/cm3
  Dvalue = 2.37
  Group = -> [B_element007]
  conduct = 2
  density = 1
  expand = 3
  formula = B
  name = G4_B
  specific = 4
FEATURE [App::DocumentObjectGroupPython] C_element124  label="C_element : 070"  # scripted group (container) (typed FeaturePython)
  n = 1
  ref = C_element
FEATURE [App::DocumentObjectGroupPython] G4_C  # scripted group (container) (typed FeaturePython)
  Dunit = g/cm3
  Dvalue = 2
  Group = -> [C_element124]
  conduct = 2
  density = 1
  expand = 3
  formula = C
  name = G4_C
  specific = 4
FEATURE [App::DocumentObjectGroupPython] N_element048  label="N_element : 021"  # scripted group (container) (typed FeaturePython)
  n = 1
  ref = N_element
FEATURE [App::DocumentObjectGroupPython] G4_N  # scripted group (container) (typed FeaturePython)
  Dunit = g/cm3
  Dvalue = 0.0011652
  Group = -> [N_element048]
  conduct = 2
  density = 1
  expand = 3
  formula = N
  name = G4_N
  specific = 4
FEATURE [App::DocumentObjectGroupPython] O_element105  label="O_element : 059"  # scripted group (container) (typed FeaturePython)
  n = 1
  ref = O_element
FEATURE [App::DocumentObjectGroupPython] G4_O  # scripted group (container) (typed FeaturePython)
  Dunit = g/cm3
  Dvalue = 0.00133151
  Group = -> [O_element105]
  conduct = 2
  density = 1
  expand = 3
  formula = O
  name = G4_O
  specific = 4
FEATURE [App::DocumentObjectGroupPython] F_element019  label="F_element : 008"  # scripted group (container) (typed FeaturePython)
  n = 1
  ref = F_element
FEATURE [App::DocumentObjectGroupPython] G4_F  # scripted group (container) (typed FeaturePython)
  Dunit = g/cm3
  Dvalue = 0.00158029
  Group = -> [F_element019]
  conduct = 2
  density = 1
  expand = 3
  formula = F
  name = G4_F
  specific = 4
FEATURE [App::DocumentObjectGroupPython] Ne_element001  label="Ne_element : 1"  # scripted group (container) (typed FeaturePython)
  n = 1
  ref = Ne_element
FEATURE [App::DocumentObjectGroupPython] G4_Ne  # scripted group (container) (typed FeaturePython)
  Dunit = g/cm3
  Dvalue = 0.000838505
  Group = -> [Ne_element001]
  conduct = 2
  density = 1
  expand = 3
  formula = Ne
  name = G4_Ne
  specific = 4
FEATURE [App::DocumentObjectGroupPython] Na_element020  label="Na_element : 005"  # scripted group (container) (typed FeaturePython)
  n = 1
  ref = Na_element
FEATURE [App::DocumentObjectGroupPython] G4_Na  # scripted group (container) (typed FeaturePython)
  Dunit = g/cm3
  Dvalue = 0.971
  Group = -> [Na_element020]
  conduct = 2
  density = 1
  expand = 3
  formula = Na
  name = G4_Na
  specific = 4
FEATURE [App::DocumentObjectGroupPython] Mg_element011  label="Mg_element : 005"  # scripted group (container) (typed FeaturePython)
  n = 1
  ref = Mg_element
FEATURE [App::DocumentObjectGroupPython] G4_Mg  # scripted group (container) (typed FeaturePython)
  Dunit = g/cm3
  Dvalue = 1.74
  Group = -> [Mg_element011]
  conduct = 2
  density = 1
  expand = 3
  formula = Mg
  name = G4_Mg
  specific = 4
FEATURE [App::DocumentObjectGroupPython] Al_element004  label="Al_element : 1"  # scripted group (container) (typed FeaturePython)
  n = 1
  ref = Al_element
FEATURE [App::DocumentObjectGroupPython] G4_Al  # scripted group (container) (typed FeaturePython)
  Dunit = g/cm3
  Dvalue = 2.699
  Group = -> [Al_element004]
  conduct = 2
  density = 1
  expand = 3
  formula = Al
  name = G4_Al
  specific = 4
FEATURE [App::DocumentObjectGroupPython] Si_element007  label="Si_element : 002"  # scripted group (container) (typed FeaturePython)
  n = 1
  ref = Si_element
FEATURE [App::DocumentObjectGroupPython] G4_Si  # scripted group (container) (typed FeaturePython)
  Dunit = g/cm3
  Dvalue = 2.33
  Group = -> [Si_element007]
  conduct = 2
  density = 1
  expand = 3
  formula = Si
  name = G4_Si
  specific = 4
FEATURE [App::DocumentObjectGroupPython] P_element013  label="P_element : 002"  # scripted group (container) (typed FeaturePython)
  n = 1
  ref = P_element
FEATURE [App::DocumentObjectGroupPython] G4_P  # scripted group (container) (typed FeaturePython)
  Dunit = g/cm3
  Dvalue = 2.2
  Group = -> [P_element013]
  conduct = 2
  density = 1
  expand = 3
  formula = P
  name = G4_P
  specific = 4
FEATURE [App::DocumentObjectGroupPython] S_element023  label="S_element : 007"  # scripted group (container) (typed FeaturePython)
  n = 1
  ref = S_element
FEATURE [App::DocumentObjectGroupPython] G4_S  # scripted group (container) (typed FeaturePython)
  Dunit = g/cm3
  Dvalue = 2
  Group = -> [S_element023]
  conduct = 2
  density = 1
  expand = 3
  formula = S
  name = G4_S
  specific = 4
FEATURE [App::DocumentObjectGroupPython] Cl_element029  label="Cl_element : 015"  # scripted group (container) (typed FeaturePython)
  n = 1
  ref = Cl_element
FEATURE [App::DocumentObjectGroupPython] G4_Cl  # scripted group (container) (typed FeaturePython)
  Dunit = g/cm3
  Dvalue = 0.00299473
  Group = -> [Cl_element029]
  conduct = 2
  density = 1
  expand = 3
  formula = Cl
  name = G4_Cl
  specific = 4
FEATURE [App::DocumentObjectGroupPython] Ar_element002  label="Ar_element : 1"  # scripted group (container) (typed FeaturePython)
  n = 1
  ref = Ar_element
FEATURE [App::DocumentObjectGroupPython] G4_Ar  # scripted group (container) (typed FeaturePython)
  Dunit = g/cm3
  Dvalue = 0.00166201
  Group = -> [Ar_element002]
  conduct = 2
  density = 1
  expand = 3
  formula = Ar
  name = G4_Ar
  specific = 4
FEATURE [App::DocumentObjectGroupPython] K_element013  label="K_element : 003"  # scripted group (container) (typed FeaturePython)
  n = 1
  ref = K_element
FEATURE [App::DocumentObjectGroupPython] G4_K  # scripted group (container) (typed FeaturePython)
  Dunit = g/cm3
  Dvalue = 0.862
  Group = -> [K_element013]
  conduct = 2
  density = 1
  expand = 3
  formula = K
  name = G4_K
  specific = 4
FEATURE [App::DocumentObjectGroupPython] Ca_element014  label="Ca_element : 007"  # scripted group (container) (typed FeaturePython)
  n = 1
  ref = Ca_element
FEATURE [App::DocumentObjectGroupPython] G4_Ca  # scripted group (container) (typed FeaturePython)
  Dunit = g/cm3
  Dvalue = 1.55
  Group = -> [Ca_element014]
  conduct = 2
  density = 1
  expand = 3
  formula = Ca
  name = G4_Ca
  specific = 4
FEATURE [App::DocumentObjectGroupPython] Sc_element001  label="Sc_element : 1"  # scripted group (container) (typed FeaturePython)
  n = 1
  ref = Sc_element
FEATURE [App::DocumentObjectGroupPython] G4_Sc  # scripted group (container) (typed FeaturePython)
  Dunit = g/cm3
  Dvalue = 2.989
  Group = -> [Sc_element001]
  conduct = 2
  density = 1
  expand = 3
  formula = Sc
  name = G4_Sc
  specific = 4
FEATURE [App::DocumentObjectGroupPython] Ti_element004  label="Ti_element : 002"  # scripted group (container) (typed FeaturePython)
  n = 1
  ref = Ti_element
FEATURE [App::DocumentObjectGroupPython] G4_Ti  # scripted group (container) (typed FeaturePython)
  Dunit = g/cm3
  Dvalue = 4.54
  Group = -> [Ti_element004]
  conduct = 2
  density = 1
  expand = 3
  formula = Ti
  name = G4_Ti
  specific = 4
FEATURE [App::DocumentObjectGroupPython] V_element001  label="V_element : 1"  # scripted group (container) (typed FeaturePython)
  n = 1
  ref = V_element
FEATURE [App::DocumentObjectGroupPython] G4_V  # scripted group (container) (typed FeaturePython)
  Dunit = g/cm3
  Dvalue = 6.11
  Group = -> [V_element001]
  conduct = 2
  density = 1
  expand = 3
  formula = V
  name = G4_V
  specific = 4
FEATURE [App::DocumentObjectGroupPython] Cr_element001  label="Cr_element : 1"  # scripted group (container) (typed FeaturePython)
  n = 1
  ref = Cr_element
FEATURE [App::DocumentObjectGroupPython] G4_Cr  # scripted group (container) (typed FeaturePython)
  Dunit = g/cm3
  Dvalue = 7.18
  Group = -> [Cr_element001]
  conduct = 2
  density = 1
  expand = 3
  formula = Cr
  name = G4_Cr
  specific = 4
FEATURE [App::DocumentObjectGroupPython] Mn_element001  label="Mn_element : 1"  # scripted group (container) (typed FeaturePython)
  n = 1
  ref = Mn_element
FEATURE [App::DocumentObjectGroupPython] G4_Mn  # scripted group (container) (typed FeaturePython)
  Dunit = g/cm3
  Dvalue = 7.44
  Group = -> [Mn_element001]
  conduct = 2
  density = 1
  expand = 3
  formula = Mn
  name = G4_Mn
  specific = 4
FEATURE [App::DocumentObjectGroupPython] Fe_element007  label="Fe_element : 004"  # scripted group (container) (typed FeaturePython)
  n = 1
  ref = Fe_element
FEATURE [App::DocumentObjectGroupPython] G4_Fe  # scripted group (container) (typed FeaturePython)
  Dunit = g/cm3
  Dvalue = 7.874
  Group = -> [Fe_element007]
  conduct = 2
  density = 1
  expand = 3
  formula = Fe
  name = G4_Fe
  specific = 4
FEATURE [App::DocumentObjectGroupPython] Co_element001  label="Co_element : 1"  # scripted group (container) (typed FeaturePython)
  n = 1
  ref = Co_element
FEATURE [App::DocumentObjectGroupPython] G4_Co  # scripted group (container) (typed FeaturePython)
  Dunit = g/cm3
  Dvalue = 8.9
  Group = -> [Co_element001]
  conduct = 2
  density = 1
  expand = 3
  formula = Co
  name = G4_Co
  specific = 4
FEATURE [App::DocumentObjectGroupPython] Ni_element001  label="Ni_element : 1"  # scripted group (container) (typed FeaturePython)
  n = 1
  ref = Ni_element
FEATURE [App::DocumentObjectGroupPython] G4_Ni  # scripted group (container) (typed FeaturePython)
  Dunit = g/cm3
  Dvalue = 8.902
  Group = -> [Ni_element001]
  conduct = 2
  density = 1
  expand = 3
  formula = Ni
  name = G4_Ni
  specific = 4
FEATURE [App::DocumentObjectGroupPython] Cu_element001  label="Cu_element : 1"  # scripted group (container) (typed FeaturePython)
  n = 1
  ref = Cu_element
FEATURE [App::DocumentObjectGroupPython] G4_Cu  # scripted group (container) (typed FeaturePython)
  Dunit = g/cm3
  Dvalue = 8.96
  Group = -> [Cu_element001]
  conduct = 2
  density = 1
  expand = 3
  formula = Cu
  name = G4_Cu
  specific = 4
FEATURE [App::DocumentObjectGroupPython] Zn_element001  label="Zn_element : 1"  # scripted group (container) (typed FeaturePython)
  n = 1
  ref = Zn_element
FEATURE [App::DocumentObjectGroupPython] G4_Zn  # scripted group (container) (typed FeaturePython)
  Dunit = g/cm3
  Dvalue = 7.133
  Group = -> [Zn_element001]
  conduct = 2
  density = 1
  expand = 3
  formula = Zn
  name = G4_Zn
  specific = 4
FEATURE [App::DocumentObjectGroupPython] Ga_element002  label="Ga_element : 002"  # scripted group (container) (typed FeaturePython)
  n = 1
  ref = Ga_element
FEATURE [App::DocumentObjectGroupPython] G4_Ga  # scripted group (container) (typed FeaturePython)
  Dunit = g/cm3
  Dvalue = 5.904
  Group = -> [Ga_element002]
  conduct = 2
  density = 1
  expand = 3
  formula = Ga
  name = G4_Ga
  specific = 4
FEATURE [App::DocumentObjectGroupPython] Ge_element002  label="Ge_element : 1"  # scripted group (container) (typed FeaturePython)
  n = 1
  ref = Ge_element
FEATURE [App::DocumentObjectGroupPython] G4_Ge  # scripted group (container) (typed FeaturePython)
  Dunit = g/cm3
  Dvalue = 5.323
  Group = -> [Ge_element002]
  conduct = 2
  density = 1
  expand = 3
  formula = Ge
  name = G4_Ge
  specific = 4
FEATURE [App::DocumentObjectGroupPython] As_element003  label="As_element : 002"  # scripted group (container) (typed FeaturePython)
  n = 1
  ref = As_element
FEATURE [App::DocumentObjectGroupPython] G4_As  # scripted group (container) (typed FeaturePython)
  Dunit = g/cm3
  Dvalue = 5.73
  Group = -> [As_element003]
  conduct = 2
  density = 1
  expand = 3
  formula = As
  name = G4_As
  specific = 4
FEATURE [App::DocumentObjectGroupPython] Se_element001  label="Se_element : 1"  # scripted group (container) (typed FeaturePython)
  n = 1
  ref = Se_element
FEATURE [App::DocumentObjectGroupPython] G4_Se  # scripted group (container) (typed FeaturePython)
  Dunit = g/cm3
  Dvalue = 4.5
  Group = -> [Se_element001]
  conduct = 2
  density = 1
  expand = 3
  formula = Se
  name = G4_Se
  specific = 4
FEATURE [App::DocumentObjectGroupPython] Br_element007  label="Br_element : 004"  # scripted group (container) (typed FeaturePython)
  n = 1
  ref = Br_element
FEATURE [App::DocumentObjectGroupPython] G4_Br  # scripted group (container) (typed FeaturePython)
  Dunit = g/cm3
  Dvalue = 0.0070721
  Group = -> [Br_element007]
  conduct = 2
  density = 1
  expand = 3
  formula = Br
  name = G4_Br
  specific = 4
FEATURE [App::DocumentObjectGroupPython] Kr_element001  label="Kr_element : 1"  # scripted group (container) (typed FeaturePython)
  n = 1
  ref = Kr_element
FEATURE [App::DocumentObjectGroupPython] G4_Kr  # scripted group (container) (typed FeaturePython)
  Dunit = g/cm3
  Dvalue = 0.00347832
  Group = -> [Kr_element001]
  conduct = 2
  density = 1
  expand = 3
  formula = Kr
  name = G4_Kr
  specific = 4
FEATURE [App::DocumentObjectGroupPython] Rb_element001  label="Rb_element : 1"  # scripted group (container) (typed FeaturePython)
  n = 1
  ref = Rb_element
FEATURE [App::DocumentObjectGroupPython] G4_Rb  # scripted group (container) (typed FeaturePython)
  Dunit = g/cm3
  Dvalue = 1.532
  Group = -> [Rb_element001]
  conduct = 2
  density = 1
  expand = 3
  formula = Rb
  name = G4_Rb
  specific = 4
FEATURE [App::DocumentObjectGroupPython] Sr_element001  label="Sr_element : 1"  # scripted group (container) (typed FeaturePython)
  n = 1
  ref = Sr_element
FEATURE [App::DocumentObjectGroupPython] G4_Sr  # scripted group (container) (typed FeaturePython)
  Dunit = g/cm3
  Dvalue = 2.54
  Group = -> [Sr_element001]
  conduct = 2
  density = 1
  expand = 3
  formula = Sr
  name = G4_Sr
  specific = 4
FEATURE [App::DocumentObjectGroupPython] Y_element001  label="Y_element : 1"  # scripted group (container) (typed FeaturePython)
  n = 1
  ref = Y_element
FEATURE [App::DocumentObjectGroupPython] G4_Y  # scripted group (container) (typed FeaturePython)
  Dunit = g/cm3
  Dvalue = 4.469
  Group = -> [Y_element001]
  conduct = 2
  density = 1
  expand = 3
  formula = Y
  name = G4_Y
  specific = 4
FEATURE [App::DocumentObjectGroupPython] Zr_element001  label="Zr_element : 1"  # scripted group (container) (typed FeaturePython)
  n = 1
  ref = Zr_element
FEATURE [App::DocumentObjectGroupPython] G4_Zr  # scripted group (container) (typed FeaturePython)
  Dunit = g/cm3
  Dvalue = 6.506
  Group = -> [Zr_element001]
  conduct = 2
  density = 1
  expand = 3
  formula = Zr
  name = G4_Zr
  specific = 4
FEATURE [App::DocumentObjectGroupPython] Nb_element001  label="Nb_element : 1"  # scripted group (container) (typed FeaturePython)
  n = 1
  ref = Nb_element
FEATURE [App::DocumentObjectGroupPython] G4_Nb  # scripted group (container) (typed FeaturePython)
  Dunit = g/cm3
  Dvalue = 8.57
  Group = -> [Nb_element001]
  conduct = 2
  density = 1
  expand = 3
  formula = Nb
  name = G4_Nb
  specific = 4
FEATURE [App::DocumentObjectGroupPython] Mo_element001  label="Mo_element : 1"  # scripted group (container) (typed FeaturePython)
  n = 1
  ref = Mo_element
FEATURE [App::DocumentObjectGroupPython] G4_Mo  # scripted group (container) (typed FeaturePython)
  Dunit = g/cm3
  Dvalue = 10.22
  Group = -> [Mo_element001]
  conduct = 2
  density = 1
  expand = 3
  formula = Mo
  name = G4_Mo
  specific = 4
FEATURE [App::DocumentObjectGroupPython] Tc_element001  label="Tc_element : 1"  # scripted group (container) (typed FeaturePython)
  n = 1
  ref = Tc_element
FEATURE [App::DocumentObjectGroupPython] G4_Tc  # scripted group (container) (typed FeaturePython)
  Dunit = g/cm3
  Dvalue = 11.5
  Group = -> [Tc_element001]
  conduct = 2
  density = 1
  expand = 3
  formula = Tc
  name = G4_Tc
  specific = 4
FEATURE [App::DocumentObjectGroupPython] Ru_element001  label="Ru_element : 1"  # scripted group (container) (typed FeaturePython)
  n = 1
  ref = Ru_element
FEATURE [App::DocumentObjectGroupPython] G4_Ru  # scripted group (container) (typed FeaturePython)
  Dunit = g/cm3
  Dvalue = 12.41
  Group = -> [Ru_element001]
  conduct = 2
  density = 1
  expand = 3
  formula = Ru
  name = G4_Ru
  specific = 4
FEATURE [App::DocumentObjectGroupPython] Rh_element001  label="Rh_element : 1"  # scripted group (container) (typed FeaturePython)
  n = 1
  ref = Rh_element
FEATURE [App::DocumentObjectGroupPython] G4_Rh  # scripted group (container) (typed FeaturePython)
  Dunit = g/cm3
  Dvalue = 12.41
  Group = -> [Rh_element001]
  conduct = 2
  density = 1
  expand = 3
  formula = Rh
  name = G4_Rh
  specific = 4
FEATURE [App::DocumentObjectGroupPython] Pd_element001  label="Pd_element : 1"  # scripted group (container) (typed FeaturePython)
  n = 1
  ref = Pd_element
FEATURE [App::DocumentObjectGroupPython] G4_Pd  # scripted group (container) (typed FeaturePython)
  Dunit = g/cm3
  Dvalue = 12.02
  Group = -> [Pd_element001]
  conduct = 2
  density = 1
  expand = 3
  formula = Pd
  name = G4_Pd
  specific = 4
FEATURE [App::DocumentObjectGroupPython] Ag_element006  label="Ag_element : 004"  # scripted group (container) (typed FeaturePython)
  n = 1
  ref = Ag_element
FEATURE [App::DocumentObjectGroupPython] G4_Ag  # scripted group (container) (typed FeaturePython)
  Dunit = g/cm3
  Dvalue = 10.5
  Group = -> [Ag_element006]
  conduct = 2
  density = 1
  expand = 3
  formula = Ag
  name = G4_Ag
  specific = 4
FEATURE [App::DocumentObjectGroupPython] Cd_element003  label="Cd_element : 003"  # scripted group (container) (typed FeaturePython)
  n = 1
  ref = Cd_element
FEATURE [App::DocumentObjectGroupPython] G4_Cd  # scripted group (container) (typed FeaturePython)
  Dunit = g/cm3
  Dvalue = 8.65
  Group = -> [Cd_element003]
  conduct = 2
  density = 1
  expand = 3
  formula = Cd
  name = G4_Cd
  specific = 4
FEATURE [App::DocumentObjectGroupPython] In_element001  label="In_element : 1"  # scripted group (container) (typed FeaturePython)
  n = 1
  ref = In_element
FEATURE [App::DocumentObjectGroupPython] G4_In  # scripted group (container) (typed FeaturePython)
  Dunit = g/cm3
  Dvalue = 7.31
  Group = -> [In_element001]
  conduct = 2
  density = 1
  expand = 3
  formula = In
  name = G4_In
  specific = 4
FEATURE [App::DocumentObjectGroupPython] Sn_element001  label="Sn_element : 1"  # scripted group (container) (typed FeaturePython)
  n = 1
  ref = Sn_element
FEATURE [App::DocumentObjectGroupPython] G4_Sn  # scripted group (container) (typed FeaturePython)
  Dunit = g/cm3
  Dvalue = 7.31
  Group = -> [Sn_element001]
  conduct = 2
  density = 1
  expand = 3
  formula = Sn
  name = G4_Sn
  specific = 4
FEATURE [App::DocumentObjectGroupPython] Sb_element001  label="Sb_element : 1"  # scripted group (container) (typed FeaturePython)
  n = 1
  ref = Sb_element
FEATURE [App::DocumentObjectGroupPython] G4_Sb  # scripted group (container) (typed FeaturePython)
  Dunit = g/cm3
  Dvalue = 6.691
  Group = -> [Sb_element001]
  conduct = 2
  density = 1
  expand = 3
  formula = Sb
  name = G4_Sb
  specific = 4
FEATURE [App::DocumentObjectGroupPython] Te_element002  label="Te_element : 002"  # scripted group (container) (typed FeaturePython)
  n = 1
  ref = Te_element
FEATURE [App::DocumentObjectGroupPython] G4_Te  # scripted group (container) (typed FeaturePython)
  Dunit = g/cm3
  Dvalue = 6.24
  Group = -> [Te_element002]
  conduct = 2
  density = 1
  expand = 3
  formula = Te
  name = G4_Te
  specific = 4
FEATURE [App::DocumentObjectGroupPython] I_element010  label="I_element : 006"  # scripted group (container) (typed FeaturePython)
  n = 1
  ref = I_element
FEATURE [App::DocumentObjectGroupPython] G4_I  # scripted group (container) (typed FeaturePython)
  Dunit = g/cm3
  Dvalue = 4.93
  Group = -> [I_element010]
  conduct = 2
  density = 1
  expand = 3
  formula = I
  name = G4_I
  specific = 4
FEATURE [App::DocumentObjectGroupPython] Xe_element001  label="Xe_element : 1"  # scripted group (container) (typed FeaturePython)
  n = 1
  ref = Xe_element
FEATURE [App::DocumentObjectGroupPython] G4_Xe  # scripted group (container) (typed FeaturePython)
  Dunit = g/cm3
  Dvalue = 0.00548536
  Group = -> [Xe_element001]
  conduct = 2
  density = 1
  expand = 3
  formula = Xe
  name = G4_Xe
  specific = 4
FEATURE [App::DocumentObjectGroupPython] Cs_element003  label="Cs_element : 003"  # scripted group (container) (typed FeaturePython)
  n = 1
  ref = Cs_element
FEATURE [App::DocumentObjectGroupPython] G4_Cs  # scripted group (container) (typed FeaturePython)
  Dunit = g/cm3
  Dvalue = 1.873
  Group = -> [Cs_element003]
  conduct = 2
  density = 1
  expand = 3
  formula = Cs
  name = G4_Cs
  specific = 4
FEATURE [App::DocumentObjectGroupPython] Ba_element003  label="Ba_element : 003"  # scripted group (container) (typed FeaturePython)
  n = 1
  ref = Ba_element
FEATURE [App::DocumentObjectGroupPython] G4_Ba  # scripted group (container) (typed FeaturePython)
  Dunit = g/cm3
  Dvalue = 3.5
  Group = -> [Ba_element003]
  conduct = 2
  density = 1
  expand = 3
  formula = Ba
  name = G4_Ba
  specific = 4
FEATURE [App::DocumentObjectGroupPython] La_element003  label="La_element : 003"  # scripted group (container) (typed FeaturePython)
  n = 1
  ref = La_element
FEATURE [App::DocumentObjectGroupPython] G4_La  # scripted group (container) (typed FeaturePython)
  Dunit = g/cm3
  Dvalue = 6.154
  Group = -> [La_element003]
  conduct = 2
  density = 1
  expand = 3
  formula = La
  name = G4_La
  specific = 4
FEATURE [App::DocumentObjectGroupPython] Ce_element002  label="Ce_element : 1"  # scripted group (container) (typed FeaturePython)
  n = 1
  ref = Ce_element
FEATURE [App::DocumentObjectGroupPython] G4_Ce  # scripted group (container) (typed FeaturePython)
  Dunit = g/cm3
  Dvalue = 6.657
  Group = -> [Ce_element002]
  conduct = 2
  density = 1
  expand = 3
  formula = Ce
  name = G4_Ce
  specific = 4
FEATURE [App::DocumentObjectGroupPython] Pr_element001  label="Pr_element : 1"  # scripted group (container) (typed FeaturePython)
  n = 1
  ref = Pr_element
FEATURE [App::DocumentObjectGroupPython] G4_Pr  # scripted group (container) (typed FeaturePython)
  Dunit = g/cm3
  Dvalue = 6.71
  Group = -> [Pr_element001]
  conduct = 2
  density = 1
  expand = 3
  formula = Pr
  name = G4_Pr
  specific = 4
FEATURE [App::DocumentObjectGroupPython] Nd_element001  label="Nd_element : 1"  # scripted group (container) (typed FeaturePython)
  n = 1
  ref = Nd_element
FEATURE [App::DocumentObjectGroupPython] G4_Nd  # scripted group (container) (typed FeaturePython)
  Dunit = g/cm3
  Dvalue = 6.9
  Group = -> [Nd_element001]
  conduct = 2
  density = 1
  expand = 3
  formula = Nd
  name = G4_Nd
  specific = 4
FEATURE [App::DocumentObjectGroupPython] Pm_element001  label="Pm_element : 1"  # scripted group (container) (typed FeaturePython)
  n = 1
  ref = Pm_element
FEATURE [App::DocumentObjectGroupPython] G4_Pm  # scripted group (container) (typed FeaturePython)
  Dunit = g/cm3
  Dvalue = 7.22
  Group = -> [Pm_element001]
  conduct = 2
  density = 1
  expand = 3
  formula = Pm
  name = G4_Pm
  specific = 4
FEATURE [App::DocumentObjectGroupPython] Sm_element001  label="Sm_element : 1"  # scripted group (container) (typed FeaturePython)
  n = 1
  ref = Sm_element
FEATURE [App::DocumentObjectGroupPython] G4_Sm  # scripted group (container) (typed FeaturePython)
  Dunit = g/cm3
  Dvalue = 7.46
  Group = -> [Sm_element001]
  conduct = 2
  density = 1
  expand = 3
  formula = Sm
  name = G4_Sm
  specific = 4
FEATURE [App::DocumentObjectGroupPython] Eu_element001  label="Eu_element : 1"  # scripted group (container) (typed FeaturePython)
  n = 1
  ref = Eu_element
FEATURE [App::DocumentObjectGroupPython] G4_Eu  # scripted group (container) (typed FeaturePython)
  Dunit = g/cm3
  Dvalue = 5.243
  Group = -> [Eu_element001]
  conduct = 2
  density = 1
  expand = 3
  formula = Eu
  name = G4_Eu
  specific = 4
FEATURE [App::DocumentObjectGroupPython] Gd_element002  label="Gd_element : 1"  # scripted group (container) (typed FeaturePython)
  n = 1
  ref = Gd_element
FEATURE [App::DocumentObjectGroupPython] G4_Gd  # scripted group (container) (typed FeaturePython)
  Dunit = g/cm3
  Dvalue = 7.9004
  Group = -> [Gd_element002]
  conduct = 2
  density = 1
  expand = 3
  formula = Gd
  name = G4_Gd
  specific = 4
FEATURE [App::DocumentObjectGroupPython] Tb_element001  label="Tb_element : 1"  # scripted group (container) (typed FeaturePython)
  n = 1
  ref = Tb_element
FEATURE [App::DocumentObjectGroupPython] G4_Tb  # scripted group (container) (typed FeaturePython)
  Dunit = g/cm3
  Dvalue = 8.229
  Group = -> [Tb_element001]
  conduct = 2
  density = 1
  expand = 3
  formula = Tb
  name = G4_Tb
  specific = 4
FEATURE [App::DocumentObjectGroupPython] Dy_element001  label="Dy_element : 1"  # scripted group (container) (typed FeaturePython)
  n = 1
  ref = Dy_element
FEATURE [App::DocumentObjectGroupPython] G4_Dy  # scripted group (container) (typed FeaturePython)
  Dunit = g/cm3
  Dvalue = 8.55
  Group = -> [Dy_element001]
  conduct = 2
  density = 1
  expand = 3
  formula = Dy
  name = G4_Dy
  specific = 4
FEATURE [App::DocumentObjectGroupPython] Ho_element001  label="Ho_element : 1"  # scripted group (container) (typed FeaturePython)
  n = 1
  ref = Ho_element
FEATURE [App::DocumentObjectGroupPython] G4_Ho  # scripted group (container) (typed FeaturePython)
  Dunit = g/cm3
  Dvalue = 8.795
  Group = -> [Ho_element001]
  conduct = 2
  density = 1
  expand = 3
  formula = Ho
  name = G4_Ho
  specific = 4
FEATURE [App::DocumentObjectGroupPython] Er_element001  label="Er_element : 1"  # scripted group (container) (typed FeaturePython)
  n = 1
  ref = Er_element
FEATURE [App::DocumentObjectGroupPython] G4_Er  # scripted group (container) (typed FeaturePython)
  Dunit = g/cm3
  Dvalue = 9.066
  Group = -> [Er_element001]
  conduct = 2
  density = 1
  expand = 3
  formula = Er
  name = G4_Er
  specific = 4
FEATURE [App::DocumentObjectGroupPython] Tm_element001  label="Tm_element : 1"  # scripted group (container) (typed FeaturePython)
  n = 1
  ref = Tm_element
FEATURE [App::DocumentObjectGroupPython] G4_Tm  # scripted group (container) (typed FeaturePython)
  Dunit = g/cm3
  Dvalue = 9.321
  Group = -> [Tm_element001]
  conduct = 2
  density = 1
  expand = 3
  formula = Tm
  name = G4_Tm
  specific = 4
FEATURE [App::DocumentObjectGroupPython] Yb_element001  label="Yb_element : 1"  # scripted group (container) (typed FeaturePython)
  n = 1
  ref = Yb_element
FEATURE [App::DocumentObjectGroupPython] G4_Yb  # scripted group (container) (typed FeaturePython)
  Dunit = g/cm3
  Dvalue = 6.73
  Group = -> [Yb_element001]
  conduct = 2
  density = 1
  expand = 3
  formula = Yb
  name = G4_Yb
  specific = 4
FEATURE [App::DocumentObjectGroupPython] Lu_element001  label="Lu_element : 1"  # scripted group (container) (typed FeaturePython)
  n = 1
  ref = Lu_element
FEATURE [App::DocumentObjectGroupPython] G4_Lu  # scripted group (container) (typed FeaturePython)
  Dunit = g/cm3
  Dvalue = 9.84
  Group = -> [Lu_element001]
  conduct = 2
  density = 1
  expand = 3
  formula = Lu
  name = G4_Lu
  specific = 4
FEATURE [App::DocumentObjectGroupPython] Hf_element001  label="Hf_element : 1"  # scripted group (container) (typed FeaturePython)
  n = 1
  ref = Hf_element
FEATURE [App::DocumentObjectGroupPython] G4_Hf  # scripted group (container) (typed FeaturePython)
  Dunit = g/cm3
  Dvalue = 13.31
  Group = -> [Hf_element001]
  conduct = 2
  density = 1
  expand = 3
  formula = Hf
  name = G4_Hf
  specific = 4
FEATURE [App::DocumentObjectGroupPython] Ta_element001  label="Ta_element : 1"  # scripted group (container) (typed FeaturePython)
  n = 1
  ref = Ta_element
FEATURE [App::DocumentObjectGroupPython] G4_Ta  # scripted group (container) (typed FeaturePython)
  Dunit = g/cm3
  Dvalue = 16.654
  Group = -> [Ta_element001]
  conduct = 2
  density = 1
  expand = 3
  formula = Ta
  name = G4_Ta
  specific = 4
FEATURE [App::DocumentObjectGroupPython] W_element004  label="W_element : 004"  # scripted group (container) (typed FeaturePython)
  n = 1
  ref = W_element
FEATURE [App::DocumentObjectGroupPython] G4_W  # scripted group (container) (typed FeaturePython)
  Dunit = g/cm3
  Dvalue = 19.3
  Group = -> [W_element004]
  conduct = 2
  density = 1
  expand = 3
  formula = W
  name = G4_W
  specific = 4
FEATURE [App::DocumentObjectGroupPython] Re_element001  label="Re_element : 1"  # scripted group (container) (typed FeaturePython)
  n = 1
  ref = Re_element
FEATURE [App::DocumentObjectGroupPython] G4_Re  # scripted group (container) (typed FeaturePython)
  Dunit = g/cm3
  Dvalue = 21.02
  Group = -> [Re_element001]
  conduct = 2
  density = 1
  expand = 3
  formula = Re
  name = G4_Re
  specific = 4
FEATURE [App::DocumentObjectGroupPython] Os_element001  label="Os_element : 1"  # scripted group (container) (typed FeaturePython)
  n = 1
  ref = Os_element
FEATURE [App::DocumentObjectGroupPython] G4_Os  # scripted group (container) (typed FeaturePython)
  Dunit = g/cm3
  Dvalue = 22.57
  Group = -> [Os_element001]
  conduct = 2
  density = 1
  expand = 3
  formula = Os
  name = G4_Os
  specific = 4
FEATURE [App::DocumentObjectGroupPython] Ir_element001  label="Ir_element : 1"  # scripted group (container) (typed FeaturePython)
  n = 1
  ref = Ir_element
FEATURE [App::DocumentObjectGroupPython] G4_Ir  # scripted group (container) (typed FeaturePython)
  Dunit = g/cm3
  Dvalue = 22.42
  Group = -> [Ir_element001]
  conduct = 2
  density = 1
  expand = 3
  formula = Ir
  name = G4_Ir
  specific = 4
FEATURE [App::DocumentObjectGroupPython] Pt_element001  label="Pt_element : 1"  # scripted group (container) (typed FeaturePython)
  n = 1
  ref = Pt_element
FEATURE [App::DocumentObjectGroupPython] G4_Pt  # scripted group (container) (typed FeaturePython)
  Dunit = g/cm3
  Dvalue = 21.45
  Group = -> [Pt_element001]
  conduct = 2
  density = 1
  expand = 3
  formula = Pt
  name = G4_Pt
  specific = 4
FEATURE [App::DocumentObjectGroupPython] Au_element001  label="Au_element : 1"  # scripted group (container) (typed FeaturePython)
  n = 1
  ref = Au_element
FEATURE [App::DocumentObjectGroupPython] G4_Au  # scripted group (container) (typed FeaturePython)
  Dunit = g/cm3
  Dvalue = 19.32
  Group = -> [Au_element001]
  conduct = 2
  density = 1
  expand = 3
  formula = Au
  name = G4_Au
  specific = 4
FEATURE [App::DocumentObjectGroupPython] Hg_element002  label="Hg_element : 002"  # scripted group (container) (typed FeaturePython)
  n = 1
  ref = Hg_element
FEATURE [App::DocumentObjectGroupPython] G4_Hg  # scripted group (container) (typed FeaturePython)
  Dunit = g/cm3
  Dvalue = 13.546
  Group = -> [Hg_element002]
  conduct = 2
  density = 1
  expand = 3
  formula = Hg
  name = G4_Hg
  specific = 4
FEATURE [App::DocumentObjectGroupPython] Tl_element002  label="Tl_element : 002"  # scripted group (container) (typed FeaturePython)
  n = 1
  ref = Tl_element
FEATURE [App::DocumentObjectGroupPython] G4_Tl  # scripted group (container) (typed FeaturePython)
  Dunit = g/cm3
  Dvalue = 11.72
  Group = -> [Tl_element002]
  conduct = 2
  density = 1
  expand = 3
  formula = Tl
  name = G4_Tl
  specific = 4
FEATURE [App::DocumentObjectGroupPython] Pb_element003  label="Pb_element : 1"  # scripted group (container) (typed FeaturePython)
  n = 1
  ref = Pb_element
FEATURE [App::DocumentObjectGroupPython] G4_Pb  # scripted group (container) (typed FeaturePython)
  Dunit = g/cm3
  Dvalue = 11.35
  Group = -> [Pb_element003]
  conduct = 2
  density = 1
  expand = 3
  formula = Pb
  name = G4_Pb
  specific = 4
FEATURE [App::DocumentObjectGroupPython] Bi_element002  label="Bi_element : 1"  # scripted group (container) (typed FeaturePython)
  n = 1
  ref = Bi_element
FEATURE [App::DocumentObjectGroupPython] G4_Bi  # scripted group (container) (typed FeaturePython)
  Dunit = g/cm3
  Dvalue = 9.747
  Group = -> [Bi_element002]
  conduct = 2
  density = 1
  expand = 3
  formula = Bi
  name = G4_Bi
  specific = 4
FEATURE [App::DocumentObjectGroupPython] Po_element001  label="Po_element : 1"  # scripted group (container) (typed FeaturePython)
  n = 1
  ref = Po_element
FEATURE [App::DocumentObjectGroupPython] G4_Po  # scripted group (container) (typed FeaturePython)
  Dunit = g/cm3
  Dvalue = 9.32
  Group = -> [Po_element001]
  conduct = 2
  density = 1
  expand = 3
  formula = Po
  name = G4_Po
  specific = 4
FEATURE [App::DocumentObjectGroupPython] At_element001  label="At_element : 1"  # scripted group (container) (typed FeaturePython)
  n = 1
  ref = At_element
FEATURE [App::DocumentObjectGroupPython] G4_At  # scripted group (container) (typed FeaturePython)
  Dunit = g/cm3
  Dvalue = 9.32
  Group = -> [At_element001]
  conduct = 2
  density = 1
  expand = 3
  formula = At
  name = G4_At
  specific = 4
FEATURE [App::DocumentObjectGroupPython] Rn_element001  label="Rn_element : 1"  # scripted group (container) (typed FeaturePython)
  n = 1
  ref = Rn_element
FEATURE [App::DocumentObjectGroupPython] G4_Rn  # scripted group (container) (typed FeaturePython)
  Dunit = g/cm3
  Dvalue = 0.00900662
  Group = -> [Rn_element001]
  conduct = 2
  density = 1
  expand = 3
  formula = Rn
  name = G4_Rn
  specific = 4
FEATURE [App::DocumentObjectGroupPython] Fr_element001  label="Fr_element : 1"  # scripted group (container) (typed FeaturePython)
  n = 1
  ref = Fr_element
FEATURE [App::DocumentObjectGroupPython] G4_Fr  # scripted group (container) (typed FeaturePython)
  Dunit = g/cm3
  Dvalue = 1
  Group = -> [Fr_element001]
  conduct = 2
  density = 1
  expand = 3
  formula = Fr
  name = G4_Fr
  specific = 4
FEATURE [App::DocumentObjectGroupPython] Ra_element001  label="Ra_element : 1"  # scripted group (container) (typed FeaturePython)
  n = 1
  ref = Ra_element
FEATURE [App::DocumentObjectGroupPython] G4_Ra  # scripted group (container) (typed FeaturePython)
  Dunit = g/cm3
  Dvalue = 5
  Group = -> [Ra_element001]
  conduct = 2
  density = 1
  expand = 3
  formula = Ra
  name = G4_Ra
  specific = 4
FEATURE [App::DocumentObjectGroupPython] Ac_element001  label="Ac_element : 1"  # scripted group (container) (typed FeaturePython)
  n = 1
  ref = Ac_element
FEATURE [App::DocumentObjectGroupPython] G4_Ac  # scripted group (container) (typed FeaturePython)
  Dunit = g/cm3
  Dvalue = 10.07
  Group = -> [Ac_element001]
  conduct = 2
  density = 1
  expand = 3
  formula = Ac
  name = G4_Ac
  specific = 4
FEATURE [App::DocumentObjectGroupPython] Th_element001  label="Th_element : 1"  # scripted group (container) (typed FeaturePython)
  n = 1
  ref = Th_element
FEATURE [App::DocumentObjectGroupPython] G4_Th  # scripted group (container) (typed FeaturePython)
  Dunit = g/cm3
  Dvalue = 11.72
  Group = -> [Th_element001]
  conduct = 2
  density = 1
  expand = 3
  formula = Th
  name = G4_Th
  specific = 4
FEATURE [App::DocumentObjectGroupPython] Pa_element001  label="Pa_element : 1"  # scripted group (container) (typed FeaturePython)
  n = 1
  ref = Pa_element
FEATURE [App::DocumentObjectGroupPython] G4_Pa  # scripted group (container) (typed FeaturePython)
  Dunit = g/cm3
  Dvalue = 15.37
  Group = -> [Pa_element001]
  conduct = 2
  density = 1
  expand = 3
  formula = Pa
  name = G4_Pa
  specific = 4
FEATURE [App::DocumentObjectGroupPython] U_element004  label="U_element : 004"  # scripted group (container) (typed FeaturePython)
  n = 1
  ref = U_element
FEATURE [App::DocumentObjectGroupPython] G4_U  # scripted group (container) (typed FeaturePython)
  Dunit = g/cm3
  Dvalue = 18.95
  Group = -> [U_element004]
  conduct = 2
  density = 1
  expand = 3
  formula = U
  name = G4_U
  specific = 4
FEATURE [App::DocumentObjectGroupPython] Np_element001  label="Np_element : 1"  # scripted group (container) (typed FeaturePython)
  n = 1
  ref = Np_element
FEATURE [App::DocumentObjectGroupPython] G4_Np  # scripted group (container) (typed FeaturePython)
  Dunit = g/cm3
  Dvalue = 20.25
  Group = -> [Np_element001]
  conduct = 2
  density = 1
  expand = 3
  formula = Np
  name = G4_Np
  specific = 4
FEATURE [App::DocumentObjectGroupPython] Pu_element002  label="Pu_element : 002"  # scripted group (container) (typed FeaturePython)
  n = 1
  ref = Pu_element
FEATURE [App::DocumentObjectGroupPython] G4_Pu  # scripted group (container) (typed FeaturePython)
  Dunit = g/cm3
  Dvalue = 19.84
  Group = -> [Pu_element002]
  conduct = 2
  density = 1
  expand = 3
  formula = Pu
  name = G4_Pu
  specific = 4
FEATURE [App::DocumentObjectGroupPython] Am_element001  label="Am_element : 1"  # scripted group (container) (typed FeaturePython)
  n = 1
  ref = Am_element
FEATURE [App::DocumentObjectGroupPython] G4_Am  # scripted group (container) (typed FeaturePython)
  Dunit = g/cm3
  Dvalue = 13.67
  Group = -> [Am_element001]
  conduct = 2
  density = 1
  expand = 3
  formula = Am
  name = G4_Am
  specific = 4
FEATURE [App::DocumentObjectGroupPython] Cm_element001  label="Cm_element : 1"  # scripted group (container) (typed FeaturePython)
  n = 1
  ref = Cm_element
FEATURE [App::DocumentObjectGroupPython] G4_Cm  # scripted group (container) (typed FeaturePython)
  Dunit = g/cm3
  Dvalue = 13.51
  Group = -> [Cm_element001]
  conduct = 2
  density = 1
  expand = 3
  formula = Cm
  name = G4_Cm
  specific = 4
FEATURE [App::DocumentObjectGroupPython] Bk_element001  label="Bk_element : 1"  # scripted group (container) (typed FeaturePython)
  n = 1
  ref = Bk_element
FEATURE [App::DocumentObjectGroupPython] G4_Bk  # scripted group (container) (typed FeaturePython)
  Dunit = g/cm3
  Dvalue = 14
  Group = -> [Bk_element001]
  conduct = 2
  density = 1
  expand = 3
  formula = Bk
  name = G4_Bk
  specific = 4
FEATURE [App::DocumentObjectGroupPython] Cf_element001  label="Cf_element : 1"  # scripted group (container) (typed FeaturePython)
  n = 1
  ref = Cf_element
FEATURE [App::DocumentObjectGroupPython] G4_Cf  # scripted group (container) (typed FeaturePython)
  Dunit = g/cm3
  Dvalue = 10
  Group = -> [Cf_element001]
  conduct = 2
  density = 1
  expand = 3
  formula = Cf
  name = G4_Cf
  specific = 4
FEATURE [App::DocumentObjectGroupPython] Element  # scripted group (container) (typed FeaturePython)
  Group = -> [G4_H,G4_He,G4_Li,G4_Be,G4_B,G4_C,G4_N,G4_O,G4_F,G4_Ne,G4_Na,G4_Mg,G4_Al,G4_Si,G4_P,G4_S,G4_Cl,G4_Ar,G4_K,G4_Ca,G4_Sc,G4_Ti,G4_V,G4_Cr,G4_Mn,G4_Fe,G4_Co,G4_Ni,G4_Cu,G4_Zn,G4_Ga,G4_Ge,G4_As,G4_Se,G4_Br,G4_Kr,G4_Rb,G4_Sr,G4_Y,G4_Zr,G4_Nb,G4_Mo,G4_Tc,G4_Ru,G4_Rh,G4_Pd,G4_Ag,G4_Cd,G4_In,G4_Sn,G4_Sb,G4_Te,G4_I,G4_Xe,G4_Cs,G4_Ba,G4_La,G4_Ce,G4_Pr,G4_Nd,G4_Pm,G4_Sm,G4_Eu,G4_Gd,G4_Tb,G4_Dy,G4_Ho,G4_Er,+30 more]
FEATURE [App::DocumentObjectGroupPython] H_element114  label="H_element : 063"  # scripted group (container) (typed FeaturePython)
  n = 2
  ref = H_element
FEATURE [App::DocumentObjectGroupPython] G4_lH2  # scripted group (container) (typed FeaturePython)
  Dunit = g/cm3
  Dvalue = 0.0708
  Group = -> [H_element114]
  conduct = 2
  density = 1
  expand = 3
  formula = G4_lH2
  name = G4_lH2
  specific = 4
FEATURE [App::DocumentObjectGroupPython] N_element049  label="N_element : 022"  # scripted group (container) (typed FeaturePython)
  n = 2
  ref = N_element
FEATURE [App::DocumentObjectGroupPython] G4_lN2  # scripted group (container) (typed FeaturePython)
  Dunit = g/cm3
  Dvalue = 0.807
  Group = -> [N_element049]
  conduct = 2
  density = 1
  expand = 3
  formula = G4_lN2
  name = G4_lN2
  specific = 4
FEATURE [App::DocumentObjectGroupPython] O_element106  label="O_element : 060"  # scripted group (container) (typed FeaturePython)
  n = 2
  ref = O_element
FEATURE [App::DocumentObjectGroupPython] G4_lO2  # scripted group (container) (typed FeaturePython)
  Dunit = g/cm3
  Dvalue = 1.141
  Group = -> [O_element106]
  conduct = 2
  density = 1
  expand = 3
  formula = G4_lO2
  name = G4_lO2
  specific = 4
FEATURE [App::DocumentObjectGroupPython] Ar  label="Ar : 1"  # scripted group (container) (typed FeaturePython)
  n = 1
  ref = Ar
FEATURE [App::DocumentObjectGroupPython] G4_lAr  # scripted group (container) (typed FeaturePython)
  Dunit = g/cm3
  Dvalue = 1.396
  Group = -> [Ar]
  conduct = 2
  density = 1
  expand = 3
  formula = G4_lAr
  name = G4_lAr
  specific = 4
FEATURE [App::DocumentObjectGroupPython] Br  label="Br : 1"  # scripted group (container) (typed FeaturePython)
  n = 1
  ref = Br
FEATURE [App::DocumentObjectGroupPython] G4_lBr  # scripted group (container) (typed FeaturePython)
  Dunit = g/cm3
  Dvalue = 3.1028
  Group = -> [Br]
  conduct = 2
  density = 1
  expand = 3
  formula = G4_lBr
  name = G4_lBr
  specific = 4
FEATURE [App::DocumentObjectGroupPython] Kr  label="Kr : 1"  # scripted group (container) (typed FeaturePython)
  n = 1
  ref = Kr
FEATURE [App::DocumentObjectGroupPython] G4_lKr  # scripted group (container) (typed FeaturePython)
  Dunit = g/cm3
  Dvalue = 2.418
  Group = -> [Kr]
  conduct = 2
  density = 1
  expand = 3
  formula = G4_lKr
  name = G4_lKr
  specific = 4
FEATURE [App::DocumentObjectGroupPython] Xe  label="Xe : 1"  # scripted group (container) (typed FeaturePython)
  n = 1
  ref = Xe
FEATURE [App::DocumentObjectGroupPython] G4_lXe  # scripted group (container) (typed FeaturePython)
  Dunit = g/cm3
  Dvalue = 2.953
  Group = -> [Xe]
  conduct = 2
  density = 1
  expand = 3
  formula = G4_lXe
  name = G4_lXe
  specific = 4
FEATURE [App::DocumentObjectGroupPython] O_element107  label="O_element : 061"  # scripted group (container) (typed FeaturePython)
  n = 4
  ref = O_element
FEATURE [App::DocumentObjectGroupPython] Pb_element004  label="Pb_element : 002"  # scripted group (container) (typed FeaturePython)
  n = 1
  ref = Pb_element
FEATURE [App::DocumentObjectGroupPython] W_element005  label="W_element : 005"  # scripted group (container) (typed FeaturePython)
  n = 1
  ref = W_element
FEATURE [App::DocumentObjectGroupPython] G4_PbWO4  # scripted group (container) (typed FeaturePython)
  Dunit = g/cm3
  Dvalue = 8.28
  Group = -> [O_element107,Pb_element004,W_element005]
  conduct = 2
  density = 1
  expand = 3
  formula = G4_PbWO4
  name = G4_PbWO4
  specific = 4
FEATURE [App::DocumentObjectGroupPython] alactic  label="alactic : 1"  # scripted group (container) (typed FeaturePython)
  n = 1
  ref = alactic
FEATURE [App::DocumentObjectGroupPython] G4_Galactic  # scripted group (container) (typed FeaturePython)
  Dunit = g/cm3
  Dvalue = 0
  Group = -> [alactic]
  conduct = 2
  density = 1
  expand = 3
  formula = G4_Galactic
  name = G4_Galactic
  specific = 4
FEATURE [App::DocumentObjectGroupPython] RAPHITE_POROUS  label="RAPHITE_POROUS : 1"  # scripted group (container) (typed FeaturePython)
  n = 1
  ref = RAPHITE_POROUS
FEATURE [App::DocumentObjectGroupPython] G4_GRAPHITE_POROUS  # scripted group (container) (typed FeaturePython)
  Dunit = g/cm3
  Dvalue = 1.7
  Group = -> [RAPHITE_POROUS]
  conduct = 2
  density = 1
  expand = 3
  formula = G4_GRAPHITE_POROUS
  name = G4_GRAPHITE_POROUS
  specific = 4
FEATURE [App::DocumentObjectGroupPython] H_element115  label="H_element : 0.150"  # scripted group (container) (typed FeaturePython)
  n = 0.080538
FEATURE [App::DocumentObjectGroupPython] C_element125  label="C_element : 0.600"  # scripted group (container) (typed FeaturePython)
  n = 0.599848
FEATURE [App::DocumentObjectGroupPython] O_element108  label="O_element : 0.320"  # scripted group (container) (typed FeaturePython)
  n = 0.319614
FEATURE [App::DocumentObjectGroupPython] G4_LUCITE  # scripted group (container) (typed FeaturePython)
  Dunit = g/cm3
  Dvalue = 1.19
  Group = -> [H_element115,C_element125,O_element108]
  conduct = 2
  density = 1
  expand = 3
  formula = G4_LUCITE
  name = G4_LUCITE
  specific = 4
FEATURE [App::DocumentObjectGroupPython] Cu_element002  label="Cu_element : 62"  # scripted group (container) (typed FeaturePython)
  n = 62
  ref = Cu_element
FEATURE [App::DocumentObjectGroupPython] Zn_element002  label="Zn_element : 35"  # scripted group (container) (typed FeaturePython)
  n = 35
  ref = Zn_element
FEATURE [App::DocumentObjectGroupPython] Pb_element005  label="Pb_element : 3"  # scripted group (container) (typed FeaturePython)
  n = 3
  ref = Pb_element
FEATURE [App::DocumentObjectGroupPython] G4_BRASS  # scripted group (container) (typed FeaturePython)
  Dunit = g/cm3
  Dvalue = 8.52
  Group = -> [Cu_element002,Zn_element002,Pb_element005]
  conduct = 2
  density = 1
  expand = 3
  formula = G4_BRASS
  name = G4_BRASS
  specific = 4
FEATURE [App::DocumentObjectGroupPython] Cu_element003  label="Cu_element : 89"  # scripted group (container) (typed FeaturePython)
  n = 89
  ref = Cu_element
FEATURE [App::DocumentObjectGroupPython] Zn_element003  label="Zn_element : 9"  # scripted group (container) (typed FeaturePython)
  n = 9
  ref = Zn_element
FEATURE [App::DocumentObjectGroupPython] Pb_element006  label="Pb_element : 2"  # scripted group (container) (typed FeaturePython)
  n = 2
  ref = Pb_element
FEATURE [App::DocumentObjectGroupPython] G4_BRONZE  # scripted group (container) (typed FeaturePython)
  Dunit = g/cm3
  Dvalue = 8.82
  Group = -> [Cu_element003,Zn_element003,Pb_element006]
  conduct = 2
  density = 1
  expand = 3
  formula = G4_BRONZE
  name = G4_BRONZE
  specific = 4
FEATURE [App::DocumentObjectGroupPython] Fe_element008  label="Fe_element : 74"  # scripted group (container) (typed FeaturePython)
  n = 74
  ref = Fe_element
FEATURE [App::DocumentObjectGroupPython] Cr_element002  label="Cr_element : 18"  # scripted group (container) (typed FeaturePython)
  n = 18
  ref = Cr_element
FEATURE [App::DocumentObjectGroupPython] Ni_element002  label="Ni_element : 8"  # scripted group (container) (typed FeaturePython)
  n = 8
  ref = Ni_element
FEATURE [App::DocumentObjectGroupPython] G4_STAINLESS_STEEL  label="G4_STAINLESS-STEEL"  # scripted group (container) (typed FeaturePython)
  Dunit = g/cm3
  Dvalue = 8
  Group = -> [Fe_element008,Cr_element002,Ni_element002]
  conduct = 2
  density = 1
  expand = 3
  formula = G4_STAINLESS-STEEL
  name = G4_STAINLESS-STEEL
  specific = 4
FEATURE [App::DocumentObjectGroupPython] H_element116  label="H_element : 064"  # scripted group (container) (typed FeaturePython)
  n = 18
  ref = H_element
FEATURE [App::DocumentObjectGroupPython] C_element126  label="C_element : 071"  # scripted group (container) (typed FeaturePython)
  n = 12
  ref = C_element
FEATURE [App::DocumentObjectGroupPython] O_element109  label="O_element : 062"  # scripted group (container) (typed FeaturePython)
  n = 7
  ref = O_element
FEATURE [App::DocumentObjectGroupPython] G4_CR39  # scripted group (container) (typed FeaturePython)
  Dunit = g/cm3
  Dvalue = 1.32
  Group = -> [H_element116,C_element126,O_element109]
  conduct = 2
  density = 1
  expand = 3
  formula = G4_CR39
  name = G4_CR39
  specific = 4
FEATURE [App::DocumentObjectGroupPython] H_element117  label="H_element : 38"  # scripted group (container) (typed FeaturePython)
  n = 38
  ref = H_element
FEATURE [App::DocumentObjectGroupPython] C_element127  label="C_element : 072"  # scripted group (container) (typed FeaturePython)
  n = 18
  ref = C_element
FEATURE [App::DocumentObjectGroupPython] O_element110  label="O_element : 063"  # scripted group (container) (typed FeaturePython)
  n = 1
  ref = O_element
FEATURE [App::DocumentObjectGroupPython] G4_OCTADECANOL  # scripted group (container) (typed FeaturePython)
  Dunit = g/cm3
  Dvalue = 0.812
  Group = -> [H_element117,C_element127,O_element110]
  conduct = 2
  density = 1
  expand = 3
  formula = G4_OCTADECANOL
  name = G4_OCTADECANOL
  specific = 4
FEATURE [App::DocumentObjectGroupPython] HEP  # scripted group (container) (typed FeaturePython)
  Group = -> [G4_lH2,G4_lN2,G4_lO2,G4_lAr,G4_lBr,G4_lKr,G4_lXe,G4_PbWO4,G4_Galactic,G4_GRAPHITE_POROUS,G4_LUCITE,G4_BRASS,G4_BRONZE,G4_STAINLESS_STEEL,G4_CR39,G4_OCTADECANOL]
FEATURE [App::DocumentObjectGroupPython] C_element128  label="C_element : 073"  # scripted group (container) (typed FeaturePython)
  n = 14
  ref = C_element
FEATURE [App::DocumentObjectGroupPython] H_element118  label="H_element : 065"  # scripted group (container) (typed FeaturePython)
  n = 10
  ref = H_element
FEATURE [App::DocumentObjectGroupPython] O_element111  label="O_element : 064"  # scripted group (container) (typed FeaturePython)
  n = 2
  ref = O_element
FEATURE [App::DocumentObjectGroupPython] N_element050  label="N_element : 023"  # scripted group (container) (typed FeaturePython)
  n = 2
  ref = N_element
FEATURE [App::DocumentObjectGroupPython] G4_KEVLAR  # scripted group (container) (typed FeaturePython)
  Dunit = g/cm3
  Dvalue = 1.44
  Group = -> [C_element128,H_element118,O_element111,N_element050]
  conduct = 2
  density = 1
  expand = 3
  formula = G4_KEVLAR
  name = G4_KEVLAR
  specific = 4
FEATURE [App::DocumentObjectGroupPython] C_element129  label="C_element : 074"  # scripted group (container) (typed FeaturePython)
  n = 10
  ref = C_element
FEATURE [App::DocumentObjectGroupPython] H_element119  label="H_element : 066"  # scripted group (container) (typed FeaturePython)
  n = 8
  ref = H_element
FEATURE [App::DocumentObjectGroupPython] O_element112  label="O_element : 065"  # scripted group (container) (typed FeaturePython)
  n = 4
  ref = O_element
FEATURE [App::DocumentObjectGroupPython] G4_DACRON  # scripted group (container) (typed FeaturePython)
  Dunit = g/cm3
  Dvalue = 1.4
  Group = -> [C_element129,H_element119,O_element112]
  conduct = 2
  density = 1
  expand = 3
  formula = G4_DACRON
  name = G4_DACRON
  specific = 4
FEATURE [App::DocumentObjectGroupPython] C_element130  label="C_element : 075"  # scripted group (container) (typed FeaturePython)
  n = 4
  ref = C_element
FEATURE [App::DocumentObjectGroupPython] H_element120  label="H_element : 067"  # scripted group (container) (typed FeaturePython)
  n = 5
  ref = H_element
FEATURE [App::DocumentObjectGroupPython] Cl_element030  label="Cl_element : 016"  # scripted group (container) (typed FeaturePython)
  n = 1
  ref = Cl_element
FEATURE [App::DocumentObjectGroupPython] G4_NEOPRENE  # scripted group (container) (typed FeaturePython)
  Dunit = g/cm3
  Dvalue = 1.23
  Group = -> [C_element130,H_element120,Cl_element030]
  conduct = 2
  density = 1
  expand = 3
  formula = G4_NEOPRENE
  name = G4_NEOPRENE
  specific = 4
FEATURE [App::DocumentObjectGroupPython] Space  # scripted group (container) (typed FeaturePython)
  Group = -> [G4_KEVLAR,G4_DACRON,G4_NEOPRENE]
FEATURE [App::DocumentObjectGroupPython] H_element121  label="H_element : 068"  # scripted group (container) (typed FeaturePython)
  n = 5
  ref = H_element
FEATURE [App::DocumentObjectGroupPython] C_element131  label="C_element : 076"  # scripted group (container) (typed FeaturePython)
  n = 4
  ref = C_element
FEATURE [App::DocumentObjectGroupPython] N_element051  label="N_element : 3"  # scripted group (container) (typed FeaturePython)
  n = 3
  ref = N_element
FEATURE [App::DocumentObjectGroupPython] O_element113  label="O_element : 066"  # scripted group (container) (typed FeaturePython)
  n = 1
  ref = O_element
FEATURE [App::DocumentObjectGroupPython] G4_CYTOSINE  # scripted group (container) (typed FeaturePython)
  Dunit = g/cm3
  Dvalue = 1.55
  Group = -> [H_element121,C_element131,N_element051,O_element113]
  conduct = 2
  density = 1
  expand = 3
  formula = G4_CYTOSINE
  name = G4_CYTOSINE
  specific = 4
FEATURE [App::DocumentObjectGroupPython] H_element122  label="H_element : 069"  # scripted group (container) (typed FeaturePython)
  n = 6
  ref = H_element
FEATURE [App::DocumentObjectGroupPython] C_element132  label="C_element : 077"  # scripted group (container) (typed FeaturePython)
  n = 5
  ref = C_element
FEATURE [App::DocumentObjectGroupPython] N_element052  label="N_element : 024"  # scripted group (container) (typed FeaturePython)
  n = 2
  ref = N_element
FEATURE [App::DocumentObjectGroupPython] O_element114  label="O_element : 067"  # scripted group (container) (typed FeaturePython)
  n = 2
  ref = O_element
FEATURE [App::DocumentObjectGroupPython] G4_THYMINE  # scripted group (container) (typed FeaturePython)
  Dunit = g/cm3
  Dvalue = 1.23
  Group = -> [H_element122,C_element132,N_element052,O_element114]
  conduct = 2
  density = 1
  expand = 3
  formula = G4_THYMINE
  name = G4_THYMINE
  specific = 4
FEATURE [App::DocumentObjectGroupPython] H_element123  label="H_element : 070"  # scripted group (container) (typed FeaturePython)
  n = 4
  ref = H_element
FEATURE [App::DocumentObjectGroupPython] C_element133  label="C_element : 078"  # scripted group (container) (typed FeaturePython)
  n = 4
  ref = C_element
FEATURE [App::DocumentObjectGroupPython] N_element053  label="N_element : 025"  # scripted group (container) (typed FeaturePython)
  n = 2
  ref = N_element
FEATURE [App::DocumentObjectGroupPython] O_element115  label="O_element : 068"  # scripted group (container) (typed FeaturePython)
  n = 2
  ref = O_element
FEATURE [App::DocumentObjectGroupPython] G4_URACIL  # scripted group (container) (typed FeaturePython)
  Dunit = g/cm3
  Dvalue = 1.32
  Group = -> [H_element123,C_element133,N_element053,O_element115]
  conduct = 2
  density = 1
  expand = 3
  formula = G4_URACIL
  name = G4_URACIL
  specific = 4
FEATURE [App::DocumentObjectGroupPython] H_element124  label="H_element : 071"  # scripted group (container) (typed FeaturePython)
  n = 4
  ref = H_element
FEATURE [App::DocumentObjectGroupPython] C_element134  label="C_element : 079"  # scripted group (container) (typed FeaturePython)
  n = 5
  ref = C_element
FEATURE [App::DocumentObjectGroupPython] N_element054  label="N_element : 026"  # scripted group (container) (typed FeaturePython)
  n = 5
  ref = N_element
FEATURE [App::DocumentObjectGroupPython] G4_DNA_ADENINE  # scripted group (container) (typed FeaturePython)
  Dunit = g/cm3
  Dvalue = 1
  Group = -> [H_element124,C_element134,N_element054]
  conduct = 2
  density = 1
  expand = 3
  formula = G4_DNA_ADENINE
  name = G4_DNA_ADENINE
  specific = 4
FEATURE [App::DocumentObjectGroupPython] H_element125  label="H_element : 072"  # scripted group (container) (typed FeaturePython)
  n = 4
  ref = H_element
FEATURE [App::DocumentObjectGroupPython] C_element135  label="C_element : 080"  # scripted group (container) (typed FeaturePython)
  n = 5
  ref = C_element
FEATURE [App::DocumentObjectGroupPython] N_element055  label="N_element : 027"  # scripted group (container) (typed FeaturePython)
  n = 5
  ref = N_element
FEATURE [App::DocumentObjectGroupPython] O_element116  label="O_element : 069"  # scripted group (container) (typed FeaturePython)
  n = 1
  ref = O_element
FEATURE [App::DocumentObjectGroupPython] G4_DNA_GUANINE  # scripted group (container) (typed FeaturePython)
  Dunit = g/cm3
  Dvalue = 1
  Group = -> [H_element125,C_element135,N_element055,O_element116]
  conduct = 2
  density = 1
  expand = 3
  formula = G4_DNA_GUANINE
  name = G4_DNA_GUANINE
  specific = 4
FEATURE [App::DocumentObjectGroupPython] H_element126  label="H_element : 073"  # scripted group (container) (typed FeaturePython)
  n = 4
  ref = H_element
FEATURE [App::DocumentObjectGroupPython] C_element136  label="C_element : 081"  # scripted group (container) (typed FeaturePython)
  n = 4
  ref = C_element
FEATURE [App::DocumentObjectGroupPython] N_element056  label="N_element : 028"  # scripted group (container) (typed FeaturePython)
  n = 3
  ref = N_element
FEATURE [App::DocumentObjectGroupPython] O_element117  label="O_element : 070"  # scripted group (container) (typed FeaturePython)
  n = 1
  ref = O_element
FEATURE [App::DocumentObjectGroupPython] G4_DNA_CYTOSINE  # scripted group (container) (typed FeaturePython)
  Dunit = g/cm3
  Dvalue = 1
  Group = -> [H_element126,C_element136,N_element056,O_element117]
  conduct = 2
  density = 1
  expand = 3
  formula = G4_DNA_CYTOSINE
  name = G4_DNA_CYTOSINE
  specific = 4
FEATURE [App::DocumentObjectGroupPython] H_element127  label="H_element : 074"  # scripted group (container) (typed FeaturePython)
  n = 5
  ref = H_element
FEATURE [App::DocumentObjectGroupPython] C_element137  label="C_element : 082"  # scripted group (container) (typed FeaturePython)
  n = 5
  ref = C_element
FEATURE [App::DocumentObjectGroupPython] N_element057  label="N_element : 029"  # scripted group (container) (typed FeaturePython)
  n = 2
  ref = N_element
FEATURE [App::DocumentObjectGroupPython] O_element118  label="O_element : 071"  # scripted group (container) (typed FeaturePython)
  n = 2
  ref = O_element
FEATURE [App::DocumentObjectGroupPython] G4_DNA_THYMINE  # scripted group (container) (typed FeaturePython)
  Dunit = g/cm3
  Dvalue = 1
  Group = -> [H_element127,C_element137,N_element057,O_element118]
  conduct = 2
  density = 1
  expand = 3
  formula = G4_DNA_THYMINE
  name = G4_DNA_THYMINE
  specific = 4
FEATURE [App::DocumentObjectGroupPython] H_element128  label="H_element : 075"  # scripted group (container) (typed FeaturePython)
  n = 3
  ref = H_element
FEATURE [App::DocumentObjectGroupPython] C_element138  label="C_element : 083"  # scripted group (container) (typed FeaturePython)
  n = 4
  ref = C_element
FEATURE [App::DocumentObjectGroupPython] N_element058  label="N_element : 030"  # scripted group (container) (typed FeaturePython)
  n = 2
  ref = N_element
FEATURE [App::DocumentObjectGroupPython] O_element119  label="O_element : 072"  # scripted group (container) (typed FeaturePython)
  n = 2
  ref = O_element
FEATURE [App::DocumentObjectGroupPython] G4_DNA_URACIL  # scripted group (container) (typed FeaturePython)
  Dunit = g/cm3
  Dvalue = 1
  Group = -> [H_element128,C_element138,N_element058,O_element119]
  conduct = 2
  density = 1
  expand = 3
  formula = G4_DNA_URACIL
  name = G4_DNA_URACIL
  specific = 4
FEATURE [App::DocumentObjectGroupPython] H_element129  label="H_element : 076"  # scripted group (container) (typed FeaturePython)
  n = 10
  ref = H_element
FEATURE [App::DocumentObjectGroupPython] C_element139  label="C_element : 084"  # scripted group (container) (typed FeaturePython)
  n = 10
  ref = C_element
FEATURE [App::DocumentObjectGroupPython] N_element059  label="N_element : 031"  # scripted group (container) (typed FeaturePython)
  n = 5
  ref = N_element
FEATURE [App::DocumentObjectGroupPython] O_element120  label="O_element : 073"  # scripted group (container) (typed FeaturePython)
  n = 4
  ref = O_element
FEATURE [App::DocumentObjectGroupPython] G4_DNA_ADENOSINE  # scripted group (container) (typed FeaturePython)
  Dunit = g/cm3
  Dvalue = 1
  Group = -> [H_element129,C_element139,N_element059,O_element120]
  conduct = 2
  density = 1
  expand = 3
  formula = G4_DNA_ADENOSINE
  name = G4_DNA_ADENOSINE
  specific = 4
FEATURE [App::DocumentObjectGroupPython] H_element130  label="H_element : 077"  # scripted group (container) (typed FeaturePython)
  n = 10
  ref = H_element
FEATURE [App::DocumentObjectGroupPython] C_element140  label="C_element : 085"  # scripted group (container) (typed FeaturePython)
  n = 10
  ref = C_element
FEATURE [App::DocumentObjectGroupPython] N_element060  label="N_element : 032"  # scripted group (container) (typed FeaturePython)
  n = 5
  ref = N_element
FEATURE [App::DocumentObjectGroupPython] O_element121  label="O_element : 074"  # scripted group (container) (typed FeaturePython)
  n = 5
  ref = O_element
FEATURE [App::DocumentObjectGroupPython] G4_DNA_GUANOSINE  # scripted group (container) (typed FeaturePython)
  Dunit = g/cm3
  Dvalue = 1
  Group = -> [H_element130,C_element140,N_element060,O_element121]
  conduct = 2
  density = 1
  expand = 3
  formula = G4_DNA_GUANOSINE
  name = G4_DNA_GUANOSINE
  specific = 4
FEATURE [App::DocumentObjectGroupPython] H_element131  label="H_element : 078"  # scripted group (container) (typed FeaturePython)
  n = 10
  ref = H_element
FEATURE [App::DocumentObjectGroupPython] C_element141  label="C_element : 086"  # scripted group (container) (typed FeaturePython)
  n = 9
  ref = C_element
FEATURE [App::DocumentObjectGroupPython] N_element061  label="N_element : 033"  # scripted group (container) (typed FeaturePython)
  n = 3
  ref = N_element
FEATURE [App::DocumentObjectGroupPython] O_element122  label="O_element : 075"  # scripted group (container) (typed FeaturePython)
  n = 5
  ref = O_element
FEATURE [App::DocumentObjectGroupPython] G4_DNA_CYTIDINE  # scripted group (container) (typed FeaturePython)
  Dunit = g/cm3
  Dvalue = 1
  Group = -> [H_element131,C_element141,N_element061,O_element122]
  conduct = 2
  density = 1
  expand = 3
  formula = G4_DNA_CYTIDINE
  name = G4_DNA_CYTIDINE
  specific = 4
FEATURE [App::DocumentObjectGroupPython] H_element132  label="H_element : 079"  # scripted group (container) (typed FeaturePython)
  n = 9
  ref = H_element
FEATURE [App::DocumentObjectGroupPython] C_element142  label="C_element : 087"  # scripted group (container) (typed FeaturePython)
  n = 9
  ref = C_element
FEATURE [App::DocumentObjectGroupPython] N_element062  label="N_element : 034"  # scripted group (container) (typed FeaturePython)
  n = 2
  ref = N_element
FEATURE [App::DocumentObjectGroupPython] O_element123  label="O_element : 076"  # scripted group (container) (typed FeaturePython)
  n = 6
  ref = O_element
FEATURE [App::DocumentObjectGroupPython] G4_DNA_URIDINE  # scripted group (container) (typed FeaturePython)
  Dunit = g/cm3
  Dvalue = 1
  Group = -> [H_element132,C_element142,N_element062,O_element123]
  conduct = 2
  density = 1
  expand = 3
  formula = G4_DNA_URIDINE
  name = G4_DNA_URIDINE
  specific = 4
FEATURE [App::DocumentObjectGroupPython] H_element133  label="H_element : 080"  # scripted group (container) (typed FeaturePython)
  n = 11
  ref = H_element
FEATURE [App::DocumentObjectGroupPython] C_element143  label="C_element : 088"  # scripted group (container) (typed FeaturePython)
  n = 10
  ref = C_element
FEATURE [App::DocumentObjectGroupPython] N_element063  label="N_element : 035"  # scripted group (container) (typed FeaturePython)
  n = 2
  ref = N_element
FEATURE [App::DocumentObjectGroupPython] O_element124  label="O_element : 077"  # scripted group (container) (typed FeaturePython)
  n = 6
  ref = O_element
FEATURE [App::DocumentObjectGroupPython] G4_DNA_METHYLURIDINE  # scripted group (container) (typed FeaturePython)
  Dunit = g/cm3
  Dvalue = 1
  Group = -> [H_element133,C_element143,N_element063,O_element124]
  conduct = 2
  density = 1
  expand = 3
  formula = G4_DNA_METHYLURIDINE
  name = G4_DNA_METHYLURIDINE
  specific = 4
FEATURE [App::DocumentObjectGroupPython] P_element014  label="P_element : 003"  # scripted group (container) (typed FeaturePython)
  n = 1
  ref = P_element
FEATURE [App::DocumentObjectGroupPython] O_element125  label="O_element : 078"  # scripted group (container) (typed FeaturePython)
  n = 3
  ref = O_element
FEATURE [App::DocumentObjectGroupPython] G4_DNA_MONOPHOSPHATE  # scripted group (container) (typed FeaturePython)
  Dunit = g/cm3
  Dvalue = 1
  Group = -> [P_element014,O_element125]
  conduct = 2
  density = 1
  expand = 3
  formula = G4_DNA_MONOPHOSPHATE
  name = G4_DNA_MONOPHOSPHATE
  specific = 4
FEATURE [App::DocumentObjectGroupPython] H_element134  label="H_element : 081"  # scripted group (container) (typed FeaturePython)
  n = 10
  ref = H_element
FEATURE [App::DocumentObjectGroupPython] C_element144  label="C_element : 089"  # scripted group (container) (typed FeaturePython)
  n = 10
  ref = C_element
FEATURE [App::DocumentObjectGroupPython] N_element064  label="N_element : 036"  # scripted group (container) (typed FeaturePython)
  n = 5
  ref = N_element
FEATURE [App::DocumentObjectGroupPython] O_element126  label="O_element : 079"  # scripted group (container) (typed FeaturePython)
  n = 7
  ref = O_element
FEATURE [App::DocumentObjectGroupPython] P_element015  label="P_element : 004"  # scripted group (container) (typed FeaturePython)
  n = 1
  ref = P_element
FEATURE [App::DocumentObjectGroupPython] G4_DNA_A  # scripted group (container) (typed FeaturePython)
  Dunit = g/cm3
  Dvalue = 1
  Group = -> [H_element134,C_element144,N_element064,O_element126,P_element015]
  conduct = 2
  density = 1
  expand = 3
  formula = G4_DNA_A
  name = G4_DNA_A
  specific = 4
FEATURE [App::DocumentObjectGroupPython] H_element135  label="H_element : 082"  # scripted group (container) (typed FeaturePython)
  n = 10
  ref = H_element
FEATURE [App::DocumentObjectGroupPython] C_element145  label="C_element : 090"  # scripted group (container) (typed FeaturePython)
  n = 10
  ref = C_element
FEATURE [App::DocumentObjectGroupPython] N_element065  label="N_element : 037"  # scripted group (container) (typed FeaturePython)
  n = 5
  ref = N_element
FEATURE [App::DocumentObjectGroupPython] O_element127  label="O_element : 8"  # scripted group (container) (typed FeaturePython)
  n = 8
  ref = O_element
FEATURE [App::DocumentObjectGroupPython] P_element016  label="P_element : 005"  # scripted group (container) (typed FeaturePython)
  n = 1
  ref = P_element
FEATURE [App::DocumentObjectGroupPython] G4_DNA_G  # scripted group (container) (typed FeaturePython)
  Dunit = g/cm3
  Dvalue = 1
  Group = -> [H_element135,C_element145,N_element065,O_element127,P_element016]
  conduct = 2
  density = 1
  expand = 3
  formula = G4_DNA_G
  name = G4_DNA_G
  specific = 4
FEATURE [App::DocumentObjectGroupPython] H_element136  label="H_element : 083"  # scripted group (container) (typed FeaturePython)
  n = 10
  ref = H_element
FEATURE [App::DocumentObjectGroupPython] C_element146  label="C_element : 091"  # scripted group (container) (typed FeaturePython)
  n = 9
  ref = C_element
FEATURE [App::DocumentObjectGroupPython] N_element066  label="N_element : 038"  # scripted group (container) (typed FeaturePython)
  n = 3
  ref = N_element
FEATURE [App::DocumentObjectGroupPython] O_element128  label="O_element : 080"  # scripted group (container) (typed FeaturePython)
  n = 8
  ref = O_element
FEATURE [App::DocumentObjectGroupPython] P_element017  label="P_element : 006"  # scripted group (container) (typed FeaturePython)
  n = 1
  ref = P_element
FEATURE [App::DocumentObjectGroupPython] G4_DNA_C  # scripted group (container) (typed FeaturePython)
  Dunit = g/cm3
  Dvalue = 1
  Group = -> [H_element136,C_element146,N_element066,O_element128,P_element017]
  conduct = 2
  density = 1
  expand = 3
  formula = G4_DNA_C
  name = G4_DNA_C
  specific = 4
FEATURE [App::DocumentObjectGroupPython] H_element137  label="H_element : 084"  # scripted group (container) (typed FeaturePython)
  n = 9
  ref = H_element
FEATURE [App::DocumentObjectGroupPython] C_element147  label="C_element : 092"  # scripted group (container) (typed FeaturePython)
  n = 9
  ref = C_element
FEATURE [App::DocumentObjectGroupPython] N_element067  label="N_element : 039"  # scripted group (container) (typed FeaturePython)
  n = 2
  ref = N_element
FEATURE [App::DocumentObjectGroupPython] O_element129  label="O_element : 9"  # scripted group (container) (typed FeaturePython)
  n = 9
  ref = O_element
FEATURE [App::DocumentObjectGroupPython] P_element018  label="P_element : 007"  # scripted group (container) (typed FeaturePython)
  n = 1
  ref = P_element
FEATURE [App::DocumentObjectGroupPython] G4_DNA_U  # scripted group (container) (typed FeaturePython)
  Dunit = g/cm3
  Dvalue = 1
  Group = -> [H_element137,C_element147,N_element067,O_element129,P_element018]
  conduct = 2
  density = 1
  expand = 3
  formula = G4_DNA_U
  name = G4_DNA_U
  specific = 4
FEATURE [App::DocumentObjectGroupPython] H_element138  label="H_element : 085"  # scripted group (container) (typed FeaturePython)
  n = 11
  ref = H_element
FEATURE [App::DocumentObjectGroupPython] C_element148  label="C_element : 093"  # scripted group (container) (typed FeaturePython)
  n = 10
  ref = C_element
FEATURE [App::DocumentObjectGroupPython] N_element068  label="N_element : 040"  # scripted group (container) (typed FeaturePython)
  n = 2
  ref = N_element
FEATURE [App::DocumentObjectGroupPython] O_element130  label="O_element : 081"  # scripted group (container) (typed FeaturePython)
  n = 9
  ref = O_element
FEATURE [App::DocumentObjectGroupPython] P_element019  label="P_element : 008"  # scripted group (container) (typed FeaturePython)
  n = 1
  ref = P_element
FEATURE [App::DocumentObjectGroupPython] G4_DNA_MU  # scripted group (container) (typed FeaturePython)
  Dunit = g/cm3
  Dvalue = 1
  Group = -> [H_element138,C_element148,N_element068,O_element130,P_element019]
  conduct = 2
  density = 1
  expand = 3
  formula = G4_DNA_MU
  name = G4_DNA_MU
  specific = 4
FEATURE [App::DocumentObjectGroupPython] BioChemical  # scripted group (container) (typed FeaturePython)
  Group = -> [G4_CYTOSINE,G4_THYMINE,G4_URACIL,G4_DNA_ADENINE,G4_DNA_GUANINE,G4_DNA_CYTOSINE,G4_DNA_THYMINE,G4_DNA_URACIL,G4_DNA_ADENOSINE,G4_DNA_GUANOSINE,G4_DNA_CYTIDINE,G4_DNA_URIDINE,G4_DNA_METHYLURIDINE,G4_DNA_MONOPHOSPHATE,G4_DNA_A,G4_DNA_G,G4_DNA_C,G4_DNA_U,G4_DNA_MU]
FEATURE [App::DocumentObjectGroupPython] G4Materials  # scripted group (container) (typed FeaturePython)
  Group = -> [NIST,Element,HEP,Space,BioChemical]
  version = 1
FEATURE [App::DocumentObjectGroupPython] Geant4  # scripted group (container) (typed FeaturePython)
  Group = -> [G4Isotopes,G4Elements,G4Materials]
FEATURE [App::DocumentObjectGroupPython] Materials  # scripted group (container) (typed FeaturePython)
  Group = -> [Geant4]
FEATURE [Part::FeaturePython] GDMLBox_WorldBox  # WARN: FeaturePython — macro-defined, semantics opaque (R4)
  lunit = 2
  material = 5
  x = 273
  y = 273
  z = 130
FEATURE [Part::FeaturePython] GDMLBox_Box  # WARN: FeaturePython — macro-defined, semantics opaque (R4)
  lunit = 2
  material = 0
  x = 10
  y = 10
  z = 10
FEATURE [Part::FeaturePython] GDMLTube  # WARN: FeaturePython — macro-defined, semantics opaque (R4)
  aunit = 1
  deltaphi = 90
  lunit = 2
  material = 0
  rmax = 7
  rmin = 5
  startphi = 0
  z = 7
FEATURE [App::Part] LV_Tube
  Group = -> [GDMLTube]
  Origin = -> Origin003
  SkinSurface = 0
FEATURE [App::Part] LV_Box
  Group = -> [GDMLBox_Box,LV_Tube]
  Origin = -> Origin002
  Placement = pos=(20,0,0) rot=(0,0,1;0rad)
FEATURE [Part::FeaturePython] Array  # Draft array (typed FeaturePython)
  AlwaysSyncPlacement = false
  Angle = 180
  ArrayType = 1
  Axis = (0,0,1)
  Base = -> LV_Box
  Center = (0,0,0)
  Count = 5
  ExpandArray = false
  Fuse = false
  IntervalAxis = (0,0,0)
  IntervalX = (100,0,0)
  IntervalY = (0,100,0)
  IntervalZ = (0,0,100)
  NumberCircles = 3
  NumberPolar = 5
  NumberX = 2
  NumberY = 2
  NumberZ = 1
  PlacementList = 5 placements: [(20,0,0),(14.1421,14.1421,0),(3.55271e-15,20,0),(-14.1421,14.1421,0),(-20,2.44929e-15,0)]
  RadialDistance = 50
  ScaleList = (5) [(1,1,1),(1,1,1),(1,1,1),(1,1,1),(1,1,1)]
  Symmetry = 1
  TangentialDistance = 25
FEATURE [App::Part] Part  label="experiment"
  Group = -> [LV_Box,Array]
  Origin = -> Origin001
FEATURE [App::Part] worldVOL
  Group = -> [GDMLBox_WorldBox,Part]
  Origin = -> Origin
